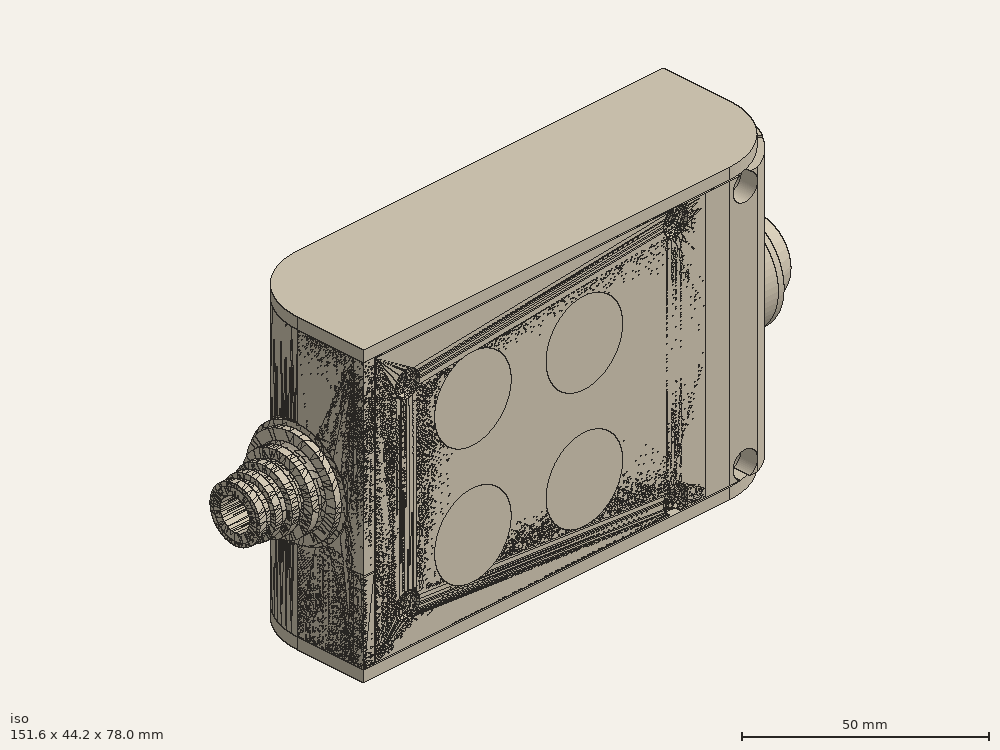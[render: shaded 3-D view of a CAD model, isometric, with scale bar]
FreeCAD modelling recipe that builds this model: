
FCSTD DOCUMENT  (FreeCAD 0.19R0.19.2)
Label: enclosure_160
License: All rights reserved
LicenseURL: http://en.wikipedia.org/wiki/All_rights_reserved
objects: Part::Feature×140, Part::Revolution×140, Part::MultiFuse×120, Sketcher::SketchObject×67, Part::Extrusion×52, Part::Fillet×51, Part::Cut×51, Part::Cylinder×50, Part::Box×33, App::MeasureDistance×4
note: 704 computed .brp shape members not serialized (recipe doc carries the construction recipe); baked Part::Feature solids carry a one-line shape summary decoded from their .brp

FEATURE [Sketcher::SketchObject] Sketch  label="topSketch"
  FullyConstrained = true
  sketch-geometry (20):
    g0: LineSegment StartX=5.21097e-06 StartY=3 StartZ=0 EndX=5.21097e-06 EndY=19 EndZ=0
    g1: ArcOfCircle CenterX=19 CenterY=19 CenterZ=0 NormalX=0 NormalY=0 NormalZ=1 AngleXU=0 Radius=19 StartAngle=1.5708 EndAngle=3.14159
    g2: ArcOfCircle CenterX=19 CenterY=19 CenterZ=0 NormalX=0 NormalY=0 NormalZ=1 AngleXU=0 Radius=16 StartAngle=1.5708 EndAngle=3.14159
    g3: LineSegment StartX=114 StartY=35 StartZ=0 EndX=19 EndY=35 EndZ=0
    g4: LineSegment StartX=5.21097e-06 StartY=3 StartZ=0 EndX=5.21097e-06 EndY=0 EndZ=0
    g5: LineSegment StartX=3 StartY=0 StartZ=0 EndX=5.21097e-06 EndY=0 EndZ=0
    g6: LineSegment StartX=3 StartY=19 StartZ=0 EndX=3 EndY=0 EndZ=0
    g7: LineSegment StartX=19 StartY=38 StartZ=0 EndX=124 EndY=38 EndZ=0
    g8: Circle CenterX=119 CenterY=35 CenterZ=0 NormalX=0 NormalY=0 NormalZ=1 AngleXU=0 Radius=1
    g9: Circle CenterX=121 CenterY=35 CenterZ=0 NormalX=0 NormalY=0 NormalZ=1 AngleXU=0 Radius=1
    g10: Circle CenterX=121 CenterY=33 CenterZ=0 NormalX=0 NormalY=0 NormalZ=1 AngleXU=0 Radius=1
    g11: BSplineCurve PolesCount=3 KnotsCount=2 Degree=2 IsPeriodic=0
    g12: GeomPoint X=119 Y=35 Z=0
    g13: GeomPoint X=121 Y=33 Z=0
    g14: LineSegment StartX=119 StartY=35 StartZ=0 EndX=114 EndY=35 EndZ=0
    g15: ArcOfCircle CenterX=105 CenterY=19 CenterZ=0 NormalX=0 NormalY=0 NormalZ=1 AngleXU=0 Radius=19 StartAngle=5.7297 EndAngle=6.28319
    g16: ArcOfCircle CenterX=105 CenterY=19 CenterZ=0 NormalX=0 NormalY=0 NormalZ=1 AngleXU=0 Radius=16 StartAngle=5.60905 EndAngle=6.28319
    g17: LineSegment StartX=121 StartY=33 StartZ=0 EndX=121 EndY=19 EndZ=0
    g18: LineSegment StartX=124 StartY=38 StartZ=0 EndX=124 EndY=19 EndZ=0
    g19: LineSegment StartX=117.5 StartY=9.01251 StartZ=0 EndX=121.163 EndY=9.0125 EndZ=0
  constraints (46):
    c: Vertical(g0)
    c: Block(g0)
    c: Coincident(g1,g0)
    c: Block(g1)
    c: Coincident(g2,g1)
    c: Block(g2)
    c: Coincident(g3,g2)
    c: Horizontal(g3)
    c: Tangent(g3,g2)
    c: Coincident(g4,g0)
    c: Distance(g4) = 3
    c: Vertical(g4)
    c: Coincident(g5,g4)
    c: Horizontal(g5)
    c: Coincident(g6,g2)
    c: Coincident(g6,g5)
    c: Vertical(g6)
    c: Horizontal(g7)
    c: Distance(g7) = 105
    c: Coincident(g7,g1)
    c: Block(g3)
    c: Weight(g8) = 1
    c: Equal(g8,g9)
    c: Equal(g8,g10)
    c: InternalAlignment(g8,g11)
    c: InternalAlignment(g9,g11)
    c: InternalAlignment(g10,g11)
    c: InternalAlignment(g12,g11)
    c: InternalAlignment(g13,g11)
    c: Block(g11)
    c: Coincident(g14,g11)
    c: Coincident(g14,g3)
    c: Horizontal(g14)
    c: Block(g15)
    c: Coincident(g16,g15)
    c: Block(g16)
    c: Coincident(g17,g11)
    c: Coincident(g17,g16)
    c: Vertical(g17)
    c: Distance(g17) = 14
    c: Coincident(g18,g7)
    c: Coincident(g18,g15)
    c: Vertical(g18)
    c: Distance(g18) = 19
    c: Coincident(g19,g16)
    c: Coincident(g19,g15)
FEATURE [Sketcher::SketchObject] Sketch001  label="bottomSketch"
  FullyConstrained = true
  sketch-geometry (32):
    g0: LineSegment StartX=3.3 StartY=-6.03275e-07 StartZ=0 EndX=98 EndY=-6.03275e-07 EndZ=0
    g1: ArcOfCircle CenterX=98 CenterY=19 CenterZ=0 NormalX=0 NormalY=0 NormalZ=1 AngleXU=0 Radius=19 StartAngle=4.71239 EndAngle=5.71103
    g2: LineSegment StartX=6.3 StartY=8 StartZ=0 EndX=3.3 EndY=8 EndZ=0
    g3: LineSegment StartX=3.3 StartY=8 StartZ=0 EndX=3.3 EndY=-6.03275e-07 EndZ=0
    g4: ArcOfCircle CenterX=8.3 CenterY=5 CenterZ=0 NormalX=0 NormalY=0 NormalZ=1 AngleXU=0 Radius=2 StartAngle=3.14159 EndAngle=4.71239
    g5: LineSegment StartX=6.3 StartY=8 StartZ=0 EndX=6.3 EndY=5 EndZ=0
    g6: ArcOfCircle CenterX=98 CenterY=19 CenterZ=0 NormalX=0 NormalY=0 NormalZ=1 AngleXU=0 Radius=12.7 StartAngle=4.71239 EndAngle=6.28319
    g7: LineSegment StartX=94.7 StartY=3 StartZ=0 EndX=8.3 EndY=3 EndZ=0
    g8-g12: Circle x5 (B-spline internal-alignment scaffolding for g13; pole/knot coordinates omitted)
    g13: BSplineCurve PolesCount=5 KnotsCount=3 Degree=3 IsPeriodic=0
    g14: GeomPoint X=98 Y=6.3 Z=0
    g15: GeomPoint X=96.3938 Y=4.71946 Z=0
    g16: GeomPoint X=94.7 Y=3 Z=0
    g17-g23: Circle x7 (B-spline internal-alignment scaffolding for g24; pole/knot coordinates omitted)
    g24: BSplineCurve PolesCount=7 KnotsCount=5 Degree=3 IsPeriodic=0
    g25-g29: GeomPoint x5 (B-spline internal-alignment scaffolding for g24; pole/knot coordinates omitted)
    g30: ArcOfCircle CenterX=98 CenterY=19 CenterZ=0 NormalX=0 NormalY=0 NormalZ=1 AngleXU=0 Radius=15.7 StartAngle=5.81226 EndAngle=6.28319
    g31: LineSegment StartX=110.7 StartY=19 StartZ=0 EndX=113.7 EndY=19 EndZ=0
  constraints (41):
    c: Horizontal(g0)
    c: Coincident(g1,g0)
    c: Block(g1)
    c: Horizontal(g2)
    c: Distance(g2) = 3
    c: Coincident(g3,g2)
    c: Vertical(g3)
    c: Coincident(g3,g0)
    c: Block(g4)
    c: Block(g2)
    c: Coincident(g5,g2)
    c: Coincident(g5,g4)
    c: Vertical(g5)
    c: Coincident(g6,g1)
    c: Block(g6)
    c: Coincident(g7,g4)
    c: Horizontal(g7)
    c: Block(g0)
    c: Block(g7)
    c: Block(g3)
    c: Coincident(g13,g6)
    c: Weight(g8) = 1
    c: Equal(g8, g9-g12) x4
    c: Coincident(g13,g7)
    c: InternalAlignment(g8-g12 -> g13) x5
    c: InternalAlignment(g14,g13)
    c: InternalAlignment(g15,g13)
    c: InternalAlignment(g16,g13)
    c: Block(g13)
    c: Weight(g17) = 1
    c: Equal(g17, g18-g23) x6
    c: Coincident(g24,g1)
    c: InternalAlignment(g17-g23 -> g24) x7
    c: InternalAlignment(g25-g29 -> g24) x5
    c: Block(g24)
    c: Coincident(g30,g24)
    c: Coincident(g31,g6)
    c: Coincident(g31,g30)
    c: Horizontal(g31)
    c: Block(g31)
    c: Block(g30)
FEATURE [Part::Extrusion] Extrude  label="top"
  Base = -> Sketch
  Dir = (0,0,1)
  DirMode = 2
  FaceMakerClass = Part::FaceMakerBullseye
  LengthFwd = 72
  LengthRev = 0
  Solid = true
  Symmetric = false
FEATURE [Part::Extrusion] Extrude001  label="bottom"
  Base = -> Sketch001
  Dir = (0,0,1)
  DirMode = 2
  FaceMakerClass = Part::FaceMakerBullseye
  LengthFwd = 71.4
  LengthRev = 0
  Placement = pos=(0,0,0.3) rot=(0,0,1;0rad)
  Solid = true
  Symmetric = false
FEATURE [Sketcher::SketchObject] Sketch002  label="topSketch001"
  FullyConstrained = true
  sketch-geometry (6):
    g0: ArcOfCircle CenterX=19 CenterY=19 CenterZ=0 NormalX=0 NormalY=0 NormalZ=1 AngleXU=0 Radius=19 StartAngle=1.5708 EndAngle=3.14159
    g1: LineSegment StartX=5.22862e-06 StartY=19 StartZ=0 EndX=5.22862e-06 EndY=1.19904e-11 EndZ=0
    g2: LineSegment StartX=19 StartY=38 StartZ=0 EndX=124 EndY=38 EndZ=0
    g3: LineSegment StartX=5.22862e-06 StartY=1.19904e-11 StartZ=0 EndX=105 EndY=1.19904e-11 EndZ=0
    g4: ArcOfCircle CenterX=105 CenterY=19 CenterZ=0 NormalX=0 NormalY=0 NormalZ=1 AngleXU=0 Radius=19 StartAngle=4.71239 EndAngle=6.28319
    g5: LineSegment StartX=124 StartY=38 StartZ=0 EndX=124 EndY=19 EndZ=0
  constraints (16):
    c: Block(g0)
    c: Coincident(g1,g0)
    c: Vertical(g1)
    c: Horizontal(g2)
    c: Distance(g2) = 105
    c: Coincident(g2,g0)
    c: Distance(g1) = 19
    c: Coincident(g3,g1)
    c: Horizontal(g3)
    c: Distance(g3) = 105
    c: Block(g4)
    c: Coincident(g4,g3)
    c: Coincident(g5,g2)
    c: Coincident(g5,g4)
    c: Vertical(g5)
    c: Distance(g5) = 19
FEATURE [Part::Extrusion] Extrude002  label="sideA"
  Base = -> Sketch002
  Dir = (0,0,1)
  DirMode = 2
  FaceMakerClass = Part::FaceMakerBullseye
  LengthFwd = 3
  LengthRev = 0
  Placement = pos=(0,0,-3) rot=(0,0,1;0rad)
  Solid = true
  Symmetric = false
FEATURE [Sketcher::SketchObject] Sketch003  label="topSketch002"
  FullyConstrained = true
  sketch-geometry (6):
    g0: LineSegment StartX=19 StartY=38 StartZ=0 EndX=117 EndY=38 EndZ=0
    g1: ArcOfCircle CenterX=19 CenterY=19 CenterZ=0 NormalX=0 NormalY=0 NormalZ=1 AngleXU=0 Radius=19 StartAngle=1.5708 EndAngle=3.14159
    g2: LineSegment StartX=117 StartY=38 StartZ=0 EndX=117 EndY=19 EndZ=0
    g3: LineSegment StartX=98 StartY=1.0161e-12 StartZ=0 EndX=5.22862e-06 EndY=1.0161e-12 EndZ=0
    g4: LineSegment StartX=5.22862e-06 StartY=19 StartZ=0 EndX=5.22862e-06 EndY=1.0161e-12 EndZ=0
    g5: ArcOfCircle CenterX=98 CenterY=19 CenterZ=0 NormalX=0 NormalY=0 NormalZ=1 AngleXU=0 Radius=19 StartAngle=4.71239 EndAngle=6.28319
  constraints (16):
    c: Horizontal(g0)
    c: Distance(g0) = 98
    c: Coincident(g1,g0)
    c: Block(g1)
    c: Coincident(g2,g0)
    c: Vertical(g2)
    c: Distance(g2) = 19
    c: Horizontal(g3)
    c: Coincident(g4,g1)
    c: Vertical(g4)
    c: Coincident(g3,g4)
    c: Block(g3)
    c: Coincident(g5,g2)
    c: Coincident(g5,g3)
    c: Block(g0)
    c: Block(g5)
FEATURE [Sketcher::SketchObject] Sketch004
  FullyConstrained = true
  MapMode = 3
  Placement = pos=(0,0,0) rot=(1,0,0;1.5708rad)
  Support = -> [Extrude]
  sketch-geometry (8):
    g0: Circle CenterX=80.351 CenterY=-67.6202 CenterZ=0 NormalX=0 NormalY=0 NormalZ=1 AngleXU=0 Radius=2
    g1: Circle CenterX=80.351 CenterY=-67.6202 CenterZ=0 NormalX=0 NormalY=0 NormalZ=1 AngleXU=0 Radius=3
    g2: Circle CenterX=80.351 CenterY=-4.92017 CenterZ=0 NormalX=0 NormalY=0 NormalZ=1 AngleXU=0 Radius=2
    g3: Circle CenterX=80.351 CenterY=-4.92017 CenterZ=0 NormalX=0 NormalY=0 NormalZ=1 AngleXU=0 Radius=3
    g4: Circle CenterX=23.851 CenterY=-4.92017 CenterZ=0 NormalX=0 NormalY=0 NormalZ=1 AngleXU=0 Radius=2
    g5: Circle CenterX=23.851 CenterY=-4.92017 CenterZ=0 NormalX=0 NormalY=0 NormalZ=1 AngleXU=0 Radius=3
    g6: Circle CenterX=23.851 CenterY=-67.6202 CenterZ=0 NormalX=0 NormalY=0 NormalZ=1 AngleXU=0 Radius=2
    g7: Circle CenterX=23.851 CenterY=-67.6202 CenterZ=0 NormalX=0 NormalY=0 NormalZ=1 AngleXU=0 Radius=3
  constraints (8):
    c: Block(g3)
    c: Block(g2)
    c: Block(g1)
    c: Block(g0)
    c: Block(g6)
    c: Block(g7)
    c: Block(g4)
    c: Block(g5)
FEATURE [Part::Extrusion] Extrude004
  Base = -> Sketch004
  Dir = (0,-1,2e-16)
  DirMode = 2
  FaceMakerClass = Part::FaceMakerBullseye
  LengthFwd = 6
  LengthRev = 0
  Placement = pos=(0,9,0) rot=(0,0,1;0rad)
  Solid = true
  Symmetric = false
FEATURE [Sketcher::SketchObject] Sketch005
  FullyConstrained = true
  MapMode = 3
  Placement = pos=(0,0,0) rot=(1,0,0;1.5708rad)
  Support = -> [Extrude]
  sketch-geometry (8):
    g0: Circle CenterX=80.351 CenterY=-67.6202 CenterZ=0 NormalX=0 NormalY=0 NormalZ=1 AngleXU=0 Radius=3
    g1: Circle CenterX=80.351 CenterY=-4.92017 CenterZ=0 NormalX=0 NormalY=0 NormalZ=1 AngleXU=0 Radius=3
    g2: Circle CenterX=23.851 CenterY=-4.92017 CenterZ=0 NormalX=0 NormalY=0 NormalZ=1 AngleXU=0 Radius=3
    g3: Circle CenterX=23.851 CenterY=-67.6202 CenterZ=0 NormalX=0 NormalY=0 NormalZ=1 AngleXU=0 Radius=3
    g4: Circle CenterX=23.851 CenterY=-67.6202 CenterZ=0 NormalX=0 NormalY=0 NormalZ=1 AngleXU=0 Radius=5
    g5: Circle CenterX=80.351 CenterY=-67.6202 CenterZ=0 NormalX=0 NormalY=0 NormalZ=1 AngleXU=0 Radius=5
    g6: Circle CenterX=23.851 CenterY=-4.92017 CenterZ=0 NormalX=0 NormalY=0 NormalZ=1 AngleXU=0 Radius=5
    g7: Circle CenterX=80.351 CenterY=-4.92017 CenterZ=0 NormalX=0 NormalY=0 NormalZ=1 AngleXU=0 Radius=5
  constraints (8):
    c: Block(g1)
    c: Block(g0)
    c: Block(g3)
    c: Block(g2)
    c: Block(g5)
    c: Block(g4)
    c: Block(g6)
    c: Block(g7)
FEATURE [Part::Extrusion] Extrude005
  Base = -> Sketch005
  Dir = (0,-1,2e-16)
  DirMode = 2
  FaceMakerClass = Part::FaceMakerBullseye
  LengthFwd = 2
  LengthRev = 0
  Solid = true
  Symmetric = false
FEATURE [Sketcher::SketchObject] Sketch006
  FullyConstrained = true
  MapMode = 3
  Placement = pos=(0,0,0) rot=(1,0,0;1.5708rad)
  sketch-geometry (8):
    g0: Circle CenterX=80.351 CenterY=-67.6202 CenterZ=0 NormalX=0 NormalY=0 NormalZ=1 AngleXU=0 Radius=3
    g1: Circle CenterX=80.351 CenterY=-4.92017 CenterZ=0 NormalX=0 NormalY=0 NormalZ=1 AngleXU=0 Radius=3
    g2: Circle CenterX=23.851 CenterY=-4.92017 CenterZ=0 NormalX=0 NormalY=0 NormalZ=1 AngleXU=0 Radius=3
    g3: Circle CenterX=23.851 CenterY=-67.6202 CenterZ=0 NormalX=0 NormalY=0 NormalZ=1 AngleXU=0 Radius=3
    g4: Circle CenterX=23.851 CenterY=-67.6202 CenterZ=0 NormalX=0 NormalY=0 NormalZ=1 AngleXU=0 Radius=5
    g5: Circle CenterX=80.351 CenterY=-67.6202 CenterZ=0 NormalX=0 NormalY=0 NormalZ=1 AngleXU=0 Radius=5
    g6: Circle CenterX=23.851 CenterY=-4.92017 CenterZ=0 NormalX=0 NormalY=0 NormalZ=1 AngleXU=0 Radius=5
    g7: Circle CenterX=80.351 CenterY=-4.92017 CenterZ=0 NormalX=0 NormalY=0 NormalZ=1 AngleXU=0 Radius=5
  constraints (8):
    c: Block(g1)
    c: Block(g0)
    c: Block(g3)
    c: Block(g2)
    c: Block(g5)
    c: Block(g4)
    c: Block(g6)
    c: Block(g7)
FEATURE [Part::Extrusion] Extrude007
  Base = -> Sketch006
  Dir = (0,-1,2e-16)
  DirMode = 2
  FaceMakerClass = Part::FaceMakerBullseye
  LengthFwd = 2
  LengthRev = 0
  Solid = true
  Symmetric = false
FEATURE [Part::Fillet] Fillet
  Base = -> Extrude007
  Edges = 4 edges r=1.99: [Edge6,Edge12,Edge18,Edge24]
FEATURE [Part::Cut] Cut
  Base = -> Extrude005
  Placement = pos=(0,5,0) rot=(0,0,1;0rad)
  Tool = -> Fillet
FEATURE [Part::MultiFuse] Fusion  label="pCBScrews"
  Placement = pos=(-2.5,0,72.3) rot=(0,0,1;0rad)
  Shapes = -> [Extrude004,Cut]
FEATURE [App::MeasureDistance] Distance  label="Distance: 0.69 mm"
  Distance = 0.685967
  P1 = (24.0138,2.9647,0.3)
  P2 = (23.8901,3,-0.373787)
FEATURE [App::MeasureDistance] Distance001  label="Distance: 0.53 mm"
  Distance = 0.533607
  P1 = (80.2939,3,72.2334)
  P2 = (80.281,2.99661,71.7)
FEATURE [Part::Fillet] Fillet001
  Base = -> Extrude001
  Edges = 1 edges r=2.4: [Edge17]
FEATURE [Part::Fillet] Fillet002  label="bottom001"
  Base = -> Fillet001
  Edges = 1 edges r=2.4: [Edge36]
FEATURE [Part::Fillet] Fillet003  label="top001"
  Base = -> Extrude
  Edges = 1 edges r=2: [Edge1]
FEATURE [Sketcher::SketchObject] Sketch007
  FullyConstrained = true
  sketch-geometry (16):
    g0: LineSegment StartX=4 StartY=0 StartZ=0 EndX=4 EndY=2.4 EndZ=0
    g1: LineSegment StartX=4 StartY=2.4 StartZ=0 EndX=7 EndY=2.4 EndZ=0
    g2: LineSegment StartX=4 StartY=0 StartZ=0 EndX=5.7 EndY=0 EndZ=0
    g3: LineSegment StartX=5.7 StartY=0 StartZ=0 EndX=5.7 EndY=-5.6 EndZ=0
    g4-g8: Circle x5 (B-spline internal-alignment scaffolding for g9; pole/knot coordinates omitted)
    g9: BSplineCurve PolesCount=5 KnotsCount=3 Degree=3 IsPeriodic=0
    g10: GeomPoint X=7 Y=2.4 Z=0
    g11: GeomPoint X=10.4582 Y=-1.55472 Z=0
    g12: GeomPoint X=14 Y=-5.6 Z=0
    g13: LineSegment StartX=14 StartY=-5.6 StartZ=0 EndX=14 EndY=-14.1 EndZ=0
    g14: LineSegment StartX=14 StartY=-14.1 StartZ=0 EndX=6.5 EndY=-14.1 EndZ=0
    g15: LineSegment StartX=5.7 StartY=-5.6 StartZ=0 EndX=6.5 EndY=-14.1 EndZ=0
  constraints (28):
    c: Distance(g0) = 2.4
    c: Vertical(g0)
    c: Block(g0)
    c: Coincident(g1,g0)
    c: Horizontal(g1)
    c: Distance(g1) = 3
    c: Coincident(g2,g0)
    c: Horizontal(g2)
    c: Distance(g2) = 1.7
    c: Coincident(g3,g2)
    c: Vertical(g3)
    c: Distance(g3) = 5.6
    c: Coincident(g9,g1)
    c: Weight(g4) = 1
    c: Equal(g4, g5-g8) x4
    c: InternalAlignment(g4-g8 -> g9) x5
    c: InternalAlignment(g10,g9)
    c: InternalAlignment(g11,g9)
    c: InternalAlignment(g12,g9)
    c: Block(g9)
    c: Coincident(g13,g9)
    c: Vertical(g13)
    c: Distance(g13) = 8.5
    c: Coincident(g14,g13)
    c: Horizontal(g14)
    c: Distance(g14) = 7.5
    c: Coincident(g15,g3)
    c: Coincident(g15,g14)
FEATURE [Part::Feature] Face
  shape: bbox 10 x 16.5 x 2e-07 mm, 1 faces, 0 solids (baked)
FEATURE [Part::Revolution] Revolve  label="plugHousing"
  Angle = 360
  Axis = (0,1,0)
  Base = (0,0,0)
  FaceMakerClass = Part::FaceMakerBullseye
  Placement = pos=(0,0,36.15) rot=(0,0,1;0rad)
  Solid = false
  Source = -> Face
  Symmetric = false
FEATURE [Part::Feature] Face001
  shape: bbox 10 x 16.5 x 2e-07 mm, 1 faces, 0 solids (baked)
FEATURE [Part::Revolution] Revolve001  label="plugHousing001"
  Angle = 360
  Axis = (0,1,0)
  Base = (0,0,0)
  FaceMakerClass = Part::FaceMakerBullseye
  Placement = pos=(0,0,36.15) rot=(0,0,1;0rad)
  Solid = false
  Source = -> Face001
  Symmetric = false
FEATURE [Part::MultiFuse] Fusion001  label="plugHousing002"
  Placement = pos=(0,0,0) rot=(0,0,1;1.5708rad)
  Shapes = -> [Revolve001,Revolve]
FEATURE [Part::Feature] Face002
  shape: bbox 10 x 16.5 x 2e-07 mm, 1 faces, 0 solids (baked)
FEATURE [Part::Revolution] Revolve003  label="plugHousing005"
  Angle = 360
  Axis = (0,1,0)
  Base = (0,0,0)
  FaceMakerClass = Part::FaceMakerBullseye
  Placement = pos=(0,0,36.15) rot=(0,0,1;0rad)
  Solid = false
  Source = -> Face002
  Symmetric = false
FEATURE [Part::Feature] Face003
  shape: bbox 10 x 16.5 x 2e-07 mm, 1 faces, 0 solids (baked)
FEATURE [Part::Revolution] Revolve002  label="plugHousing003"
  Angle = 360
  Axis = (0,1,0)
  Base = (0,0,0)
  FaceMakerClass = Part::FaceMakerBullseye
  Placement = pos=(0,0,36.15) rot=(0,0,1;0rad)
  Solid = false
  Source = -> Face003
  Symmetric = false
FEATURE [Part::MultiFuse] Fusion002  label="plugHousing004"
  Placement = pos=(0,0,0) rot=(0,0,1;1.5708rad)
  Shapes = -> [Revolve002,Revolve003]
FEATURE [Part::MultiFuse] Fusion003  label="plugHousing006"
  Placement = pos=(0,19,0) rot=(0,0,1;3.14159rad)
  Shapes = -> [Fusion002,Fusion001]
FEATURE [Part::Feature] Face004
  shape: bbox 10 x 16.5 x 2e-07 mm, 1 faces, 0 solids (baked)
FEATURE [Part::Revolution] Revolve006  label="plugHousing010"
  Angle = 360
  Axis = (0,1,0)
  Base = (0,0,0)
  FaceMakerClass = Part::FaceMakerBullseye
  Placement = pos=(0,0,36.15) rot=(0,0,1;0rad)
  Solid = false
  Source = -> Face004
  Symmetric = false
FEATURE [Part::Feature] Face005
  shape: bbox 10 x 16.5 x 2e-07 mm, 1 faces, 0 solids (baked)
FEATURE [Part::Revolution] Revolve007  label="plugHousing011"
  Angle = 360
  Axis = (0,1,0)
  Base = (0,0,0)
  FaceMakerClass = Part::FaceMakerBullseye
  Placement = pos=(0,0,36.15) rot=(0,0,1;0rad)
  Solid = false
  Source = -> Face005
  Symmetric = false
FEATURE [Part::Feature] Face006
  shape: bbox 10 x 16.5 x 2e-07 mm, 1 faces, 0 solids (baked)
FEATURE [Part::Revolution] Revolve004  label="plugHousing007"
  Angle = 360
  Axis = (0,1,0)
  Base = (0,0,0)
  FaceMakerClass = Part::FaceMakerBullseye
  Placement = pos=(0,0,36.15) rot=(0,0,1;0rad)
  Solid = false
  Source = -> Face006
  Symmetric = false
FEATURE [Part::MultiFuse] Fusion004  label="plugHousing009"
  Placement = pos=(0,0,0) rot=(0,0,1;1.5708rad)
  Shapes = -> [Revolve004,Revolve007]
FEATURE [Part::Feature] Face007
  shape: bbox 10 x 16.5 x 2e-07 mm, 1 faces, 0 solids (baked)
FEATURE [Part::Revolution] Revolve005  label="plugHousing008"
  Angle = 360
  Axis = (0,1,0)
  Base = (0,0,0)
  FaceMakerClass = Part::FaceMakerBullseye
  Placement = pos=(0,0,36.15) rot=(0,0,1;0rad)
  Solid = false
  Source = -> Face007
  Symmetric = false
FEATURE [Part::MultiFuse] Fusion005  label="plugHousing012"
  Placement = pos=(0,0,0) rot=(0,0,1;1.5708rad)
  Shapes = -> [Revolve006,Revolve005]
FEATURE [Part::MultiFuse] Fusion006  label="plugHousing013"
  Placement = pos=(0,19,0) rot=(0,0,1;3.14159rad)
  Shapes = -> [Fusion005,Fusion004]
FEATURE [Part::MultiFuse] Fusion007  label="plugHousing014"
  Placement = pos=(122.621,0,-0.15) rot=(0,0,1;0rad)
  Shapes = -> [Fusion003,Fusion006]
FEATURE [Part::Cylinder] Cylinder002
  Angle = 360
  AttacherType = Attacher::AttachEngine3D
  Height = 20
  Placement = pos=(0,0,36.15) rot=(0,0,1;0rad)
  Radius = 4
FEATURE [Part::Cylinder] Cylinder003
  Angle = 360
  AttacherType = Attacher::AttachEngine3D
  Height = 10
  Placement = pos=(0,0,36.15) rot=(0,0,1;0rad)
  Radius = 4
FEATURE [Part::MultiFuse] Fusion009  label="removeToCreateHoleForPlugHousing"
  Placement = pos=(70,19,36.15) rot=(0,1,0;1.5708rad)
  Shapes = -> [Cylinder002,Cylinder003]
FEATURE [Part::Cylinder] Cylinder004
  Angle = 360
  AttacherType = Attacher::AttachEngine3D
  Height = 20
  Placement = pos=(0,0,36.15) rot=(0,0,1;0rad)
  Radius = 4
FEATURE [Part::Cylinder] Cylinder005
  Angle = 360
  AttacherType = Attacher::AttachEngine3D
  Height = 10
  Placement = pos=(0,0,36.15) rot=(0,0,1;0rad)
  Radius = 4
FEATURE [Part::MultiFuse] Fusion010  label="removeToCreateHoleForPlugHousing001"
  Placement = pos=(70,19,36.15) rot=(0,1,0;1.5708rad)
  Shapes = -> [Cylinder004,Cylinder005]
FEATURE [Part::Cut] Cut001
  Base = -> Fillet003
  Tool = -> Fusion010
FEATURE [Part::Cut] Cut002  label="Bottom"
  Base = -> Fillet002
  Tool = -> Fusion009
FEATURE [Part::Feature] Face008
  shape: bbox 10 x 16.5 x 2e-07 mm, 1 faces, 0 solids (baked)
FEATURE [Part::Revolution] Revolve011  label="plugHousing021"
  Angle = 360
  Axis = (0,1,0)
  Base = (0,0,0)
  FaceMakerClass = Part::FaceMakerBullseye
  Placement = pos=(0,0,36.15) rot=(0,0,1;0rad)
  Solid = false
  Source = -> Face008
  Symmetric = false
FEATURE [Part::Feature] Face009
  shape: bbox 10 x 16.5 x 2e-07 mm, 1 faces, 0 solids (baked)
FEATURE [Part::Revolution] Revolve012  label="plugHousing022"
  Angle = 360
  Axis = (0,1,0)
  Base = (0,0,0)
  FaceMakerClass = Part::FaceMakerBullseye
  Placement = pos=(0,0,36.15) rot=(0,0,1;0rad)
  Solid = false
  Source = -> Face009
  Symmetric = false
FEATURE [Part::Feature] Face010 .. Face013  x4 (patterned run collapsed; names and placements below)
  shape: bbox 10 x 16.5 x 2e-07 mm, 1 faces, 0 solids (baked)
FEATURE [Part::Revolution] Revolve015  label="plugHousing027"
  Angle = 360
  Axis = (0,1,0)
  Base = (0,0,0)
  FaceMakerClass = Part::FaceMakerBullseye
  Placement = pos=(0,0,36.15) rot=(0,0,1;0rad)
  Solid = false
  Source = -> Face013
  Symmetric = false
FEATURE [Part::Feature] Face014
  shape: bbox 10 x 16.5 x 2e-07 mm, 1 faces, 0 solids (baked)
FEATURE [Part::Feature] Face015
  shape: bbox 10 x 16.5 x 2e-07 mm, 1 faces, 0 solids (baked)
FEATURE [Part::Feature] Face016
  shape: bbox 10 x 16.5 x 2e-07 mm, 1 faces, 0 solids (baked)
FEATURE [Part::Revolution] Revolve019  label="plugHousing033"
  Angle = 360
  Axis = (0,1,0)
  Base = (0,0,0)
  FaceMakerClass = Part::FaceMakerBullseye
  Placement = pos=(0,0,36.15) rot=(0,0,1;0rad)
  Solid = false
  Source = -> Face016
  Symmetric = false
FEATURE [Part::Feature] Face017
  shape: bbox 10 x 16.5 x 2e-07 mm, 1 faces, 0 solids (baked)
FEATURE [Part::Revolution] Revolve020  label="plugHousing034"
  Angle = 360
  Axis = (0,1,0)
  Base = (0,0,0)
  FaceMakerClass = Part::FaceMakerBullseye
  Placement = pos=(0,0,36.15) rot=(0,0,1;0rad)
  Solid = false
  Source = -> Face017
  Symmetric = false
FEATURE [Part::Feature] Face018
  shape: bbox 10 x 16.5 x 2e-07 mm, 1 faces, 0 solids (baked)
FEATURE [Part::Revolution] Revolve016  label="plugHousing030"
  Angle = 360
  Axis = (0,1,0)
  Base = (0,0,0)
  FaceMakerClass = Part::FaceMakerBullseye
  Placement = pos=(0,0,36.15) rot=(0,0,1;0rad)
  Solid = false
  Source = -> Face018
  Symmetric = false
FEATURE [Part::MultiFuse] Fusion020  label="plugHousing038"
  Placement = pos=(0,0,0) rot=(0,0,1;1.5708rad)
  Shapes = -> [Revolve016,Revolve020]
FEATURE [Part::Feature] Face019
  shape: bbox 10 x 16.5 x 2e-07 mm, 1 faces, 0 solids (baked)
FEATURE [Part::Feature] Face020
  shape: bbox 10 x 16.5 x 2e-07 mm, 1 faces, 0 solids (baked)
FEATURE [Part::Revolution] Revolve017  label="plugHousing031"
  Angle = 360
  Axis = (0,1,0)
  Base = (0,0,0)
  FaceMakerClass = Part::FaceMakerBullseye
  Placement = pos=(0,0,36.15) rot=(0,0,1;0rad)
  Solid = false
  Source = -> Face020
  Symmetric = false
FEATURE [Part::MultiFuse] Fusion021  label="plugHousing039"
  Placement = pos=(0,0,0) rot=(0,0,1;1.5708rad)
  Shapes = -> [Revolve019,Revolve017]
FEATURE [Part::MultiFuse] Fusion023  label="plugHousing041"
  Placement = pos=(0,19,0) rot=(0,0,1;3.14159rad)
  Shapes = -> [Fusion021,Fusion020]
FEATURE [Part::Revolution] Revolve022  label="plugHousing043"
  Angle = 360
  Axis = (0,1,0)
  Base = (0,0,0)
  FaceMakerClass = Part::FaceMakerBullseye
  Placement = pos=(0,0,36.15) rot=(0,0,1;0rad)
  Solid = false
  Source = -> Face019
  Symmetric = false
FEATURE [Part::Feature] Face021
  shape: bbox 10 x 16.5 x 2e-07 mm, 1 faces, 0 solids (baked)
FEATURE [Part::Revolution] Revolve023  label="plugHousing044"
  Angle = 360
  Axis = (0,1,0)
  Base = (0,0,0)
  FaceMakerClass = Part::FaceMakerBullseye
  Placement = pos=(0,0,36.15) rot=(0,0,1;0rad)
  Solid = false
  Source = -> Face021
  Symmetric = false
FEATURE [Part::Feature] Face022
  shape: bbox 10 x 16.5 x 2e-07 mm, 1 faces, 0 solids (baked)
FEATURE [Part::Revolution] Revolve018  label="plugHousing032"
  Angle = 360
  Axis = (0,1,0)
  Base = (0,0,0)
  FaceMakerClass = Part::FaceMakerBullseye
  Placement = pos=(0,0,36.15) rot=(0,0,1;0rad)
  Solid = false
  Source = -> Face022
  Symmetric = false
FEATURE [Part::MultiFuse] Fusion022  label="plugHousing040"
  Placement = pos=(0,0,0) rot=(0,0,1;1.5708rad)
  Shapes = -> [Revolve018,Revolve023]
FEATURE [Part::Feature] Face023
  shape: bbox 10 x 16.5 x 2e-07 mm, 1 faces, 0 solids (baked)
FEATURE [Part::Revolution] Revolve021  label="plugHousing035"
  Angle = 360
  Axis = (0,1,0)
  Base = (0,0,0)
  FaceMakerClass = Part::FaceMakerBullseye
  Placement = pos=(0,0,36.15) rot=(0,0,1;0rad)
  Solid = false
  Source = -> Face023
  Symmetric = false
FEATURE [Part::MultiFuse] Fusion018  label="plugHousing036"
  Placement = pos=(0,0,0) rot=(0,0,1;1.5708rad)
  Shapes = -> [Revolve022,Revolve021]
FEATURE [Part::MultiFuse] Fusion019  label="plugHousing037"
  Placement = pos=(0,19,0) rot=(0,0,1;3.14159rad)
  Shapes = -> [Fusion018,Fusion022]
FEATURE [Part::MultiFuse] Fusion024  label="plugHousing042"
  Placement = pos=(122.621,0,-0.15) rot=(0,0,1;0rad)
  Shapes = -> [Fusion023,Fusion019]
FEATURE [Part::Cylinder] Cylinder006
  Angle = 360
  AttacherType = Attacher::AttachEngine3D
  Height = 20
  Placement = pos=(0,0,36.15) rot=(0,0,1;0rad)
  Radius = 14.3
FEATURE [Part::Cylinder] Cylinder007
  Angle = 360
  AttacherType = Attacher::AttachEngine3D
  Height = 10
  Placement = pos=(0,0,36.15) rot=(0,0,1;0rad)
  Radius = 4
FEATURE [Part::MultiFuse] Fusion026  label="removeToCreteHoleForPlugHousing"
  Placement = pos=(70,19,36) rot=(0,1,0;1.5708rad)
  Shapes = -> [Cylinder006,Cylinder007]
FEATURE [Part::Box] Box001  label="Cube001"
  AttacherType = Attacher::AttachEngine3D
  Height = 28
  Length = 3
  Placement = pos=(110.7,19,22) rot=(0,0,1;0rad)
  Width = 15.7
FEATURE [Part::Cut] Cut003  label="top002"
  Base = -> Cut001
  Tool = -> Fusion007
FEATURE [Part::Revolution] Revolve008  label="plugHousing015"
  Angle = 360
  Axis = (0,1,0)
  Base = (0,0,0)
  FaceMakerClass = Part::FaceMakerBullseye
  Placement = pos=(0,0,36.15) rot=(0,0,1;0rad)
  Solid = false
  Source = -> Face010
  Symmetric = false
FEATURE [Part::MultiFuse] Fusion013  label="plugHousing020"
  Placement = pos=(0,0,0) rot=(0,0,1;1.5708rad)
  Shapes = -> [Revolve008,Revolve012]
FEATURE [Part::Cut] Cut004  label="top003"
  Base = -> Cut003
  Placement = pos=(1,0,0) rot=(0,0,1;0rad)
  Tool = -> Fusion026
FEATURE [Part::Cylinder] Cylinder008
  Angle = 360
  AttacherType = Attacher::AttachEngine3D
  Height = 20
  Placement = pos=(0,0,36.15) rot=(0,0,1;0rad)
  Radius = 10.3
FEATURE [Part::Cylinder] Cylinder009
  Angle = 360
  AttacherType = Attacher::AttachEngine3D
  Height = 10
  Placement = pos=(0,0,36.15) rot=(0,0,1;0rad)
  Radius = 4
FEATURE [Part::MultiFuse] Fusion027  label="removeToCreteHoleForPlugHousing001"
  Placement = pos=(70,19,36) rot=(0,1,0;1.5708rad)
  Shapes = -> [Cylinder008,Cylinder009]
FEATURE [Part::Cut] Cut005  label="plugHousingTab"
  Base = -> Box001
  Tool = -> Fusion027
FEATURE [Part::MultiFuse] Fusion028  label="plugHousing045"
  Shapes = -> [Fusion024,Cut005]
FEATURE [Part::Box] Box002  label="Cube002"
  AttacherType = Attacher::AttachEngine3D
  Height = 28.8
  Length = 3
  Placement = pos=(107.3,28,21.6) rot=(0,0,1;0rad)
  Width = 7
FEATURE [Part::Box] Box003  label="Cube003"
  AttacherType = Attacher::AttachEngine3D
  Height = 3
  Length = 6.4
  Placement = pos=(107.3,28,18.6) rot=(0,0,1;0rad)
  Width = 7
FEATURE [Part::Box] Box004  label="Cube004"
  AttacherType = Attacher::AttachEngine3D
  Height = 3
  Length = 6.4
  Placement = pos=(107.3,28,50.4) rot=(0,0,1;0rad)
  Width = 7
FEATURE [Part::MultiFuse] Fusion029  label="plugHousingBracketHolder"
  Shapes = -> [Box004,Box002,Box003]
FEATURE [Part::Cylinder] Cylinder010
  Angle = 360
  AttacherType = Attacher::AttachEngine3D
  Height = 20
  Placement = pos=(0,0,36.15) rot=(0,0,1;0rad)
  Radius = 14.3
FEATURE [Part::Cylinder] Cylinder011
  Angle = 360
  AttacherType = Attacher::AttachEngine3D
  Height = 10
  Placement = pos=(0,0,36.15) rot=(0,0,1;0rad)
  Radius = 4
FEATURE [Part::MultiFuse] Fusion030  label="removeToCreteHoleForPlugHousing002"
  Placement = pos=(70,19,36) rot=(0,1,0;1.5708rad)
  Shapes = -> [Cylinder010,Cylinder011]
FEATURE [Part::Cut] Cut006  label="plugHousingBracketHolder001"
  Base = -> Fusion029
  Tool = -> Fusion030
FEATURE [Part::Cylinder] Cylinder012
  Angle = 360
  AttacherType = Attacher::AttachEngine3D
  Height = 20
  Placement = pos=(0,0,36.15) rot=(0,0,1;0rad)
  Radius = 7
FEATURE [Part::Cylinder] Cylinder013
  Angle = 360
  AttacherType = Attacher::AttachEngine3D
  Height = 10
  Placement = pos=(0,0,36.15) rot=(0,0,1;0rad)
  Radius = 4
FEATURE [Part::MultiFuse] Fusion032  label="removeToCreteHoleForPlugHousing003"
  Placement = pos=(70,19,36) rot=(0,1,0;1.5708rad)
  Shapes = -> [Cylinder012,Cylinder013]
FEATURE [Part::Cut] Cut007  label="bottom002"
  Base = -> Cut002
  Tool = -> Fusion032
FEATURE [Sketcher::SketchObject] Sketch008
  FullyConstrained = true
  sketch-geometry (54):
    g0: LineSegment StartX=-4.2 StartY=0 StartZ=0 EndX=-6.2 EndY=0 EndZ=0
    g1: LineSegment StartX=-14 StartY=-18 StartZ=0 EndX=-14 EndY=-26.5 EndZ=0
    g2: LineSegment StartX=-4.2 StartY=0 StartZ=0 EndX=-4.2 EndY=-13.4877 EndZ=0
    g3: Circle CenterX=-4.2 CenterY=-13.4877 CenterZ=0 NormalX=0 NormalY=0 NormalZ=1 AngleXU=0 Radius=1
    g4: Circle CenterX=-4.2 CenterY=-26.5 CenterZ=0 NormalX=0 NormalY=0 NormalZ=1 AngleXU=0 Radius=1
    g5: Circle CenterX=-8.2 CenterY=-26.5 CenterZ=0 NormalX=0 NormalY=0 NormalZ=1 AngleXU=0 Radius=1
    g6: BSplineCurve PolesCount=3 KnotsCount=2 Degree=2 IsPeriodic=0
    g7: GeomPoint X=-4.2 Y=-13.4877 Z=0
    g8: GeomPoint X=-8.2 Y=-26.5 Z=0
    g9: LineSegment StartX=-14 StartY=-26.5 StartZ=0 EndX=-8.2 EndY=-26.5 EndZ=0
    g10: LineSegment StartX=-10.15 StartY=-12 StartZ=0 EndX=-10.15 EndY=-14 EndZ=0
    g11: LineSegment StartX=-12.8401 StartY=-16 StartZ=0 EndX=-10.1571 EndY=-16 EndZ=0
    g12: LineSegment StartX=-10.15 StartY=-14 StartZ=0 EndX=-8.70761 EndY=-14 EndZ=0
    g13: LineSegment StartX=-12.8401 StartY=-16 StartZ=0 EndX=-12.8401 EndY=-17.6958 EndZ=0
    g14: LineSegment StartX=-10.15 StartY=-12 StartZ=0 EndX=-7.79258 EndY=-12 EndZ=0
    g15: Circle CenterX=-6.2215 CenterY=-2 CenterZ=0 NormalX=0 NormalY=0 NormalZ=1 AngleXU=0 Radius=1
    g16: Circle CenterX=-6.22762 CenterY=-2.58724 CenterZ=0 NormalX=0 NormalY=0 NormalZ=1 AngleXU=0 Radius=1
    g17: Circle CenterX=-6.32538 CenterY=-4 CenterZ=0 NormalX=0 NormalY=0 NormalZ=1 AngleXU=0 Radius=1
    g18: BSplineCurve PolesCount=3 KnotsCount=2 Degree=2 IsPeriodic=0
    g19: GeomPoint X=-6.2215 Y=-2 Z=0
    g20: GeomPoint X=-6.32538 Y=-4 Z=0
    g21: Circle CenterX=-6.48644 CenterY=-5.99526 CenterZ=0 NormalX=0 NormalY=0 NormalZ=1 AngleXU=0 Radius=1
    g22: Circle CenterX=-6.58486 CenterY=-6.99526 CenterZ=0 NormalX=0 NormalY=0 NormalZ=1 AngleXU=0 Radius=1
    g23: Circle CenterX=-6.77343 CenterY=-8 CenterZ=0 NormalX=0 NormalY=0 NormalZ=1 AngleXU=0 Radius=1
    g24: BSplineCurve PolesCount=3 KnotsCount=2 Degree=2 IsPeriodic=0
    g25: GeomPoint X=-6.48644 Y=-5.99526 Z=0
    g26: GeomPoint X=-6.77343 Y=-8 Z=0
    g27: Circle CenterX=-7.19003 CenterY=-10 CenterZ=0 NormalX=0 NormalY=0 NormalZ=1 AngleXU=0 Radius=1
    g28: Circle CenterX=-7.44407 CenterY=-11.0915 CenterZ=0 NormalX=0 NormalY=0 NormalZ=1 AngleXU=0 Radius=1
    g29: Circle CenterX=-7.79258 CenterY=-12 CenterZ=0 NormalX=0 NormalY=0 NormalZ=1 AngleXU=0 Radius=1
    g30: BSplineCurve PolesCount=3 KnotsCount=2 Degree=2 IsPeriodic=0
    g31: GeomPoint X=-7.19003 Y=-10 Z=0
    g32: GeomPoint X=-7.79258 Y=-12 Z=0
    g33: Circle CenterX=-8.70761 CenterY=-14 CenterZ=0 NormalX=0 NormalY=0 NormalZ=1 AngleXU=0 Radius=1
    g34: Circle CenterX=-9.33087 CenterY=-15.1837 CenterZ=0 NormalX=0 NormalY=0 NormalZ=1 AngleXU=0 Radius=1
    g35: Circle CenterX=-10.1571 CenterY=-16 CenterZ=0 NormalX=0 NormalY=0 NormalZ=1 AngleXU=0 Radius=1
    g36: BSplineCurve PolesCount=3 KnotsCount=2 Degree=2 IsPeriodic=0
    g37: GeomPoint X=-8.70761 Y=-14 Z=0
    g38: GeomPoint X=-10.1571 Y=-16 Z=0
    g39: Circle CenterX=-12.8401 CenterY=-17.6958 CenterZ=0 NormalX=0 NormalY=0 NormalZ=1 AngleXU=0 Radius=1
    g40: Circle CenterX=-13.3521 CenterY=-17.9027 CenterZ=0 NormalX=0 NormalY=0 NormalZ=1 AngleXU=0 Radius=1
    g41: Circle CenterX=-14 CenterY=-18 CenterZ=0 NormalX=0 NormalY=0 NormalZ=1 AngleXU=0 Radius=1
    g42: BSplineCurve PolesCount=3 KnotsCount=2 Degree=2 IsPeriodic=0
    g43: GeomPoint X=-12.8401 Y=-17.6958 Z=0
    g44: GeomPoint X=-14 Y=-18 Z=0
    g45: LineSegment StartX=-6.2 StartY=0 StartZ=0 EndX=-7.2 EndY=0 EndZ=0
    g46: LineSegment StartX=-7.2 StartY=0 StartZ=0 EndX=-7.2 EndY=-2 EndZ=0
    g47: LineSegment StartX=-7.2 StartY=-2 StartZ=0 EndX=-6.2215 EndY=-2 EndZ=0
    g48: LineSegment StartX=-6.32538 StartY=-4 StartZ=0 EndX=-7.65538 EndY=-4 EndZ=0
    g49: LineSegment StartX=-7.65538 StartY=-4 StartZ=0 EndX=-7.65538 EndY=-5.99526 EndZ=0
    g50: LineSegment StartX=-7.65538 StartY=-5.99526 StartZ=0 EndX=-6.48644 EndY=-5.99526 EndZ=0
    g51: LineSegment StartX=-6.77343 StartY=-8 StartZ=0 EndX=-8.43343 EndY=-8 EndZ=0
    g52: LineSegment StartX=-8.43343 StartY=-8 StartZ=0 EndX=-8.43343 EndY=-10 EndZ=0
    g53: LineSegment StartX=-8.43343 StartY=-10 StartZ=0 EndX=-7.19003 EndY=-10 EndZ=0
  constraints (112):
    c: Horizontal(g0)
    c: Distance(g0) = 2
    c: Block(g0)
    c: Vertical(g1)
    c: Coincident(g2,g0)
    c: Vertical(g2)
    c: Block(g2)
    c: Coincident(g6,g2)
    c: Weight(g3) = 1
    c: Equal(g3,g4)
    c: Equal(g3,g5)
    c: InternalAlignment(g3,g6)
    c: InternalAlignment(g4,g6)
    c: InternalAlignment(g5,g6)
    c: InternalAlignment(g7,g6)
    c: InternalAlignment(g8,g6)
    c: Block(g6)
    c: Coincident(g9,g1)
    c: Coincident(g9,g6)
    c: Horizontal(g9)
    c: Vertical(g10)
    c: Block(g10)
    c: Horizontal(g11)
    c: Block(g11)
    c: Coincident(g12,g10)
    c: Horizontal(g12)
    c: Block(g12)
    c: Coincident(g13,g11)
    c: Vertical(g13)
    c: Block(g13)
    c: Coincident(g14,g10)
    c: Horizontal(g14)
    c: Block(g14)
    c: Block(g9)
    c: Block(g1)
    c: Weight(g15) = 1
    c: Equal(g15,g16)
    c: Equal(g15,g17)
    c: InternalAlignment(g15,g18)
    c: InternalAlignment(g16,g18)
    c: InternalAlignment(g17,g18)
    c: InternalAlignment(g19,g18)
    c: InternalAlignment(g20,g18)
    c: Weight(g21) = 1
    c: Equal(g21,g22)
    c: Equal(g21,g23)
    c: InternalAlignment(g21,g24)
    c: InternalAlignment(g22,g24)
    c: InternalAlignment(g23,g24)
    c: InternalAlignment(g25,g24)
    c: InternalAlignment(g26,g24)
    c: Weight(g27) = 1
    c: Equal(g27,g28)
    c: Equal(g27,g29)
    c: Coincident(g30,g14)
    c: InternalAlignment(g27,g30)
    c: InternalAlignment(g28,g30)
    c: InternalAlignment(g29,g30)
    c: InternalAlignment(g31,g30)
    c: InternalAlignment(g32,g30)
    c: Coincident(g36,g12)
    c: Weight(g33) = 1
    c: Equal(g33,g34)
    c: Equal(g33,g35)
    c: Coincident(g36,g11)
    c: InternalAlignment(g33,g36)
    c: InternalAlignment(g34,g36)
    c: InternalAlignment(g35,g36)
    c: InternalAlignment(g37,g36)
    c: InternalAlignment(g38,g36)
    c: Coincident(g42,g13)
    c: Weight(g39) = 1
    c: Equal(g39,g40)
    c: Equal(g39,g41)
    c: Coincident(g42,g1)
    c: InternalAlignment(g39,g42)
    c: InternalAlignment(g40,g42)
    c: InternalAlignment(g41,g42)
    c: InternalAlignment(g43,g42)
    c: InternalAlignment(g44,g42)
    c: Block(g18)
    c: Block(g24)
    c: Block(g30)
    c: Block(g36)
    c: Block(g42)
    c: Horizontal(g45)
    c: Coincident(g45,g0)
    c: Vertical(g46)
    c: Coincident(g46,g45)
    c: Coincident(g47,g46)
    c: Coincident(g47,g18)
    c: Horizontal(g47)
    c: Block(g46)
    c: Coincident(g48,g18)
    c: Horizontal(g48)
    c: Distance(g48) = 1.33
    c: Vertical(g49)
    c: Coincident(g49,g48)
    c: Coincident(g50,g49)
    c: Coincident(g50,g24)
    c: Horizontal(g50)
    c: Tangent(g50,g22)
    c: Horizontal(g51)
    c: Coincident(g51,g24)
    c: Block(g51)
    c: Vertical(g52)
    c: Block(g52)
    c: Coincident(g52,g51)
    c: Coincident(g53,g52)
    c: Coincident(g53,g30)
    c: Horizontal(g53)
    c: Distance(g1) = 8.5
FEATURE [Part::Feature] Face024
  shape: bbox 9.8 x 26.5 x 2e-07 mm, 1 faces, 0 solids (baked)
FEATURE [Part::Revolution] Revolve024
  Angle = 360
  Axis = (0,1,0)
  Base = (0,0,0)
  FaceMakerClass = Part::FaceMakerBullseye
  Placement = pos=(0,0,0) rot=(0,0,1;1.5708rad)
  Solid = false
  Source = -> Face024
  Symmetric = false
FEATURE [Part::Feature] Face025
  shape: bbox 9.8 x 26.5 x 2e-07 mm, 1 faces, 0 solids (baked)
FEATURE [Part::Revolution] Revolve025
  Angle = 360
  Axis = (0,1,0)
  Base = (0,0,0)
  FaceMakerClass = Part::FaceMakerBullseye
  Placement = pos=(0,0,0) rot=(0,0,1;1.5708rad)
  Solid = false
  Source = -> Face025
  Symmetric = false
FEATURE [Part::MultiFuse] Fusion033
  Placement = pos=(-18,19,36) rot=(0,0,1;0rad)
  Shapes = -> [Revolve025,Revolve024]
FEATURE [Part::Cylinder] Cylinder014
  Angle = 360
  AttacherType = Attacher::AttachEngine3D
  Height = 20
  Placement = pos=(0,0,36.15) rot=(0,0,1;0rad)
  Radius = 14.3
FEATURE [Part::Cylinder] Cylinder015
  Angle = 360
  AttacherType = Attacher::AttachEngine3D
  Height = 10
  Placement = pos=(0,0,36.15) rot=(0,0,1;0rad)
  Radius = 4
FEATURE [Part::MultiFuse] Fusion034  label="removeToCreteHoleForPlugHousing004"
  Placement = pos=(-42,19,36) rot=(0,1,0;1.5708rad)
  Shapes = -> [Cylinder014,Cylinder015]
FEATURE [Part::Cut] Cut008  label="top004"
  Base = -> Cut004
  Placement = pos=(-1,0,0) rot=(0,0,1;0rad)
  Tool = -> Fusion034
FEATURE [Part::Box] Box005  label="Cube005"
  AttacherType = Attacher::AttachEngine3D
  Height = 28
  Length = 3
  Placement = pos=(110.7,19,22) rot=(0,0,1;0rad)
  Width = 15.7
FEATURE [Part::Cylinder] Cylinder016
  Angle = 360
  AttacherType = Attacher::AttachEngine3D
  Height = 10
  Placement = pos=(0,0,36.15) rot=(0,0,1;0rad)
  Radius = 4
FEATURE [Part::Cylinder] Cylinder017
  Angle = 360
  AttacherType = Attacher::AttachEngine3D
  Height = 20
  Placement = pos=(0,0,36.15) rot=(0,0,1;0rad)
  Radius = 10.3
FEATURE [Part::MultiFuse] Fusion035  label="removeToCreteHoleForPlugHousing005"
  Placement = pos=(70,19,36) rot=(0,1,0;1.5708rad)
  Shapes = -> [Cylinder017,Cylinder016]
FEATURE [Part::Cut] Cut009  label="plugHousingTab001"
  Base = -> Box005
  Placement = pos=(-107.4,-14,0) rot=(0,0,1;0rad)
  Tool = -> Fusion035
FEATURE [Part::Box] Box006  label="Cube006"
  AttacherType = Attacher::AttachEngine3D
  Height = 28
  Length = 3
  Placement = pos=(110.7,19,22) rot=(0,0,1;0rad)
  Width = 15.7
FEATURE [Part::Cylinder] Cylinder018
  Angle = 360
  AttacherType = Attacher::AttachEngine3D
  Height = 10
  Placement = pos=(0,0,36.15) rot=(0,0,1;0rad)
  Radius = 4
FEATURE [Part::Cylinder] Cylinder019
  Angle = 360
  AttacherType = Attacher::AttachEngine3D
  Height = 20
  Placement = pos=(0,0,36.15) rot=(0,0,1;0rad)
  Radius = 10.3
FEATURE [Part::MultiFuse] Fusion036  label="removeToCreteHoleForPlugHousing006"
  Placement = pos=(70,19,36) rot=(0,1,0;1.5708rad)
  Shapes = -> [Cylinder019,Cylinder018]
FEATURE [Part::Cut] Cut010  label="plugHousingTab002"
  Base = -> Box006
  Placement = pos=(-107.4,-14,0) rot=(0,0,1;0rad)
  Tool = -> Fusion036
FEATURE [Part::MultiFuse] Fusion037
  Placement = pos=(9.6,23,0) rot=(0,0,1;3.14159rad)
  Shapes = -> [Cut009,Cut010]
FEATURE [Part::Box] Box  label="Cube"
  AttacherType = Attacher::AttachEngine3D
  Height = 10
  Length = 3
  Placement = pos=(3.3,4,12) rot=(0,0,1;0rad)
  Width = 10
FEATURE [Part::Fillet] Fillet004
  Base = -> Fusion028
  Edges = 1 edges r=2: [Edge25]
FEATURE [Part::Fillet] Fillet005  label="plugHousing046"
  Base = -> Fillet004
  Edges = 1 edges r=2: [Edge8]
FEATURE [Part::Fillet] Fillet006
  Base = -> Box
  Edges = 1 edges r=2: [Edge11]
FEATURE [Part::Box] Box007  label="Cube007"
  AttacherType = Attacher::AttachEngine3D
  Height = 10
  Length = 3
  Placement = pos=(3.3,4,50) rot=(0,0,1;0rad)
  Width = 10
FEATURE [Part::Fillet] Fillet007
  Base = -> Box007
  Edges = 1 edges r=2: [Edge12]
FEATURE [Part::Box] Box008  label="Cube008"
  AttacherType = Attacher::AttachEngine3D
  Height = 28
  Length = 4
  Placement = pos=(5,0,22) rot=(0,0,1;0rad)
  Width = 10
FEATURE [Part::Fillet] Fillet008
  Base = -> Box008
  Edges = 1 edges r=1: [Edge7]
FEATURE [Part::Fillet] Fillet009
  Base = -> Fillet008
  Edges = 1 edges r=2: [Edge5]
FEATURE [Part::Fillet] Fillet010
  Base = -> Fillet009
  Edges = 1 edges r=2: [Edge2]
FEATURE [Sketcher::SketchObject] Sketch009  label="topSketch003"
  FullyConstrained = true
  sketch-geometry (4):
    g0: LineSegment StartX=16.8446 StartY=31.512 StartZ=0 EndX=16.3251 EndY=34.4666 EndZ=0
    g1: ArcOfCircle CenterX=19 CenterY=19.2524 CenterZ=0 NormalX=0 NormalY=0 NormalZ=1 AngleXU=0 Radius=15.4476 StartAngle=1.74483 EndAngle=2.72717
    g2: ArcOfCircle CenterX=19 CenterY=19.2524 CenterZ=0 NormalX=0 NormalY=0 NormalZ=1 AngleXU=0 Radius=12.4476 StartAngle=1.74483 EndAngle=2.73189
    g3: LineSegment StartX=4.86004 StartY=25.4725 StartZ=0 EndX=7.58253 EndY=24.2107 EndZ=0
  constraints (7):
    c: Block(g0)
    c: Coincident(g1,g0)
    c: Coincident(g2,g0)
    c: Coincident(g3,g1)
    c: Coincident(g3,g2)
    c: Block(g1)
    c: Block(g2)
FEATURE [Part::Extrusion] Extrude008
  Base = -> Sketch009
  Dir = (0,0,1)
  DirMode = 2
  FaceMakerClass = Part::FaceMakerBullseye
  LengthFwd = 10
  LengthRev = 0
  Placement = pos=(0,0,31) rot=(0,0,1;0rad)
  Solid = true
  Symmetric = false
FEATURE [Part::Cylinder] Cylinder020
  Angle = 360
  AttacherType = Attacher::AttachEngine3D
  Height = 20
  Placement = pos=(0,0,36.15) rot=(0,0,1;0rad)
  Radius = 8.2
FEATURE [Part::Cylinder] Cylinder021
  Angle = 360
  AttacherType = Attacher::AttachEngine3D
  Height = 10
  Placement = pos=(0,0,36.15) rot=(0,0,1;0rad)
  Radius = 4
FEATURE [Part::MultiFuse] Fusion038  label="removeToCreteHoleForPlugHousing007"
  Placement = pos=(-42,19,36) rot=(0,1,0;1.5708rad)
  Shapes = -> [Cylinder020,Cylinder021]
FEATURE [Part::Cut] Cut011
  Base = -> Extrude008
  Tool = -> Fusion038
FEATURE [Part::Fillet] Fillet011
  Base = -> Cut011
  Edges = 1 edges r=2: [Edge1]
FEATURE [Part::Fillet] Fillet012
  Base = -> Fillet011
  Edges = 1 edges r=2.5: [Edge1]
FEATURE [Part::Fillet] Fillet013
  Base = -> Fillet012
  Edges = 1 edges r=2.5: [Edge2]
FEATURE [Part::Box] Box010  label="Cube010"
  AttacherType = Attacher::AttachEngine3D
  Height = 16
  Length = 8
  Placement = pos=(12.7,31.52,28) rot=(0,0,1;0rad)
  Width = 4
FEATURE [Sketcher::SketchObject] Sketch010  label="topSketch004"
  FullyConstrained = true
  sketch-geometry (4):
    g0: LineSegment StartX=16.8446 StartY=31.512 StartZ=0 EndX=16.3251 EndY=34.4666 EndZ=0
    g1: ArcOfCircle CenterX=19 CenterY=19.2524 CenterZ=0 NormalX=0 NormalY=0 NormalZ=1 AngleXU=0 Radius=15.4476 StartAngle=1.74483 EndAngle=2.72717
    g2: ArcOfCircle CenterX=19 CenterY=19.2524 CenterZ=0 NormalX=0 NormalY=0 NormalZ=1 AngleXU=0 Radius=12.4476 StartAngle=1.74483 EndAngle=2.73189
    g3: LineSegment StartX=4.86004 StartY=25.4725 StartZ=0 EndX=7.58253 EndY=24.2107 EndZ=0
  constraints (7):
    c: Block(g0)
    c: Coincident(g1,g0)
    c: Coincident(g2,g0)
    c: Coincident(g3,g1)
    c: Coincident(g3,g2)
    c: Block(g1)
    c: Block(g2)
FEATURE [Part::Cylinder] Cylinder022
  Angle = 360
  AttacherType = Attacher::AttachEngine3D
  Height = 10
  Placement = pos=(0,0,36.15) rot=(0,0,1;0rad)
  Radius = 4
FEATURE [Sketcher::SketchObject] Sketch011  label="topSketch005"
  FullyConstrained = true
  sketch-geometry (4):
    g0: LineSegment StartX=16.8446 StartY=31.512 StartZ=0 EndX=16.3251 EndY=34.4666 EndZ=0
    g1: ArcOfCircle CenterX=19 CenterY=19.2524 CenterZ=0 NormalX=0 NormalY=0 NormalZ=1 AngleXU=0 Radius=15.4476 StartAngle=1.74483 EndAngle=2.72717
    g2: ArcOfCircle CenterX=19 CenterY=19.2524 CenterZ=0 NormalX=0 NormalY=0 NormalZ=1 AngleXU=0 Radius=12.4476 StartAngle=1.74483 EndAngle=2.73189
    g3: LineSegment StartX=4.86004 StartY=25.4725 StartZ=0 EndX=7.58253 EndY=24.2107 EndZ=0
  constraints (7):
    c: Block(g0)
    c: Coincident(g1,g0)
    c: Coincident(g2,g0)
    c: Coincident(g3,g1)
    c: Coincident(g3,g2)
    c: Block(g1)
    c: Block(g2)
FEATURE [Part::Extrusion] Extrude010
  Base = -> Sketch011
  Dir = (0,0,1)
  DirMode = 2
  FaceMakerClass = Part::FaceMakerBullseye
  LengthFwd = 10.6
  LengthRev = 0
  Placement = pos=(0,0,31) rot=(0,0,1;0rad)
  Solid = true
  Symmetric = false
FEATURE [Part::Cylinder] Cylinder023
  Angle = 360
  AttacherType = Attacher::AttachEngine3D
  Height = 20
  Placement = pos=(0,0,36.15) rot=(0,0,1;0rad)
  Radius = 8.2
FEATURE [Part::MultiFuse] Fusion039  label="removeToCreteHoleForPlugHousing008"
  Placement = pos=(-42,19,36) rot=(0,1,0;1.5708rad)
  Shapes = -> [Cylinder023,Cylinder022]
FEATURE [Part::Cut] Cut012
  Base = -> Extrude010
  Placement = pos=(0,0,-0.3) rot=(0,0,1;0rad)
  Tool = -> Fusion039
FEATURE [Part::Cut] Cut013
  Base = -> Box010
  Tool = -> Cut012
FEATURE [Part::Fillet] Fillet014
  Base = -> Cut013
  Edges = 1 edges r=0.7: [Edge13]
FEATURE [Part::Fillet] Fillet015
  Base = -> Fillet014
  Edges = 1 edges r=0.7: [Edge13]
FEATURE [Part::Fillet] Fillet016
  Base = -> Fillet015
  Edges = 1 edges r=0.7: [Edge16]
FEATURE [Part::Fillet] Fillet017
  Base = -> Fillet016
  Edges = 1 edges r=0.7: [Edge11]
FEATURE [Part::Fillet] Fillet018
  Base = -> Fillet017
  Edges = 1 edges r=0.7: [Edge10]
FEATURE [Part::Fillet] Fillet019
  Base = -> Fillet018
  Edges = 1 edges r=1.2: [Edge5]
FEATURE [Part::Fillet] Fillet020
  Base = -> Fillet019
  Edges = 1 edges r=1.2: [Edge12]
FEATURE [Part::Fillet] Fillet021
  Base = -> Fillet020
  Edges = 1 edges r=2: [Edge1]
  Placement = pos=(0.3,0,0) rot=(0,0,1;0rad)
FEATURE [Part::MultiFuse] Fusion040  label="top005"
  Shapes = -> [Cut008,Fillet021]
FEATURE [Part::MultiFuse] Fusion041  label="wireHolder"
  Shapes = -> [Fusion033,Fillet013]
FEATURE [Part::MultiFuse] Fusion042
  Shapes = -> [Fillet007,Fusion041]
FEATURE [Part::MultiFuse] Fusion043  label="wireHolder001"
  Shapes = -> [Fusion042,Fillet010]
FEATURE [Part::MultiFuse] Fusion044  label="wireHolder002"
  Shapes = -> [Fillet006,Fusion037,Fusion043]
FEATURE [Part::Feature] Face026
  shape: bbox 11 x 6 x 2e-07 mm, 1 faces, 0 solids (baked)
FEATURE [Part::Revolution] Revolve026
  Angle = 360
  Axis = (0,1,0)
  Base = (0,0,0)
  FaceMakerClass = Part::FaceMakerBullseye
  Placement = pos=(30.3,-1,19.7) rot=(0,0,1;0rad)
  Solid = false
  Source = -> Face026
  Symmetric = false
FEATURE [Sketcher::SketchObject] Sketch013  label="topSketch006"
  FullyConstrained = true
  sketch-geometry (13):
    g0: LineSegment StartX=117 StartY=19 StartZ=0 EndX=117 EndY=38 EndZ=0
    g1: ArcOfCircle CenterX=98 CenterY=19 CenterZ=0 NormalX=0 NormalY=0 NormalZ=1 AngleXU=0 Radius=19 StartAngle=5.7297 EndAngle=6.28319
    g2: LineSegment StartX=0 StartY=3 StartZ=0 EndX=0 EndY=19 EndZ=0
    g3: LineSegment StartX=19 StartY=38 StartZ=0 EndX=117 EndY=38 EndZ=0
    g4: ArcOfCircle CenterX=19 CenterY=19 CenterZ=0 NormalX=0 NormalY=0 NormalZ=1 AngleXU=0 Radius=19 StartAngle=1.5708 EndAngle=3.14159
    g5: ArcOfCircle CenterX=19 CenterY=19 CenterZ=0 NormalX=0 NormalY=0 NormalZ=1 AngleXU=0 Radius=16 StartAngle=1.5708 EndAngle=3.14159
    g6: ArcOfCircle CenterX=98 CenterY=19 CenterZ=0 NormalX=0 NormalY=0 NormalZ=1 AngleXU=0 Radius=16 StartAngle=5.60905 EndAngle=6.28319
    g7: LineSegment StartX=114 StartY=19 StartZ=0 EndX=114 EndY=35 EndZ=0
    g8: LineSegment StartX=110.5 StartY=9.01251 StartZ=0 EndX=114.163 EndY=9.01251 EndZ=0
    g9: LineSegment StartX=114 StartY=35 StartZ=0 EndX=19 EndY=35 EndZ=0
    g10: LineSegment StartX=0 StartY=3 StartZ=0 EndX=0 EndY=0 EndZ=0
    g11: LineSegment StartX=3 StartY=0 StartZ=0 EndX=0 EndY=0 EndZ=0
    g12: LineSegment StartX=3 StartY=19 StartZ=0 EndX=3 EndY=0 EndZ=0
  constraints (33):
    c: Vertical(g0)
    c: Distance(g0) = 19
    c: Block(g0)
    c: Coincident(g1,g0)
    c: Block(g1)
    c: Vertical(g2)
    c: Block(g2)
    c: Coincident(g3,g0)
    c: Horizontal(g3)
    c: Distance(g3) = 98
    c: Coincident(g4,g3)
    c: Coincident(g4,g2)
    c: Block(g4)
    c: Coincident(g5,g4)
    c: Coincident(g6,g1)
    c: Block(g6)
    c: Block(g5)
    c: Coincident(g7,g6)
    c: Vertical(g7)
    c: Coincident(g8,g6)
    c: Coincident(g8,g1)
    c: Coincident(g9,g7)
    c: Coincident(g9,g5)
    c: Horizontal(g9)
    c: Tangent(g9,g5)
    c: Coincident(g10,g2)
    c: Distance(g10) = 3
    c: Vertical(g10)
    c: Coincident(g11,g10)
    c: Horizontal(g11)
    c: Coincident(g12,g5)
    c: Coincident(g12,g11)
    c: Vertical(g12)
FEATURE [Part::Extrusion] Extrude011  label="top006"
  Base = -> Sketch013
  Dir = (0,0,1)
  DirMode = 2
  FaceMakerClass = Part::FaceMakerBullseye
  LengthFwd = 72
  LengthRev = 0
  Solid = true
  Symmetric = false
FEATURE [Sketcher::SketchObject] Sketch014
  FullyConstrained = true
  MapMode = 3
  Placement = pos=(0,0,0) rot=(1,0,0;1.5708rad)
  Support = -> [Extrude011]
  sketch-geometry (8):
    g0: Circle CenterX=80.351 CenterY=-67.6202 CenterZ=0 NormalX=0 NormalY=0 NormalZ=1 AngleXU=0 Radius=2
    g1: Circle CenterX=80.351 CenterY=-67.6202 CenterZ=0 NormalX=0 NormalY=0 NormalZ=1 AngleXU=0 Radius=3
    g2: Circle CenterX=80.351 CenterY=-4.92017 CenterZ=0 NormalX=0 NormalY=0 NormalZ=1 AngleXU=0 Radius=2
    g3: Circle CenterX=80.351 CenterY=-4.92017 CenterZ=0 NormalX=0 NormalY=0 NormalZ=1 AngleXU=0 Radius=3
    g4: Circle CenterX=23.851 CenterY=-4.92017 CenterZ=0 NormalX=0 NormalY=0 NormalZ=1 AngleXU=0 Radius=2
    g5: Circle CenterX=23.851 CenterY=-4.92017 CenterZ=0 NormalX=0 NormalY=0 NormalZ=1 AngleXU=0 Radius=3
    g6: Circle CenterX=23.851 CenterY=-67.6202 CenterZ=0 NormalX=0 NormalY=0 NormalZ=1 AngleXU=0 Radius=2
    g7: Circle CenterX=23.851 CenterY=-67.6202 CenterZ=0 NormalX=0 NormalY=0 NormalZ=1 AngleXU=0 Radius=3
  constraints (8):
    c: Block(g3)
    c: Block(g2)
    c: Block(g1)
    c: Block(g0)
    c: Block(g6)
    c: Block(g7)
    c: Block(g4)
    c: Block(g5)
FEATURE [Part::Feature] Face027
  shape: bbox 11 x 6 x 2e-07 mm, 1 faces, 0 solids (baked)
FEATURE [Part::Revolution] Revolve027
  Angle = 360
  Axis = (0,1,0)
  Base = (0,0,0)
  FaceMakerClass = Part::FaceMakerBullseye
  Placement = pos=(30.3,-1,51.7) rot=(0,0,1;0rad)
  Solid = false
  Source = -> Face027
  Symmetric = false
FEATURE [Part::Feature] Face028
  shape: bbox 11 x 6 x 2e-07 mm, 1 faces, 0 solids (baked)
FEATURE [Part::Revolution] Revolve028
  Angle = 360
  Axis = (0,1,0)
  Base = (0,0,0)
  FaceMakerClass = Part::FaceMakerBullseye
  Placement = pos=(62.3,-1,19.7) rot=(0,0,1;0rad)
  Solid = false
  Source = -> Face028
  Symmetric = false
FEATURE [Part::Feature] Face029
  shape: bbox 11 x 6 x 2e-07 mm, 1 faces, 0 solids (baked)
FEATURE [Part::Revolution] Revolve029
  Angle = 360
  Axis = (0,1,0)
  Base = (0,0,0)
  FaceMakerClass = Part::FaceMakerBullseye
  Placement = pos=(62.3,-1,51.7) rot=(0,0,1;0rad)
  Solid = false
  Source = -> Face029
  Symmetric = false
FEATURE [Part::Feature] Wire
  shape: bbox 11 x 5.2 x 2e-07 mm, 0 faces, 0 solids (baked)
FEATURE [Part::Revolution] Revolve030
  Angle = 360
  Axis = (0,1,0)
  Base = (0,0,0)
  FaceMakerClass = Part::FaceMakerBullseye
  Placement = pos=(30.3,38,19.7) rot=(0,0,1;0rad)
  Solid = true
  Source = -> Wire
  Symmetric = false
FEATURE [Part::Feature] Wire001
  shape: bbox 11 x 5.2 x 2e-07 mm, 0 faces, 0 solids (baked)
FEATURE [Part::Revolution] Revolve031
  Angle = 360
  Axis = (0,1,0)
  Base = (0,0,0)
  FaceMakerClass = Part::FaceMakerBullseye
  Placement = pos=(30.3,38,51.7) rot=(0,0,1;0rad)
  Solid = true
  Source = -> Wire001
  Symmetric = false
FEATURE [Part::Feature] Wire002
  shape: bbox 11 x 5.2 x 2e-07 mm, 0 faces, 0 solids (baked)
FEATURE [Part::Revolution] Revolve032
  Angle = 360
  Axis = (0,1,0)
  Base = (0,0,0)
  FaceMakerClass = Part::FaceMakerBullseye
  Placement = pos=(62.3,38,51.7) rot=(0,0,1;0rad)
  Solid = true
  Source = -> Wire002
  Symmetric = false
FEATURE [Part::Feature] Wire003
  shape: bbox 11 x 5.2 x 2e-07 mm, 0 faces, 0 solids (baked)
FEATURE [Part::Revolution] Revolve033
  Angle = 360
  Axis = (0,1,0)
  Base = (0,0,0)
  FaceMakerClass = Part::FaceMakerBullseye
  Placement = pos=(62.3,38,19.7) rot=(0,0,1;0rad)
  Solid = true
  Source = -> Wire003
  Symmetric = false
FEATURE [Part::MultiFuse] Fusion045  label="altRandScrewHousing"
  Shapes = -> [Revolve029,Revolve027,Revolve028,Revolve026]
FEATURE [Part::MultiFuse] Fusion046  label="fanScrewHousing"
  Shapes = -> [Revolve033,Revolve032,Revolve031,Revolve030]
FEATURE [Sketcher::SketchObject] Sketch015
  FullyConstrained = true
  sketch-geometry (17):
    g0: Circle CenterX=-3.5 CenterY=23.5 CenterZ=0 NormalX=0 NormalY=0 NormalZ=1 AngleXU=0 Radius=1
    g1: Circle CenterX=-1 CenterY=15.25 CenterZ=0 NormalX=0 NormalY=0 NormalZ=1 AngleXU=0 Radius=1
    g2: Circle CenterX=-3.5 CenterY=7 CenterZ=0 NormalX=0 NormalY=0 NormalZ=1 AngleXU=0 Radius=1
    g3: BSplineCurve PolesCount=3 KnotsCount=2 Degree=2 IsPeriodic=0
    g4: GeomPoint X=-3.5 Y=23.5 Z=0
    g5: GeomPoint X=-3.5 Y=7 Z=0
    g6: Circle CenterX=-4.8 CenterY=30.5 CenterZ=0 NormalX=0 NormalY=0 NormalZ=1 AngleXU=0 Radius=1
    g7: Circle CenterX=-3.5 CenterY=30.5 CenterZ=0 NormalX=0 NormalY=0 NormalZ=1 AngleXU=0 Radius=1
    g8: Circle CenterX=-3.5 CenterY=29.2 CenterZ=0 NormalX=0 NormalY=0 NormalZ=1 AngleXU=0 Radius=1
    g9: BSplineCurve PolesCount=3 KnotsCount=2 Degree=2 IsPeriodic=0
    g10: GeomPoint X=-4.8 Y=30.5 Z=0
    g11: GeomPoint X=-3.5 Y=29.2 Z=0
    g12: LineSegment StartX=-3.5 StartY=29.2 StartZ=0 EndX=-3.5 EndY=23.5 EndZ=0
    g13: LineSegment StartX=-4.8 StartY=30.5 StartZ=0 EndX=0 EndY=30.5 EndZ=0
    g14: LineSegment StartX=-3.5 StartY=0.3 StartZ=0 EndX=0 EndY=0.3 EndZ=0
    g15: LineSegment StartX=-3.5 StartY=0.3 StartZ=0 EndX=-3.5 EndY=7 EndZ=0
    g16: LineSegment StartX=0 StartY=0.3 StartZ=0 EndX=0 EndY=30.5 EndZ=0
  constraints (33):
    c: Weight(g0) = 1
    c: Equal(g0,g1)
    c: Equal(g0,g2)
    c: InternalAlignment(g0,g3)
    c: InternalAlignment(g1,g3)
    c: InternalAlignment(g2,g3)
    c: InternalAlignment(g4,g3)
    c: InternalAlignment(g5,g3)
    c: Block(g3)
    c: Weight(g6) = 1
    c: Equal(g6,g7)
    c: Equal(g6,g8)
    c: InternalAlignment(g6,g9)
    c: InternalAlignment(g7,g9)
    c: InternalAlignment(g8,g9)
    c: InternalAlignment(g10,g9)
    c: InternalAlignment(g11,g9)
    c: Block(g9)
    c: Coincident(g12,g9)
    c: Coincident(g12,g3)
    c: Vertical(g12)
    c: Coincident(g13,g9)
    c: Horizontal(g13)
    c: Distance(g13) = 4.8
    c: Horizontal(g14)
    c: Block(g14)
    c: Coincident(g15,g14)
    c: Coincident(g15,g3)
    c: Vertical(g15)
    c: Coincident(g16,g14)
    c: Coincident(g16,g13)
    c: Vertical(g16)
    c: Tangent(g16,g1)
FEATURE [Sketcher::SketchObject] Sketch016
  FullyConstrained = true
  sketch-geometry (16):
    g0: Circle CenterX=-3.5 CenterY=23.5 CenterZ=0 NormalX=0 NormalY=0 NormalZ=1 AngleXU=0 Radius=1
    g1: Circle CenterX=-1 CenterY=15.25 CenterZ=0 NormalX=0 NormalY=0 NormalZ=1 AngleXU=0 Radius=1
    g2: Circle CenterX=-3.5 CenterY=7 CenterZ=0 NormalX=0 NormalY=0 NormalZ=1 AngleXU=0 Radius=1
    g3: BSplineCurve PolesCount=3 KnotsCount=2 Degree=2 IsPeriodic=0
    g4: GeomPoint X=-3.5 Y=23.5 Z=0
    g5: GeomPoint X=-3.5 Y=7 Z=0
    g6: LineSegment StartX=-3.5 StartY=28.2 StartZ=0 EndX=-3.5 EndY=23.5 EndZ=0
    g7: LineSegment StartX=0 StartY=29.5 StartZ=0 EndX=0 EndY=30 EndZ=0
    g8: LineSegment StartX=-3.5 StartY=28.2 StartZ=0 EndX=-3.5 EndY=30 EndZ=0
    g9: LineSegment StartX=0 StartY=30 StartZ=0 EndX=0 EndY=30.5 EndZ=0
    g10: LineSegment StartX=0 StartY=30.5 StartZ=0 EndX=-3.5 EndY=30.5 EndZ=0
    g11: LineSegment StartX=-3.5 StartY=30.5 StartZ=0 EndX=-3.5 EndY=30 EndZ=0
    g12: LineSegment StartX=0 StartY=29.5 StartZ=0 EndX=0 EndY=5 EndZ=0
    g13: LineSegment StartX=-3.5 StartY=0.3 StartZ=0 EndX=-3.5 EndY=7 EndZ=0
    g14: LineSegment StartX=-3.5 StartY=0.3 StartZ=0 EndX=0 EndY=0.3 EndZ=0
    g15: LineSegment StartX=0 StartY=5 StartZ=0 EndX=0 EndY=0.3 EndZ=0
  constraints (39):
    c: Weight(g0) = 1
    c: Equal(g0,g1)
    c: Equal(g0,g2)
    c: InternalAlignment(g0,g3)
    c: InternalAlignment(g1,g3)
    c: InternalAlignment(g2,g3)
    c: InternalAlignment(g4,g3)
    c: InternalAlignment(g5,g3)
    c: Block(g3)
    c: Coincident(g6,g3)
    c: Vertical(g6)
    c: Vertical(g7)
    c: Distance(g7) = 0.5
    c: Coincident(g8,g6)
    c: Vertical(g8)
    c: Block(g6)
    c: Block(g7)
    c: Vertical(g9)
    c: Equal(g7,g9) = 0.5
    c: Block(g9)
    c: Coincident(g9,g7)
    c: Horizontal(g10)
    c: Coincident(g10,g9)
    c: Coincident(g11,g10)
    c: Coincident(g11,g8)
    c: Vertical(g11)
    c: Block(g11)
    c: Coincident(g12,g7)
    c: Vertical(g12)
    c: Coincident(g13,g3)
    c: Vertical(g13)
    c: Distance(g13) = 6.7
    c: Coincident(g14,g13)
    c: Horizontal(g14)
    c: Block(g14)
    c: Coincident(g15,g12)
    c: Coincident(g15,g14)
    c: Vertical(g15)
    c: Block(g15)
FEATURE [Sketcher::SketchObject] Sketch017
  FullyConstrained = true
  sketch-geometry (11):
    g0: LineSegment StartX=-3.5 StartY=1e-16 StartZ=0 EndX=-1.6 EndY=1e-16 EndZ=0
    g1: LineSegment StartX=-1.6 StartY=1e-16 StartZ=0 EndX=-1.6 EndY=1.5 EndZ=0
    g2: LineSegment StartX=-3.5 StartY=1.5 StartZ=0 EndX=-1.6 EndY=1.5 EndZ=0
    g3: LineSegment StartX=-3.5 StartY=1e-16 StartZ=0 EndX=-4.8 EndY=1e-16 EndZ=0
    g4: Circle CenterX=-3.5 CenterY=1.3 CenterZ=0 NormalX=0 NormalY=0 NormalZ=1 AngleXU=0 Radius=1
    g5: Circle CenterX=-3.5 CenterY=1e-16 CenterZ=0 NormalX=0 NormalY=0 NormalZ=1 AngleXU=0 Radius=1
    g6: Circle CenterX=-4.8 CenterY=1e-16 CenterZ=0 NormalX=0 NormalY=0 NormalZ=1 AngleXU=0 Radius=1
    g7: BSplineCurve PolesCount=3 KnotsCount=2 Degree=2 IsPeriodic=0
    g8: GeomPoint X=-3.5 Y=1.3 Z=0
    g9: GeomPoint X=-4.8 Y=1e-16 Z=0
    g10: LineSegment StartX=-3.5 StartY=1.3 StartZ=0 EndX=-3.5 EndY=1.5 EndZ=0
  constraints (24):
    c: Horizontal(g0)
    c: Distance(g0) = 1.9
    c: Block(g0)
    c: Coincident(g1,g0)
    c: Vertical(g1)
    c: Coincident(g2,g1)
    c: Horizontal(g2)
    c: Coincident(g3,g0)
    c: Horizontal(g3)
    c: Distance(g3) = 1.3
    c: Weight(g4) = 1
    c: Equal(g4,g5)
    c: Coincident(g5,g0)
    c: Equal(g4,g6)
    c: Coincident(g7,g3)
    c: InternalAlignment(g4,g7)
    c: InternalAlignment(g5,g7)
    c: InternalAlignment(g6,g7)
    c: InternalAlignment(g8,g7)
    c: InternalAlignment(g9,g7)
    c: Coincident(g10,g7)
    c: Coincident(g10,g2)
    c: Vertical(g10)
    c: Block(g10)
FEATURE [Part::Feature] Face035
  shape: bbox 3.2 x 1.5 x 2e-07 mm, 1 faces, 0 solids (baked)
FEATURE [Part::Revolution] Revolve039  label="backCaseScrewRetainer"
  Angle = 360
  Axis = (0,1,0)
  Base = (0,0,0)
  FaceMakerClass = Part::FaceMakerBullseye
  Placement = pos=(12.5,3,62) rot=(0,0,1;0rad)
  Solid = false
  Source = -> Face035
  Symmetric = false
FEATURE [Part::Feature] Face036
  shape: bbox 3.2 x 1.5 x 2e-07 mm, 1 faces, 0 solids (baked)
FEATURE [Part::Feature] Face039
  shape: bbox 4.8 x 30.2 x 2e-07 mm, 1 faces, 0 solids (baked)
FEATURE [Part::Revolution] Revolve043  label="frontCaseScrewPost002"
  Angle = 360
  Axis = (0,1,0)
  Base = (0,0,0)
  FaceMakerClass = Part::FaceMakerBullseye
  Placement = pos=(89.5,4.5,3.5) rot=(0,0,1;0rad)
  Solid = false
  Source = -> Face039
  Symmetric = false
FEATURE [Part::Feature] Face042
  shape: bbox 4.8 x 30.2 x 2e-07 mm, 1 faces, 0 solids (baked)
FEATURE [Part::Revolution] Revolve046  label="frontCaseScrewPost003"
  Angle = 360
  Axis = (0,1,0)
  Base = (0,0,0)
  FaceMakerClass = Part::FaceMakerBullseye
  Placement = pos=(89.5,4.5,68.5) rot=(0,0,1;0rad)
  Solid = false
  Source = -> Face042
  Symmetric = false
FEATURE [Part::Feature] Face043
  shape: bbox 3.2 x 1.5 x 2e-07 mm, 1 faces, 0 solids (baked)
FEATURE [Part::Revolution] Revolve047  label="frontCaseScrewRetainer002"
  Angle = 360
  Axis = (0,1,0)
  Base = (0,0,0)
  FaceMakerClass = Part::FaceMakerBullseye
  Placement = pos=(89.5,3,68.5) rot=(0,0,1;0rad)
  Solid = false
  Source = -> Face043
  Symmetric = false
FEATURE [Part::Feature] Face044
  shape: bbox 3.2 x 1.5 x 2e-07 mm, 1 faces, 0 solids (baked)
FEATURE [Part::Revolution] Revolve048  label="frontCaseScrewRetainer003"
  Angle = 360
  Axis = (0,1,0)
  Base = (0,0,0)
  FaceMakerClass = Part::FaceMakerBullseye
  Placement = pos=(89.5,3,3.5) rot=(0,0,1;0rad)
  Solid = false
  Source = -> Face044
  Symmetric = false
FEATURE [App::MeasureDistance] Distance002  label="Distance: 1.67 mm"
  Distance = 1.66921
  P1 = (99.2361,4.7524,71.7)
  P2 = (99.2347,6.42161,71.7)
FEATURE [Sketcher::SketchObject] Sketch018
  FullyConstrained = true
  sketch-geometry (7):
    g0: LineSegment StartX=0 StartY=0 StartZ=0 EndX=0 EndY=6 EndZ=0
    g1: Circle CenterX=0 CenterY=0 CenterZ=0 NormalX=0 NormalY=0 NormalZ=1 AngleXU=0 Radius=1
    g2: Circle CenterX=8 CenterY=6 CenterZ=0 NormalX=0 NormalY=0 NormalZ=1 AngleXU=0 Radius=1
    g3: BSplineCurve PolesCount=3 KnotsCount=2 Degree=2 IsPeriodic=0
    g4: GeomPoint X=0 Y=0 Z=0
    g5: GeomPoint X=8 Y=6 Z=0
    g6: LineSegment StartX=0 StartY=6 StartZ=0 EndX=8 EndY=6 EndZ=0
  constraints (14):
    c: Coincident(g0,g-1)
    c: Distance(g0) = 6
    c: Vertical(g0)
    c: Coincident(g3,g0)
    c: Weight(g1) = 1
    c: Equal(g1,g2)
    c: InternalAlignment(g1,g3)
    c: InternalAlignment(g2,g3)
    c: InternalAlignment(g4,g3)
    c: InternalAlignment(g5,g3)
    c: Block(g3)
    c: Coincident(g6,g0)
    c: Coincident(g6,g3)
    c: Horizontal(g6)
FEATURE [Part::Extrusion] Extrude012  label="caseScrewPillarBracket"
  Base = -> Sketch018
  Dir = (0,0,1)
  DirMode = 2
  FaceMakerClass = Part::FaceMakerBullseye
  LengthFwd = 2.4
  LengthRev = 0
  Placement = pos=(15.76,29,8.8) rot=(0,1,0;0rad)
  Solid = true
  Symmetric = false
FEATURE [Sketcher::SketchObject] Sketch019
  FullyConstrained = true
  sketch-geometry (7):
    g0: LineSegment StartX=0 StartY=0 StartZ=0 EndX=0 EndY=6 EndZ=0
    g1: Circle CenterX=0 CenterY=0 CenterZ=0 NormalX=0 NormalY=0 NormalZ=1 AngleXU=0 Radius=1
    g2: Circle CenterX=8 CenterY=6 CenterZ=0 NormalX=0 NormalY=0 NormalZ=1 AngleXU=0 Radius=1
    g3: BSplineCurve PolesCount=3 KnotsCount=2 Degree=2 IsPeriodic=0
    g4: GeomPoint X=0 Y=0 Z=0
    g5: GeomPoint X=8 Y=6 Z=0
    g6: LineSegment StartX=0 StartY=6 StartZ=0 EndX=8 EndY=6 EndZ=0
  constraints (14):
    c: Coincident(g0,g-1)
    c: Distance(g0) = 6
    c: Vertical(g0)
    c: Coincident(g3,g0)
    c: Weight(g1) = 1
    c: Equal(g1,g2)
    c: InternalAlignment(g1,g3)
    c: InternalAlignment(g2,g3)
    c: InternalAlignment(g4,g3)
    c: InternalAlignment(g5,g3)
    c: Block(g3)
    c: Coincident(g6,g0)
    c: Coincident(g6,g3)
    c: Horizontal(g6)
FEATURE [Part::Extrusion] Extrude013  label="caseScrewPillarBracket001"
  Base = -> Sketch019
  Dir = (0,0,1)
  DirMode = 2
  FaceMakerClass = Part::FaceMakerBullseye
  LengthFwd = 2.4
  LengthRev = 0
  Placement = pos=(15.76,29,60.8) rot=(0,0,1;0rad)
  Solid = true
  Symmetric = false
FEATURE [Sketcher::SketchObject] Sketch020
  FullyConstrained = true
  sketch-geometry (7):
    g0: LineSegment StartX=0 StartY=0 StartZ=0 EndX=0 EndY=6 EndZ=0
    g1: Circle CenterX=0 CenterY=0 CenterZ=0 NormalX=0 NormalY=0 NormalZ=1 AngleXU=0 Radius=1
    g2: Circle CenterX=8 CenterY=6 CenterZ=0 NormalX=0 NormalY=0 NormalZ=1 AngleXU=0 Radius=1
    g3: BSplineCurve PolesCount=3 KnotsCount=2 Degree=2 IsPeriodic=0
    g4: GeomPoint X=0 Y=0 Z=0
    g5: GeomPoint X=8 Y=6 Z=0
    g6: LineSegment StartX=0 StartY=6 StartZ=0 EndX=8 EndY=6 EndZ=0
  constraints (14):
    c: Coincident(g0,g-1)
    c: Distance(g0) = 6
    c: Vertical(g0)
    c: Coincident(g3,g0)
    c: Weight(g1) = 1
    c: Equal(g1,g2)
    c: InternalAlignment(g1,g3)
    c: InternalAlignment(g2,g3)
    c: InternalAlignment(g4,g3)
    c: InternalAlignment(g5,g3)
    c: Block(g3)
    c: Coincident(g6,g0)
    c: Coincident(g6,g3)
    c: Horizontal(g6)
FEATURE [Part::Extrusion] Extrude014  label="caseScrewPillarBracket002"
  Base = -> Sketch020
  Dir = (0,0,1)
  DirMode = 2
  FaceMakerClass = Part::FaceMakerBullseye
  LengthFwd = 2.4
  LengthRev = 0
  Placement = pos=(13.7,29,13.26) rot=(0,-1,0;1.5708rad)
  Solid = true
  Symmetric = false
FEATURE [Sketcher::SketchObject] Sketch021
  FullyConstrained = true
  sketch-geometry (7):
    g0: LineSegment StartX=0 StartY=0 StartZ=0 EndX=0 EndY=6 EndZ=0
    g1: Circle CenterX=0 CenterY=0 CenterZ=0 NormalX=0 NormalY=0 NormalZ=1 AngleXU=0 Radius=1
    g2: Circle CenterX=8 CenterY=6 CenterZ=0 NormalX=0 NormalY=0 NormalZ=1 AngleXU=0 Radius=1
    g3: BSplineCurve PolesCount=3 KnotsCount=2 Degree=2 IsPeriodic=0
    g4: GeomPoint X=0 Y=0 Z=0
    g5: GeomPoint X=8 Y=6 Z=0
    g6: LineSegment StartX=0 StartY=6 StartZ=0 EndX=8 EndY=6 EndZ=0
  constraints (14):
    c: Coincident(g0,g-1)
    c: Distance(g0) = 6
    c: Vertical(g0)
    c: Coincident(g3,g0)
    c: Weight(g1) = 1
    c: Equal(g1,g2)
    c: InternalAlignment(g1,g3)
    c: InternalAlignment(g2,g3)
    c: InternalAlignment(g4,g3)
    c: InternalAlignment(g5,g3)
    c: Block(g3)
    c: Coincident(g6,g0)
    c: Coincident(g6,g3)
    c: Horizontal(g6)
FEATURE [Part::Extrusion] Extrude015  label="caseScrewPillarBracket003"
  Base = -> Sketch021
  Dir = (0,0,1)
  DirMode = 2
  FaceMakerClass = Part::FaceMakerBullseye
  LengthFwd = 2.4
  LengthRev = 0
  Placement = pos=(11.3,29,58.74) rot=(0,1,0;1.5708rad)
  Solid = true
  Symmetric = false
FEATURE [Sketcher::SketchObject] Sketch022
  FullyConstrained = true
  sketch-geometry (7):
    g0: LineSegment StartX=0 StartY=0 StartZ=0 EndX=0 EndY=6 EndZ=0
    g1: Circle CenterX=0 CenterY=0 CenterZ=0 NormalX=0 NormalY=0 NormalZ=1 AngleXU=0 Radius=1
    g2: Circle CenterX=8 CenterY=6 CenterZ=0 NormalX=0 NormalY=0 NormalZ=1 AngleXU=0 Radius=1
    g3: BSplineCurve PolesCount=3 KnotsCount=2 Degree=2 IsPeriodic=0
    g4: GeomPoint X=0 Y=0 Z=0
    g5: GeomPoint X=8 Y=6 Z=0
    g6: LineSegment StartX=0 StartY=6 StartZ=0 EndX=8 EndY=6 EndZ=0
  constraints (14):
    c: Coincident(g0,g-1)
    c: Distance(g0) = 6
    c: Vertical(g0)
    c: Coincident(g3,g0)
    c: Weight(g1) = 1
    c: Equal(g1,g2)
    c: InternalAlignment(g1,g3)
    c: InternalAlignment(g2,g3)
    c: InternalAlignment(g4,g3)
    c: InternalAlignment(g5,g3)
    c: Block(g3)
    c: Coincident(g6,g0)
    c: Coincident(g6,g3)
    c: Horizontal(g6)
FEATURE [Part::Extrusion] Extrude016  label="caseScrewPillarBracket004"
  Base = -> Sketch022
  Dir = (0,0,1)
  DirMode = 2
  FaceMakerClass = Part::FaceMakerBullseye
  LengthFwd = 2.4
  LengthRev = 0
  Placement = pos=(88.3,29,65.23) rot=(0,1,0;1.5708rad)
  Solid = true
  Symmetric = false
FEATURE [Sketcher::SketchObject] Sketch023
  FullyConstrained = true
  sketch-geometry (7):
    g0: LineSegment StartX=0 StartY=0 StartZ=0 EndX=0 EndY=6 EndZ=0
    g1: Circle CenterX=0 CenterY=0 CenterZ=0 NormalX=0 NormalY=0 NormalZ=1 AngleXU=0 Radius=1
    g2: Circle CenterX=8 CenterY=6 CenterZ=0 NormalX=0 NormalY=0 NormalZ=1 AngleXU=0 Radius=1
    g3: BSplineCurve PolesCount=3 KnotsCount=2 Degree=2 IsPeriodic=0
    g4: GeomPoint X=0 Y=0 Z=0
    g5: GeomPoint X=8 Y=6 Z=0
    g6: LineSegment StartX=0 StartY=6 StartZ=0 EndX=8 EndY=6 EndZ=0
  constraints (14):
    c: Coincident(g0,g-1)
    c: Distance(g0) = 6
    c: Vertical(g0)
    c: Coincident(g3,g0)
    c: Weight(g1) = 1
    c: Equal(g1,g2)
    c: InternalAlignment(g1,g3)
    c: InternalAlignment(g2,g3)
    c: InternalAlignment(g4,g3)
    c: InternalAlignment(g5,g3)
    c: Block(g3)
    c: Coincident(g6,g0)
    c: Coincident(g6,g3)
    c: Horizontal(g6)
FEATURE [Part::Extrusion] Extrude017  label="caseScrewPillarBracket005"
  Base = -> Sketch023
  Dir = (0,0,1)
  DirMode = 2
  FaceMakerClass = Part::FaceMakerBullseye
  LengthFwd = 2.4
  LengthRev = 0
  Placement = pos=(90.7,29,6.77) rot=(0,-1,0;1.5708rad)
  Solid = true
  Symmetric = false
FEATURE [Sketcher::SketchObject] Sketch024
  FullyConstrained = true
  sketch-geometry (7):
    g0: LineSegment StartX=0 StartY=0 StartZ=0 EndX=0 EndY=6 EndZ=0
    g1: Circle CenterX=0 CenterY=0 CenterZ=0 NormalX=0 NormalY=0 NormalZ=1 AngleXU=0 Radius=1
    g2: Circle CenterX=8 CenterY=6 CenterZ=0 NormalX=0 NormalY=0 NormalZ=1 AngleXU=0 Radius=1
    g3: BSplineCurve PolesCount=3 KnotsCount=2 Degree=2 IsPeriodic=0
    g4: GeomPoint X=0 Y=0 Z=0
    g5: GeomPoint X=8 Y=6 Z=0
    g6: LineSegment StartX=0 StartY=6 StartZ=0 EndX=8 EndY=6 EndZ=0
  constraints (14):
    c: Coincident(g0,g-1)
    c: Distance(g0) = 6
    c: Vertical(g0)
    c: Coincident(g3,g0)
    c: Weight(g1) = 1
    c: Equal(g1,g2)
    c: InternalAlignment(g1,g3)
    c: InternalAlignment(g2,g3)
    c: InternalAlignment(g4,g3)
    c: InternalAlignment(g5,g3)
    c: Block(g3)
    c: Coincident(g6,g0)
    c: Coincident(g6,g3)
    c: Horizontal(g6)
FEATURE [Part::Extrusion] Extrude018  label="caseScrewPillarBracket006"
  Base = -> Sketch024
  Dir = (0,0,1)
  DirMode = 2
  FaceMakerClass = Part::FaceMakerBullseye
  LengthFwd = 2.4
  LengthRev = 0
  Placement = pos=(103.7,29,6.77) rot=(0,-1,0;1.5708rad)
  Solid = true
  Symmetric = false
FEATURE [Sketcher::SketchObject] Sketch025
  FullyConstrained = true
  sketch-geometry (7):
    g0: LineSegment StartX=0 StartY=0 StartZ=0 EndX=0 EndY=6 EndZ=0
    g1: Circle CenterX=0 CenterY=0 CenterZ=0 NormalX=0 NormalY=0 NormalZ=1 AngleXU=0 Radius=1
    g2: Circle CenterX=8 CenterY=6 CenterZ=0 NormalX=0 NormalY=0 NormalZ=1 AngleXU=0 Radius=1
    g3: BSplineCurve PolesCount=3 KnotsCount=2 Degree=2 IsPeriodic=0
    g4: GeomPoint X=0 Y=0 Z=0
    g5: GeomPoint X=8 Y=6 Z=0
    g6: LineSegment StartX=0 StartY=6 StartZ=0 EndX=8 EndY=6 EndZ=0
  constraints (14):
    c: Coincident(g0,g-1)
    c: Distance(g0) = 6
    c: Vertical(g0)
    c: Coincident(g3,g0)
    c: Weight(g1) = 1
    c: Equal(g1,g2)
    c: InternalAlignment(g1,g3)
    c: InternalAlignment(g2,g3)
    c: InternalAlignment(g4,g3)
    c: InternalAlignment(g5,g3)
    c: Block(g3)
    c: Coincident(g6,g0)
    c: Coincident(g6,g3)
    c: Horizontal(g6)
FEATURE [Part::Extrusion] Extrude019  label="caseScrewPillarBracket007"
  Base = -> Sketch025
  Dir = (0,0,1)
  DirMode = 2
  FaceMakerClass = Part::FaceMakerBullseye
  LengthFwd = 2.4
  LengthRev = 0
  Placement = pos=(101.3,29,65.23) rot=(0,1,0;1.5708rad)
  Solid = true
  Symmetric = false
FEATURE [Part::Box] Box011  label="frontCaseScrewPillarBracket"
  AttacherType = Attacher::AttachEngine3D
  Height = 2.4
  Length = 16
  Placement = pos=(87,28,2.3) rot=(0,0,1;0rad)
  Width = 7
FEATURE [Part::Box] Box012  label="frontCaseScrewPillarBracket001"
  AttacherType = Attacher::AttachEngine3D
  Height = 2.4
  Length = 16
  Placement = pos=(87,28,67.3) rot=(0,0,1;0rad)
  Width = 7
FEATURE [Sketcher::SketchObject] Sketch026
  FullyConstrained = true
  sketch-geometry (17):
    g0: Circle CenterX=-3.5 CenterY=23.5 CenterZ=0 NormalX=0 NormalY=0 NormalZ=1 AngleXU=0 Radius=1
    g1: Circle CenterX=-1 CenterY=15.25 CenterZ=0 NormalX=0 NormalY=0 NormalZ=1 AngleXU=0 Radius=1
    g2: Circle CenterX=-3.5 CenterY=7 CenterZ=0 NormalX=0 NormalY=0 NormalZ=1 AngleXU=0 Radius=1
    g3: BSplineCurve PolesCount=3 KnotsCount=2 Degree=2 IsPeriodic=0
    g4: GeomPoint X=-3.5 Y=23.5 Z=0
    g5: GeomPoint X=-3.5 Y=7 Z=0
    g6: Circle CenterX=-4.8 CenterY=30.5 CenterZ=0 NormalX=0 NormalY=0 NormalZ=1 AngleXU=0 Radius=1
    g7: Circle CenterX=-3.5 CenterY=30.5 CenterZ=0 NormalX=0 NormalY=0 NormalZ=1 AngleXU=0 Radius=1
    g8: Circle CenterX=-3.5 CenterY=29.2 CenterZ=0 NormalX=0 NormalY=0 NormalZ=1 AngleXU=0 Radius=1
    g9: BSplineCurve PolesCount=3 KnotsCount=2 Degree=2 IsPeriodic=0
    g10: GeomPoint X=-4.8 Y=30.5 Z=0
    g11: GeomPoint X=-3.5 Y=29.2 Z=0
    g12: LineSegment StartX=-3.5 StartY=29.2 StartZ=0 EndX=-3.5 EndY=23.5 EndZ=0
    g13: LineSegment StartX=-4.8 StartY=30.5 StartZ=0 EndX=0 EndY=30.5 EndZ=0
    g14: LineSegment StartX=-3.5 StartY=5 StartZ=0 EndX=-3.5 EndY=7 EndZ=0
    g15: LineSegment StartX=0 StartY=5 StartZ=0 EndX=0 EndY=30.5 EndZ=0
    g16: LineSegment StartX=-3.5 StartY=5 StartZ=0 EndX=0 EndY=5 EndZ=0
  constraints (33):
    c: Weight(g0) = 1
    c: Equal(g0,g1)
    c: Equal(g0,g2)
    c: InternalAlignment(g0,g3)
    c: InternalAlignment(g1,g3)
    c: InternalAlignment(g2,g3)
    c: InternalAlignment(g4,g3)
    c: InternalAlignment(g5,g3)
    c: Block(g3)
    c: Weight(g6) = 1
    c: Equal(g6,g7)
    c: Equal(g6,g8)
    c: InternalAlignment(g6,g9)
    c: InternalAlignment(g7,g9)
    c: InternalAlignment(g8,g9)
    c: InternalAlignment(g10,g9)
    c: InternalAlignment(g11,g9)
    c: Block(g9)
    c: Coincident(g12,g9)
    c: Coincident(g12,g3)
    c: Vertical(g12)
    c: Coincident(g13,g9)
    c: Horizontal(g13)
    c: Distance(g13) = 4.8
    c: Coincident(g14,g3)
    c: Vertical(g14)
    c: Coincident(g15,g13)
    c: Vertical(g15)
    c: Tangent(g15,g1)
    c: Distance(g14) = 2
    c: Coincident(g16,g14)
    c: Horizontal(g16)
    c: Coincident(g15,g16)
FEATURE [Part::Feature] Face050
  shape: bbox 4.8 x 25.5 x 2e-07 mm, 1 faces, 0 solids (baked)
FEATURE [Part::Revolution] Revolve054  label="moreFrontCaseScrewPost001"
  Angle = 360
  Axis = (0,1,0)
  Base = (0,0,0)
  FaceMakerClass = Part::FaceMakerBullseye
  Placement = pos=(102.5,4.5,3.5) rot=(0,0,1;0rad)
  Solid = false
  Source = -> Face050
  Symmetric = false
FEATURE [Part::Feature] Face051
  shape: bbox 4.8 x 25.5 x 2e-07 mm, 1 faces, 0 solids (baked)
FEATURE [Part::Revolution] Revolve055  label="moreFrontCaseScrewPost002"
  Angle = 360
  Axis = (0,1,0)
  Base = (0,0,0)
  FaceMakerClass = Part::FaceMakerBullseye
  Placement = pos=(102.5,4.5,68.5) rot=(0,0,1;0rad)
  Solid = false
  Source = -> Face051
  Symmetric = false
FEATURE [Sketcher::SketchObject] Sketch027
  FullyConstrained = true
  sketch-geometry (10):
    g0: LineSegment StartX=-1.6 StartY=4.7 StartZ=0 EndX=-1.6 EndY=1.7 EndZ=0
    g1: LineSegment StartX=-3.5 StartY=4.7 StartZ=0 EndX=-1.6 EndY=4.7 EndZ=0
    g2: LineSegment StartX=-1.6 StartY=1.7 StartZ=0 EndX=-1.6 EndY=1.5 EndZ=0
    g3: LineSegment StartX=-1.6 StartY=1.5 StartZ=0 EndX=-5.2 EndY=1.5 EndZ=0
    g4: Circle CenterX=-3.5 CenterY=4.7 CenterZ=0 NormalX=0 NormalY=0 NormalZ=1 AngleXU=0 Radius=1
    g5: Circle CenterX=-3.59627 CenterY=2.99743 CenterZ=0 NormalX=0 NormalY=0 NormalZ=1 AngleXU=0 Radius=1
    g6: Circle CenterX=-5.2 CenterY=1.5 CenterZ=0 NormalX=0 NormalY=0 NormalZ=1 AngleXU=0 Radius=1
    g7: BSplineCurve PolesCount=3 KnotsCount=2 Degree=2 IsPeriodic=0
    g8: GeomPoint X=-3.5 Y=4.7 Z=0
    g9: GeomPoint X=-5.2 Y=1.5 Z=0
  constraints (23):
    c: Vertical(g0)
    c: Distance(g0) = 3
    c: Coincident(g1,g0)
    c: Horizontal(g1)
    c: Block(g0)
    c: Block(g1)
    c: Coincident(g2,g0)
    c: Vertical(g2)
    c: Distance(g2) = 0.2
    c: Coincident(g3,g2)
    c: Horizontal(g3)
    c: Block(g3)
    c: Coincident(g7,g1)
    c: Weight(g4) = 1
    c: Equal(g4,g5)
    c: Equal(g4,g6)
    c: Coincident(g7,g3)
    c: InternalAlignment(g4,g7)
    c: InternalAlignment(g5,g7)
    c: InternalAlignment(g6,g7)
    c: InternalAlignment(g8,g7)
    c: InternalAlignment(g9,g7)
    c: Block(g7)
FEATURE [Sketcher::SketchObject] Sketch028
  FullyConstrained = true
  sketch-geometry (18):
    g0: LineSegment StartX=0 StartY=3e-16 StartZ=0 EndX=0 EndY=1.7 EndZ=0
    g1: LineSegment StartX=-3.5 StartY=0 StartZ=0 EndX=-3.5 EndY=0.9 EndZ=0
    g2: Circle CenterX=-2.7 CenterY=1.7 CenterZ=0 NormalX=0 NormalY=0 NormalZ=1 AngleXU=0 Radius=1
    g3: Circle CenterX=-3.5 CenterY=1.7 CenterZ=0 NormalX=0 NormalY=0 NormalZ=1 AngleXU=0 Radius=1
    g4: Circle CenterX=-3.5 CenterY=0.9 CenterZ=0 NormalX=0 NormalY=0 NormalZ=1 AngleXU=0 Radius=1
    g5: BSplineCurve PolesCount=3 KnotsCount=2 Degree=2 IsPeriodic=0
    g6: GeomPoint X=-2.7 Y=1.7 Z=0
    g7: GeomPoint X=-3.5 Y=0.9 Z=0
    g8: LineSegment StartX=-3.5 StartY=0 StartZ=0 EndX=-3.5 EndY=-7 EndZ=0
    g9: LineSegment StartX=0 StartY=3e-16 StartZ=0 EndX=0 EndY=-7 EndZ=0
    g10: LineSegment StartX=-3.5 StartY=-7 StartZ=0 EndX=0 EndY=-7 EndZ=0
    g11: LineSegment StartX=-2.7 StartY=1.7 StartZ=0 EndX=-1.6 EndY=1.7 EndZ=0
    g12: LineSegment StartX=0 StartY=1.7 StartZ=0 EndX=0 EndY=4.5 EndZ=0
    g13: LineSegment StartX=0 StartY=4.5 StartZ=0 EndX=0 EndY=10.8 EndZ=0
    g14: LineSegment StartX=0 StartY=10.8 StartZ=0 EndX=-2 EndY=10.8 EndZ=0
    g15: LineSegment StartX=-1.6 StartY=4.7 StartZ=0 EndX=-1.6 EndY=1.7 EndZ=0
    g16: LineSegment StartX=-1.6 StartY=4.7 StartZ=0 EndX=-2 EndY=4.7 EndZ=0
    g17: LineSegment StartX=-2 StartY=4.7 StartZ=0 EndX=-2 EndY=10.8 EndZ=0
  constraints (44):
    c: Vertical(g0)
    c: Vertical(g1)
    c: Distance(g1) = 0.9
    c: Block(g0)
    c: Distance(g0) = 1.7
    c: Weight(g2) = 1
    c: Equal(g2,g3)
    c: Equal(g2,g4)
    c: Coincident(g5,g1)
    c: InternalAlignment(g2,g5)
    c: InternalAlignment(g3,g5)
    c: InternalAlignment(g4,g5)
    c: InternalAlignment(g6,g5)
    c: InternalAlignment(g7,g5)
    c: Block(g5)
    c: Coincident(g8,g1)
    c: Vertical(g8)
    c: Distance(g8) = 7
    c: Vertical(g9)
    c: Equal(g8,g9) = 7
    c: Coincident(g9,g0)
    c: Coincident(g10,g8)
    c: Coincident(g10,g9)
    c: Horizontal(g10)
    c: Coincident(g11,g5)
    c: Horizontal(g11)
    c: Coincident(g12,g0)
    c: Vertical(g12)
    c: Distance(g12) = 2.8
    c: Coincident(g13,g12)
    c: Vertical(g13)
    c: Distance(g13) = 6.3
    c: Coincident(g14,g13)
    c: Horizontal(g14)
    c: Distance(g14) = 2
    c: Vertical(g15)
    c: Distance(g15) = 3
    c: Block(g11)
    c: Coincident(g15,g11)
    c: Coincident(g16,g15)
    c: Horizontal(g16)
    c: Coincident(g17,g16)
    c: Coincident(g17,g14)
    c: Vertical(g17)
FEATURE [Part::Revolution] Revolve040  label="backCaseScrewRetainer001"
  Angle = 360
  Axis = (0,1,0)
  Base = (0,0,0)
  FaceMakerClass = Part::FaceMakerBullseye
  Placement = pos=(12.5,3,10) rot=(0,0,1;0rad)
  Solid = false
  Source = -> Face036
  Symmetric = false
FEATURE [Part::Feature] Face055
  shape: bbox 3.5 x 30.2 x 2e-07 mm, 1 faces, 0 solids (baked)
FEATURE [Part::Revolution] Revolve059  label="backCaseScrewPost"
  Angle = 360
  Axis = (0,1,0)
  Base = (0,0,0)
  FaceMakerClass = Part::FaceMakerBullseye
  Placement = pos=(12.5,4.5,10) rot=(0,0,1;0rad)
  Solid = false
  Source = -> Face055
  Symmetric = false
FEATURE [Part::Feature] Face056
  shape: bbox 3.5 x 30.2 x 2e-07 mm, 1 faces, 0 solids (baked)
FEATURE [Part::Revolution] Revolve060  label="backCaseScrewPost001"
  Angle = 360
  Axis = (0,1,0)
  Base = (0,0,0)
  FaceMakerClass = Part::FaceMakerBullseye
  Placement = pos=(12.5,4.5,62) rot=(0,0,1;0rad)
  Solid = false
  Source = -> Face056
  Symmetric = false
FEATURE [Part::Feature] Face057
  shape: bbox 3.5 x 17.8 x 2e-07 mm, 1 faces, 0 solids (baked)
FEATURE [Part::Revolution] Revolve061  label="removeToCreateScrewAndThreadedInsertHole"
  Angle = 360
  Axis = (0,1,0)
  Base = (0,0,0)
  FaceMakerClass = Part::FaceMakerBullseye
  Placement = pos=(12.5,0,10) rot=(0,0,1;0rad)
  Solid = false
  Source = -> Face057
  Symmetric = false
FEATURE [Part::Feature] Face058
  shape: bbox 3.5 x 17.8 x 2e-07 mm, 1 faces, 0 solids (baked)
FEATURE [Part::Revolution] Revolve062  label="removeToCreateScrewAndThreadedInsertHole001"
  Angle = 360
  Axis = (0,1,0)
  Base = (0,0,0)
  FaceMakerClass = Part::FaceMakerBullseye
  Placement = pos=(12.5,0,62) rot=(0,0,1;0rad)
  Solid = false
  Source = -> Face058
  Symmetric = false
FEATURE [Part::Feature] Face059
  shape: bbox 3.5 x 17.8 x 2e-07 mm, 1 faces, 0 solids (baked)
FEATURE [Part::Revolution] Revolve063  label="removeToCreateScrewAndThreadedInsertHole002"
  Angle = 360
  Axis = (0,1,0)
  Base = (0,0,0)
  FaceMakerClass = Part::FaceMakerBullseye
  Placement = pos=(89.5,0,68.5) rot=(0,0,1;0rad)
  Solid = false
  Source = -> Face059
  Symmetric = false
FEATURE [Part::Feature] Face060
  shape: bbox 3.5 x 17.8 x 2e-07 mm, 1 faces, 0 solids (baked)
FEATURE [Part::Revolution] Revolve064  label="removeToCreateScrewAndThreadedInsertHole003"
  Angle = 360
  Axis = (0,1,0)
  Base = (0,0,0)
  FaceMakerClass = Part::FaceMakerBullseye
  Placement = pos=(89.5,0,3.5) rot=(0,0,1;0rad)
  Solid = false
  Source = -> Face060
  Symmetric = false
FEATURE [Part::Feature] Face061
  shape: bbox 3.5 x 17.8 x 2e-07 mm, 1 faces, 0 solids (baked)
FEATURE [Part::Revolution] Revolve065  label="removeToCreateScrewAndThreadedInsertHole004"
  Angle = 360
  Axis = (0,1,0)
  Base = (0,0,0)
  FaceMakerClass = Part::FaceMakerBullseye
  Placement = pos=(102.5,4.7,3.5) rot=(0,0,1;0rad)
  Solid = false
  Source = -> Face061
  Symmetric = false
FEATURE [Part::Feature] Face062
  shape: bbox 3.5 x 17.8 x 2e-07 mm, 1 faces, 0 solids (baked)
FEATURE [Part::Revolution] Revolve066  label="removeToCreateScrewAndThreadedInsertHole005"
  Angle = 360
  Axis = (0,1,0)
  Base = (0,0,0)
  FaceMakerClass = Part::FaceMakerBullseye
  Placement = pos=(102.5,4.7,68.5) rot=(0,0,1;0rad)
  Solid = false
  Source = -> Face062
  Symmetric = false
FEATURE [Part::MultiFuse] Fusion047  label="makeHoles"
  Shapes = -> [Revolve066,Revolve065,Revolve064,Revolve063,Revolve062,Revolve061]
FEATURE [Part::Feature] Face063
  shape: bbox 3.6 x 3.2 x 2e-07 mm, 1 faces, 0 solids (baked)
FEATURE [Part::Revolution] Revolve067  label="moreFrontCaseScrewRetainer002"
  Angle = 360
  Axis = (0,1,0)
  Base = (0,0,0)
  FaceMakerClass = Part::FaceMakerBullseye
  Placement = pos=(102.5,4.5,68.5) rot=(0,0,1;0rad)
  Solid = false
  Source = -> Face063
  Symmetric = false
FEATURE [Part::Feature] Face064
  shape: bbox 3.6 x 3.2 x 2e-07 mm, 1 faces, 0 solids (baked)
FEATURE [Part::Revolution] Revolve068  label="moreFrontCaseScrewRetainer003"
  Angle = 360
  Axis = (0,1,0)
  Base = (0,0,0)
  FaceMakerClass = Part::FaceMakerBullseye
  Placement = pos=(102.5,4.5,3.5) rot=(0,0,1;0rad)
  Solid = false
  Source = -> Face064
  Symmetric = false
FEATURE [Part::Feature] Face065
  shape: bbox 3.5 x 17.8 x 2e-07 mm, 1 faces, 0 solids (baked)
FEATURE [Part::Revolution] Revolve069  label="removeToCreateScrewAndThreadedInsertHole006"
  Angle = 360
  Axis = (0,1,0)
  Base = (0,0,0)
  FaceMakerClass = Part::FaceMakerBullseye
  Placement = pos=(12.5,0,10) rot=(0,0,1;0rad)
  Solid = false
  Source = -> Face065
  Symmetric = false
FEATURE [Part::Feature] Face066
  shape: bbox 3.5 x 17.8 x 2e-07 mm, 1 faces, 0 solids (baked)
FEATURE [Part::Revolution] Revolve070  label="removeToCreateScrewAndThreadedInsertHole007"
  Angle = 360
  Axis = (0,1,0)
  Base = (0,0,0)
  FaceMakerClass = Part::FaceMakerBullseye
  Placement = pos=(12.5,0,62) rot=(0,0,1;0rad)
  Solid = false
  Source = -> Face066
  Symmetric = false
FEATURE [Part::Feature] Face067
  shape: bbox 3.5 x 17.8 x 2e-07 mm, 1 faces, 0 solids (baked)
FEATURE [Part::Revolution] Revolve071  label="removeToCreateScrewAndThreadedInsertHole008"
  Angle = 360
  Axis = (0,1,0)
  Base = (0,0,0)
  FaceMakerClass = Part::FaceMakerBullseye
  Placement = pos=(89.5,0,68.5) rot=(0,0,1;0rad)
  Solid = false
  Source = -> Face067
  Symmetric = false
FEATURE [Part::Feature] Face068
  shape: bbox 3.5 x 17.8 x 2e-07 mm, 1 faces, 0 solids (baked)
FEATURE [Part::Revolution] Revolve072  label="removeToCreateScrewAndThreadedInsertHole009"
  Angle = 360
  Axis = (0,1,0)
  Base = (0,0,0)
  FaceMakerClass = Part::FaceMakerBullseye
  Placement = pos=(89.5,0,3.5) rot=(0,0,1;0rad)
  Solid = false
  Source = -> Face068
  Symmetric = false
FEATURE [Part::Feature] Face069
  shape: bbox 3.5 x 17.8 x 2e-07 mm, 1 faces, 0 solids (baked)
FEATURE [Part::Feature] Face070
  shape: bbox 3.5 x 17.8 x 2e-07 mm, 1 faces, 0 solids (baked)
FEATURE [Part::Revolution] Revolve073  label="removeToCreateScrewAndThreadedInsertHole010"
  Angle = 360
  Axis = (0,1,0)
  Base = (0,0,0)
  FaceMakerClass = Part::FaceMakerBullseye
  Placement = pos=(102.5,4.7,3.5) rot=(0,0,1;0rad)
  Solid = false
  Source = -> Face069
  Symmetric = false
FEATURE [Part::Revolution] Revolve074  label="removeToCreateScrewAndThreadedInsertHole011"
  Angle = 360
  Axis = (0,1,0)
  Base = (0,0,0)
  FaceMakerClass = Part::FaceMakerBullseye
  Placement = pos=(102.5,4.7,68.5) rot=(0,0,1;0rad)
  Solid = false
  Source = -> Face070
  Symmetric = false
FEATURE [Part::MultiFuse] Fusion048  label="makeHoles001"
  Shapes = -> [Revolve074,Revolve073,Revolve072,Revolve071,Revolve070,Revolve069]
FEATURE [Part::MultiFuse] Fusion049  label="caseScrewRetainers"
  Shapes = -> [Revolve067,Revolve068,Revolve048,Revolve047,Revolve039,Revolve040]
FEATURE [Part::Cut] Cut015  label="caseScrewRetainers001"
  Base = -> Fusion049
  Tool = -> Fusion048
FEATURE [Part::MultiFuse] Fusion050  label="casePillars"
  Shapes = -> [Revolve055,Revolve054,Revolve043,Revolve046,Revolve059,Revolve060]
FEATURE [Part::Feature] Face071 .. Face076  x6 (patterned run collapsed; names and placements below)
  shape: bbox 3.5 x 17.8 x 2e-07 mm, 1 faces, 0 solids (baked)
FEATURE [Part::Revolution] Revolve075  label="removeToCreateScrewAndThreadedInsertHole012"
  Angle = 360
  Axis = (0,1,0)
  Base = (0,0,0)
  FaceMakerClass = Part::FaceMakerBullseye
  Placement = pos=(12.5,0,10) rot=(0,0,1;0rad)
  Solid = false
  Source = -> Face071
  Symmetric = false
FEATURE [Part::Revolution] Revolve076  label="removeToCreateScrewAndThreadedInsertHole013"
  Angle = 360
  Axis = (0,1,0)
  Base = (0,0,0)
  FaceMakerClass = Part::FaceMakerBullseye
  Placement = pos=(12.5,0,62) rot=(0,0,1;0rad)
  Solid = false
  Source = -> Face072
  Symmetric = false
FEATURE [Part::Revolution] Revolve077  label="removeToCreateScrewAndThreadedInsertHole014"
  Angle = 360
  Axis = (0,1,0)
  Base = (0,0,0)
  FaceMakerClass = Part::FaceMakerBullseye
  Placement = pos=(89.5,0,68.5) rot=(0,0,1;0rad)
  Solid = false
  Source = -> Face073
  Symmetric = false
FEATURE [Part::Revolution] Revolve078  label="removeToCreateScrewAndThreadedInsertHole015"
  Angle = 360
  Axis = (0,1,0)
  Base = (0,0,0)
  FaceMakerClass = Part::FaceMakerBullseye
  Placement = pos=(89.5,0,3.5) rot=(0,0,1;0rad)
  Solid = false
  Source = -> Face074
  Symmetric = false
FEATURE [Part::Revolution] Revolve079  label="removeToCreateScrewAndThreadedInsertHole016"
  Angle = 360
  Axis = (0,1,0)
  Base = (0,0,0)
  FaceMakerClass = Part::FaceMakerBullseye
  Placement = pos=(102.5,4.7,3.5) rot=(0,0,1;0rad)
  Solid = false
  Source = -> Face075
  Symmetric = false
FEATURE [Part::Revolution] Revolve080  label="removeToCreateScrewAndThreadedInsertHole017"
  Angle = 360
  Axis = (0,1,0)
  Base = (0,0,0)
  FaceMakerClass = Part::FaceMakerBullseye
  Placement = pos=(102.5,4.7,68.5) rot=(0,0,1;0rad)
  Solid = false
  Source = -> Face076
  Symmetric = false
FEATURE [Part::MultiFuse] Fusion051  label="makeHoles002"
  Shapes = -> [Revolve080,Revolve079,Revolve078,Revolve077,Revolve076,Revolve075]
FEATURE [Part::Cut] Cut016  label="caesPillars"
  Base = -> Fusion050
  Tool = -> Fusion051
FEATURE [Part::Revolution] Revolve009  label="plugHousing016"
  Angle = 360
  Axis = (0,1,0)
  Base = (0,0,0)
  FaceMakerClass = Part::FaceMakerBullseye
  Placement = pos=(0,0,36.15) rot=(0,0,1;0rad)
  Solid = false
  Source = -> Face012
  Symmetric = false
FEATURE [Part::MultiFuse] Fusion014  label="plugHousing023"
  Placement = pos=(0,0,0) rot=(0,0,1;1.5708rad)
  Shapes = -> [Revolve011,Revolve009]
FEATURE [Part::Revolution] Revolve010  label="plugHousing017"
  Angle = 360
  Axis = (0,1,0)
  Base = (0,0,0)
  FaceMakerClass = Part::FaceMakerBullseye
  Placement = pos=(0,0,36.15) rot=(0,0,1;0rad)
  Solid = false
  Source = -> Face014
  Symmetric = false
FEATURE [Part::MultiFuse] Fusion015  label="plugHousing024"
  Placement = pos=(0,0,0) rot=(0,0,1;1.5708rad)
  Shapes = -> [Revolve010,Revolve015]
FEATURE [Part::Revolution] Revolve014  label="plugHousing026"
  Angle = 360
  Axis = (0,1,0)
  Base = (0,0,0)
  FaceMakerClass = Part::FaceMakerBullseye
  Placement = pos=(0,0,36.15) rot=(0,0,1;0rad)
  Solid = false
  Source = -> Face011
  Symmetric = false
FEATURE [Part::Revolution] Revolve013  label="plugHousing025"
  Angle = 360
  Axis = (0,1,0)
  Base = (0,0,0)
  FaceMakerClass = Part::FaceMakerBullseye
  Placement = pos=(0,0,36.15) rot=(0,0,1;0rad)
  Solid = false
  Source = -> Face015
  Symmetric = false
FEATURE [Part::MultiFuse] Fusion016  label="plugHousing028"
  Placement = pos=(0,19,0) rot=(0,0,1;3.14159rad)
  Shapes = -> [Fusion014,Fusion013]
FEATURE [Part::MultiFuse] Fusion011  label="plugHousing018"
  Placement = pos=(0,0,0) rot=(0,0,1;1.5708rad)
  Shapes = -> [Revolve014,Revolve013]
FEATURE [Part::MultiFuse] Fusion012  label="plugHousing019"
  Placement = pos=(0,19,0) rot=(0,0,1;3.14159rad)
  Shapes = -> [Fusion011,Fusion015]
FEATURE [Part::MultiFuse] Fusion017  label="plugHousing029"
  Placement = pos=(122.621,0,-0.15) rot=(0,0,1;0rad)
  Shapes = -> [Fusion016,Fusion012]
FEATURE [Part::MultiFuse] Fusion052  label="casePillarRetainers"
  Shapes = -> [Extrude012,Extrude013,Extrude014,Extrude015,Extrude016,Extrude017,Extrude018,Extrude019,Box011,Box012]
FEATURE [Part::Feature] Face077
  shape: bbox 3.5 x 17.8 x 2e-07 mm, 1 faces, 0 solids (baked)
FEATURE [Part::Revolution] Revolve081  label="removeToCreateScrewAndThreadedInsertHole018"
  Angle = 360
  Axis = (0,1,0)
  Base = (0,0,0)
  FaceMakerClass = Part::FaceMakerBullseye
  Placement = pos=(62.3,30.3,19.7) rot=(0,0,1;0rad)
  Solid = false
  Source = -> Face077
  Symmetric = false
FEATURE [Part::Feature] Face078
  shape: bbox 3.5 x 17.8 x 2e-07 mm, 1 faces, 0 solids (baked)
FEATURE [Part::Revolution] Revolve082  label="removeToCreateScrewAndThreadedInsertHole019"
  Angle = 360
  Axis = (0,1,0)
  Base = (0,0,0)
  FaceMakerClass = Part::FaceMakerBullseye
  Placement = pos=(62.3,30.3,51.7) rot=(0,0,1;0rad)
  Solid = false
  Source = -> Face078
  Symmetric = false
FEATURE [Part::Feature] Face079
  shape: bbox 3.5 x 17.8 x 2e-07 mm, 1 faces, 0 solids (baked)
FEATURE [Part::Revolution] Revolve083  label="removeToCreateScrewAndThreadedInsertHole020"
  Angle = 360
  Axis = (0,1,0)
  Base = (0,0,0)
  FaceMakerClass = Part::FaceMakerBullseye
  Placement = pos=(30.3,30.3,19.7) rot=(0,0,1;0rad)
  Solid = false
  Source = -> Face079
  Symmetric = false
FEATURE [Part::Feature] Face080
  shape: bbox 3.5 x 17.8 x 2e-07 mm, 1 faces, 0 solids (baked)
FEATURE [Part::Revolution] Revolve084  label="removeToCreateScrewAndThreadedInsertHole021"
  Angle = 360
  Axis = (0,1,0)
  Base = (0,0,0)
  FaceMakerClass = Part::FaceMakerBullseye
  Placement = pos=(30.3,30.3,51.7) rot=(0,0,1;0rad)
  Solid = false
  Source = -> Face080
  Symmetric = false
FEATURE [Part::MultiFuse] Fusion053  label="createThreadedInsertHolesForFan"
  Shapes = -> [Revolve081,Revolve082,Revolve083,Revolve084]
FEATURE [Part::Cut] Cut017  label="fanScrewHousing001"
  Base = -> Fusion046
  Tool = -> Fusion053
FEATURE [Part::Feature] Face081
  shape: bbox 3.5 x 17.8 x 2e-07 mm, 1 faces, 0 solids (baked)
FEATURE [Part::Revolution] Revolve085  label="removeToCreateScrewAndThreadedInsertHole022"
  Angle = 360
  Axis = (0,1,0)
  Base = (0,0,0)
  FaceMakerClass = Part::FaceMakerBullseye
  Placement = pos=(62.3,30.3,19.7) rot=(0,0,1;0rad)
  Solid = false
  Source = -> Face081
  Symmetric = false
FEATURE [Part::Feature] Face082
  shape: bbox 3.5 x 17.8 x 2e-07 mm, 1 faces, 0 solids (baked)
FEATURE [Part::Revolution] Revolve086  label="removeToCreateScrewAndThreadedInsertHole023"
  Angle = 360
  Axis = (0,1,0)
  Base = (0,0,0)
  FaceMakerClass = Part::FaceMakerBullseye
  Placement = pos=(62.3,30.3,51.7) rot=(0,0,1;0rad)
  Solid = false
  Source = -> Face082
  Symmetric = false
FEATURE [Part::Feature] Face083
  shape: bbox 3.5 x 17.8 x 2e-07 mm, 1 faces, 0 solids (baked)
FEATURE [Part::Revolution] Revolve087  label="removeToCreateScrewAndThreadedInsertHole024"
  Angle = 360
  Axis = (0,1,0)
  Base = (0,0,0)
  FaceMakerClass = Part::FaceMakerBullseye
  Placement = pos=(30.3,30.3,19.7) rot=(0,0,1;0rad)
  Solid = false
  Source = -> Face083
  Symmetric = false
FEATURE [Part::Feature] Face084
  shape: bbox 3.5 x 17.8 x 2e-07 mm, 1 faces, 0 solids (baked)
FEATURE [Part::Revolution] Revolve088  label="removeToCreateScrewAndThreadedInsertHole025"
  Angle = 360
  Axis = (0,1,0)
  Base = (0,0,0)
  FaceMakerClass = Part::FaceMakerBullseye
  Placement = pos=(30.3,30.3,51.7) rot=(0,0,1;0rad)
  Solid = false
  Source = -> Face084
  Symmetric = false
FEATURE [Part::MultiFuse] Fusion054  label="createThreadedInsertHolesForFan001"
  Shapes = -> [Revolve085,Revolve086,Revolve087,Revolve088]
FEATURE [Part::Cut] Cut018  label="top007"
  Base = -> Fusion040
  Tool = -> Fusion054
FEATURE [Sketcher::SketchObject] Sketch029
  FullyConstrained = false
  Placement = pos=(0,0,0) rot=(1,0,0;1.5708rad)
  sketch-geometry (24):
    g0: ArcOfCircle CenterX=-4 CenterY=-10.5 CenterZ=0 NormalX=0 NormalY=0 NormalZ=1 AngleXU=0 Radius=1.5 StartAngle=6e-16 EndAngle=3.14159
    g1: ArcOfCircle CenterX=-34.2 CenterY=-10.5 CenterZ=0 NormalX=0 NormalY=0 NormalZ=1 AngleXU=0 Radius=1.5 StartAngle=0 EndAngle=3.14159
    g2: ArcOfCircle CenterX=-34.2 CenterY=-27.7 CenterZ=0 NormalX=0 NormalY=0 NormalZ=1 AngleXU=0 Radius=1.5 StartAngle=3.14159 EndAngle=6.28319
    g3: ArcOfCircle CenterX=-4 CenterY=-27.7 CenterZ=0 NormalX=0 NormalY=0 NormalZ=1 AngleXU=0 Radius=1.5 StartAngle=3.1416 EndAngle=6.28319
    g4: ArcOfCircle CenterX=-10 CenterY=-4.3 CenterZ=0 NormalX=0 NormalY=0 NormalZ=1 AngleXU=0 Radius=1.5 StartAngle=2e-16 EndAngle=3.14159
    g5: ArcOfCircle CenterX=-16.1 CenterY=-1.8 CenterZ=0 NormalX=0 NormalY=0 NormalZ=1 AngleXU=0 Radius=1.5 StartAngle=5e-16 EndAngle=3.14159
    g6: ArcOfCircle CenterX=-22.1 CenterY=-1.8 CenterZ=0 NormalX=0 NormalY=0 NormalZ=1 AngleXU=0 Radius=1.5 StartAngle=5e-16 EndAngle=3.14159
    g7: ArcOfCircle CenterX=-28.2 CenterY=-4.3 CenterZ=0 NormalX=0 NormalY=0 NormalZ=1 AngleXU=0 Radius=1.5 StartAngle=2e-16 EndAngle=3.14159
    g8: ArcOfCircle CenterX=-10 CenterY=-33.9 CenterZ=0 NormalX=0 NormalY=0 NormalZ=1 AngleXU=0 Radius=1.5 StartAngle=3.14159 EndAngle=6.28319
    g9: ArcOfCircle CenterX=-16.1 CenterY=-36.4 CenterZ=0 NormalX=0 NormalY=0 NormalZ=1 AngleXU=0 Radius=1.5 StartAngle=3.14159 EndAngle=6.28319
    g10: ArcOfCircle CenterX=-22.1 CenterY=-36.4 CenterZ=0 NormalX=0 NormalY=0 NormalZ=1 AngleXU=0 Radius=1.5 StartAngle=3.14159 EndAngle=6.28319
    g11: ArcOfCircle CenterX=-28.2 CenterY=-33.9 CenterZ=0 NormalX=0 NormalY=0 NormalZ=1 AngleXU=0 Radius=1.5 StartAngle=3.14159 EndAngle=6.28319
    g12: LineSegment StartX=-35.7 StartY=-10.5 StartZ=0 EndX=-35.7 EndY=-27.7 EndZ=0
    g13: LineSegment StartX=-32.7 StartY=-10.5 StartZ=0 EndX=-32.7 EndY=-27.7 EndZ=0
    g14: LineSegment StartX=-29.7 StartY=-33.9 StartZ=0 EndX=-29.7 EndY=-4.3 EndZ=0
    g15: LineSegment StartX=-26.7 StartY=-33.9 StartZ=0 EndX=-26.7 EndY=-4.3 EndZ=0
    g16: LineSegment StartX=-2.5 StartY=-10.5 StartZ=0 EndX=-2.5 EndY=-27.7 EndZ=0
    g17: LineSegment StartX=-8.5 StartY=-4.3 StartZ=0 EndX=-8.5 EndY=-33.9 EndZ=0
    g18: LineSegment StartX=-5.5 StartY=-10.5 StartZ=0 EndX=-5.5 EndY=-27.7 EndZ=0
    g19: LineSegment StartX=-11.5 StartY=-4.3 StartZ=0 EndX=-11.5 EndY=-33.9 EndZ=0
    g20: LineSegment StartX=-14.6 StartY=-1.8 StartZ=0 EndX=-14.6 EndY=-36.4 EndZ=0
    g21: LineSegment StartX=-17.6 StartY=-1.8 StartZ=0 EndX=-17.6 EndY=-36.4 EndZ=0
    g22: LineSegment StartX=-20.6 StartY=-36.4 StartZ=0 EndX=-20.6 EndY=-1.8 EndZ=0
    g23: LineSegment StartX=-23.6 StartY=-1.8 StartZ=0 EndX=-23.6 EndY=-36.4 EndZ=0
  constraints (48):
    c: Block(g0)
    c: Block(g1)
    c: Block(g2)
    c: Block(g3)
    c: Block(g4)
    c: Block(g5)
    c: Block(g6)
    c: Block(g7)
    c: Block(g8)
    c: Block(g9)
    c: Block(g10)
    c: Block(g11)
    c: Coincident(g12,g1)
    c: Coincident(g12,g2)
    c: Vertical(g12)
    c: Coincident(g13,g1)
    c: Coincident(g13,g2)
    c: Vertical(g13)
    c: Coincident(g14,g11)
    c: Coincident(g14,g7)
    c: Vertical(g14)
    c: Coincident(g15,g11)
    c: Coincident(g15,g7)
    c: Vertical(g15)
    c: Coincident(g16,g0)
    c: Coincident(g16,g3)
    c: Vertical(g16)
    c: Coincident(g17,g4)
    c: Coincident(g17,g8)
    c: Vertical(g17)
    c: Coincident(g18,g0)
    c: Coincident(g18,g3)
    c: Vertical(g18)
    c: Coincident(g19,g4)
    c: Coincident(g19,g8)
    c: Vertical(g19)
    c: Coincident(g20,g5)
    c: Coincident(g20,g9)
    c: Vertical(g20)
    c: Coincident(g21,g5)
    c: Coincident(g21,g9)
    c: Vertical(g21)
    c: Coincident(g22,g10)
    c: Coincident(g22,g6)
    c: Vertical(g22)
    c: Coincident(g23,g6)
    c: Coincident(g23,g10)
    c: Vertical(g23)
FEATURE [Part::Extrusion] Extrude020  label="removeToCreateFanGrillHoles"
  Base = -> Sketch029
  Dir = (0,-1,6e-16)
  DirMode = 2
  FaceMakerClass = Part::FaceMakerBullseye
  LengthFwd = 10
  LengthRev = 0
  Placement = pos=(65.4,44,54.82) rot=(0,0,1;0rad)
  Solid = true
  Symmetric = false
FEATURE [Part::MultiFuse] Fusion055  label="top008"
  Shapes = -> [Cut017,Cut018]
FEATURE [Part::Cut] Cut019  label="top009"
  Base = -> Fusion055
  Tool = -> Extrude020
FEATURE [App::MeasureDistance] Distance003  label="Distance: 71.95 mm"
  Distance = 71.9513
  P1 = (117,38,72)
  P2 = (117,38,0.0487319)
FEATURE [Sketcher::SketchObject] Sketch030
  FullyConstrained = true
  Placement = pos=(117,19,0) rot=(0.57735,0.57735,0.57735;2.0944rad)
  sketch-geometry (48):
    g0: LineSegment StartX=-49.19 StartY=69.25 StartZ=0 EndX=-49.19 EndY=66.25 EndZ=0
    g1: LineSegment StartX=-49.19 StartY=63.5 StartZ=0 EndX=-49.19 EndY=60.5 EndZ=0
    g2: LineSegment StartX=-49.19 StartY=57.75 StartZ=0 EndX=-49.19 EndY=54.75 EndZ=0
    g3: LineSegment StartX=-49.19 StartY=52 StartZ=0 EndX=-49.19 EndY=49 EndZ=0
    g4: LineSegment StartX=-49.19 StartY=46.25 StartZ=0 EndX=-49.19 EndY=43.25 EndZ=0
    g5: LineSegment StartX=-49.19 StartY=40.5 StartZ=0 EndX=-49.19 EndY=37.5 EndZ=0
    g6: LineSegment StartX=-49.19 StartY=34.5 StartZ=0 EndX=-49.19 EndY=31.5 EndZ=0
    g7: LineSegment StartX=-49.19 StartY=28.75 StartZ=0 EndX=-49.19 EndY=25.75 EndZ=0
    g8: LineSegment StartX=-49.19 StartY=23 StartZ=0 EndX=-49.19 EndY=20 EndZ=0
    g9: LineSegment StartX=-49.19 StartY=17.25 StartZ=0 EndX=-49.19 EndY=14.25 EndZ=0
    g10: LineSegment StartX=-49.19 StartY=11.5 StartZ=0 EndX=-49.19 EndY=8.5 EndZ=0
    g11: LineSegment StartX=-49.19 StartY=5.75 StartZ=0 EndX=-49.19 EndY=2.75 EndZ=0
    g12: ArcOfCircle CenterX=-1.5 CenterY=67.75 CenterZ=0 NormalX=0 NormalY=0 NormalZ=1 AngleXU=0 Radius=1.5 StartAngle=4.71239 EndAngle=7.85398
    g13: ArcOfCircle CenterX=-1.5 CenterY=62 CenterZ=0 NormalX=0 NormalY=0 NormalZ=1 AngleXU=0 Radius=1.5 StartAngle=4.71239 EndAngle=7.85398
    g14: ArcOfCircle CenterX=-1.5 CenterY=56.25 CenterZ=0 NormalX=0 NormalY=0 NormalZ=1 AngleXU=0 Radius=1.5 StartAngle=4.71239 EndAngle=7.85398
    g15: ArcOfCircle CenterX=-11.49 CenterY=50.5 CenterZ=0 NormalX=0 NormalY=0 NormalZ=1 AngleXU=0 Radius=1.5 StartAngle=4.71239 EndAngle=7.85398
    g16: ArcOfCircle CenterX=-16.28 CenterY=44.75 CenterZ=0 NormalX=0 NormalY=0 NormalZ=1 AngleXU=0 Radius=1.5 StartAngle=4.71239 EndAngle=7.85398
    g17: ArcOfCircle CenterX=-18.2337 CenterY=39 CenterZ=0 NormalX=0 NormalY=0 NormalZ=1 AngleXU=0 Radius=1.5 StartAngle=4.71485 EndAngle=7.85398
    g18: ArcOfCircle CenterX=-16.2837 CenterY=27.25 CenterZ=0 NormalX=0 NormalY=0 NormalZ=1 AngleXU=0 Radius=1.5 StartAngle=4.71485 EndAngle=7.85398
    g19: ArcOfCircle CenterX=-18.2337 CenterY=33 CenterZ=0 NormalX=0 NormalY=0 NormalZ=1 AngleXU=0 Radius=1.5 StartAngle=4.71485 EndAngle=7.85398
    g20: ArcOfCircle CenterX=-11.49 CenterY=21.5 CenterZ=0 NormalX=0 NormalY=0 NormalZ=1 AngleXU=0 Radius=1.5 StartAngle=4.71239 EndAngle=7.85398
    g21: ArcOfCircle CenterX=-1.5 CenterY=4.25 CenterZ=0 NormalX=0 NormalY=0 NormalZ=1 AngleXU=0 Radius=1.5 StartAngle=4.71239 EndAngle=7.85398
    g22: ArcOfCircle CenterX=-1.5 CenterY=10 CenterZ=0 NormalX=0 NormalY=0 NormalZ=1 AngleXU=0 Radius=1.5 StartAngle=4.71239 EndAngle=7.85398
    g23: ArcOfCircle CenterX=-1.5 CenterY=15.75 CenterZ=0 NormalX=0 NormalY=0 NormalZ=1 AngleXU=0 Radius=1.5 StartAngle=4.71239 EndAngle=7.85398
    g24: LineSegment StartX=-49.19 StartY=69.25 StartZ=0 EndX=-1.5 EndY=69.25 EndZ=0
    g25: LineSegment StartX=-49.19 StartY=66.25 StartZ=0 EndX=-1.5 EndY=66.25 EndZ=0
    g26: LineSegment StartX=-49.19 StartY=63.5 StartZ=0 EndX=-1.5 EndY=63.5 EndZ=0
    g27: LineSegment StartX=-49.19 StartY=60.5 StartZ=0 EndX=-1.5 EndY=60.5 EndZ=0
    g28: LineSegment StartX=-49.19 StartY=57.75 StartZ=0 EndX=-1.5 EndY=57.75 EndZ=0
    g29: LineSegment StartX=-49.19 StartY=54.75 StartZ=0 EndX=-1.5 EndY=54.75 EndZ=0
    g30: LineSegment StartX=-49.19 StartY=52 StartZ=0 EndX=-11.49 EndY=52 EndZ=0
    g31: LineSegment StartX=-49.19 StartY=49 StartZ=0 EndX=-11.49 EndY=49 EndZ=0
    g32: LineSegment StartX=-49.19 StartY=46.25 StartZ=0 EndX=-16.28 EndY=46.25 EndZ=0
    g33: LineSegment StartX=-49.19 StartY=43.25 StartZ=0 EndX=-16.28 EndY=43.25 EndZ=0
    g34: LineSegment StartX=-49.19 StartY=40.5 StartZ=0 EndX=-18.2337 EndY=40.5 EndZ=0
    g35: LineSegment StartX=-49.19 StartY=37.5 StartZ=0 EndX=-18.23 EndY=37.5 EndZ=0
    g36: LineSegment StartX=-49.19 StartY=34.5 StartZ=0 EndX=-18.2337 EndY=34.5 EndZ=0
    g37: LineSegment StartX=-49.19 StartY=31.5 StartZ=0 EndX=-18.23 EndY=31.5 EndZ=0
    g38: LineSegment StartX=-49.19 StartY=28.75 StartZ=0 EndX=-16.2837 EndY=28.75 EndZ=0
    g39: LineSegment StartX=-49.19 StartY=25.75 StartZ=0 EndX=-16.28 EndY=25.75 EndZ=0
    g40: LineSegment StartX=-49.19 StartY=23 StartZ=0 EndX=-11.49 EndY=23 EndZ=0
    g41: LineSegment StartX=-49.19 StartY=20 StartZ=0 EndX=-11.49 EndY=20 EndZ=0
    g42: LineSegment StartX=-49.19 StartY=17.25 StartZ=0 EndX=-1.5 EndY=17.25 EndZ=0
    g43: LineSegment StartX=-49.19 StartY=14.25 StartZ=0 EndX=-1.5 EndY=14.25 EndZ=0
    g44: LineSegment StartX=-49.19 StartY=11.5 StartZ=0 EndX=-1.5 EndY=11.5 EndZ=0
    g45: LineSegment StartX=-49.19 StartY=8.5 StartZ=0 EndX=-1.5 EndY=8.5 EndZ=0
    g46: LineSegment StartX=-49.19 StartY=5.75 StartZ=0 EndX=-1.5 EndY=5.75 EndZ=0
    g47: LineSegment StartX=-49.19 StartY=2.75 StartZ=0 EndX=-1.5 EndY=2.75 EndZ=0
  constraints (120):
    c: Vertical(g0)
    c: Distance(g0) = 3
    c: Block(g0)
    c: Vertical(g1)
    c: Distance(g1) = 3
    c: Vertical(g2)
    c: Equal(g0,g2) = 3
    c: Block(g2)
    c: Vertical(g3)
    c: Equal(g1,g3) = 3
    c: Vertical(g4)
    c: Equal(g0,g4) = 3
    c: Block(g4)
    c: Vertical(g5)
    c: Equal(g1,g5) = 3
    c: Vertical(g6)
    c: Equal(g0,g6) = 3
    c: Block(g6)
    c: Vertical(g7)
    c: Equal(g1,g7) = 3
    c: Vertical(g8)
    c: Equal(g0,g8) = 3
    c: Block(g8)
    c: Vertical(g9)
    c: Equal(g1,g9) = 3
    c: Vertical(g10)
    c: Equal(g0,g10) = 3
    c: Block(g10)
    c: Vertical(g11)
    c: Equal(g1,g11) = 3
    c: Block(g12)
    c: Block(g13)
    c: Block(g14)
    c: Block(g15)
    c: Block(g16)
    c: Block(g17)
    c: Block(g18)
    c: Block(g19)
    c: Block(g20)
    c: Block(g21)
    c: Block(g22)
    c: Block(g23)
    c: Block(g11)
    c: Block(g9)
    c: Block(g7)
    c: Block(g5)
    c: Block(g3)
    c: Block(g1)
    c: Coincident(g24,g0)
    c: Coincident(g24,g12)
    c: Horizontal(g24)
    c: Coincident(g25,g0)
    c: Coincident(g25,g12)
    c: Horizontal(g25)
    c: Coincident(g26,g1)
    c: Coincident(g26,g13)
    c: Horizontal(g26)
    c: Coincident(g27,g1)
    c: Coincident(g27,g13)
    c: Horizontal(g27)
    c: Coincident(g28,g2)
    c: Coincident(g28,g14)
    c: Horizontal(g28)
    c: Coincident(g29,g2)
    c: Coincident(g29,g14)
    c: Horizontal(g29)
    c: Coincident(g30,g3)
    c: Coincident(g30,g15)
    c: Horizontal(g30)
    c: Coincident(g31,g3)
    c: Coincident(g31,g15)
    c: Horizontal(g31)
    c: Coincident(g32,g4)
    c: Coincident(g32,g16)
    c: Horizontal(g32)
    c: Coincident(g33,g4)
    c: Coincident(g33,g16)
    c: Horizontal(g33)
    c: Coincident(g34,g5)
    c: Coincident(g34,g17)
    c: Horizontal(g34)
    c: Coincident(g35,g5)
    c: Coincident(g35,g17)
    c: Horizontal(g35)
    c: Coincident(g36,g6)
    c: Coincident(g36,g19)
    c: Horizontal(g36)
    c: Coincident(g37,g6)
    c: Coincident(g37,g19)
    c: Horizontal(g37)
    c: Coincident(g38,g7)
    c: Coincident(g38,g18)
    c: Horizontal(g38)
    c: Coincident(g39,g7)
    c: Coincident(g39,g18)
    c: Horizontal(g39)
    c: Coincident(g40,g8)
    c: Coincident(g40,g20)
    c: Horizontal(g40)
    c: Coincident(g41,g8)
    c: Coincident(g41,g20)
    c: Horizontal(g41)
    c: Coincident(g42,g9)
    c: Coincident(g42,g23)
    c: Horizontal(g42)
    c: Coincident(g43,g9)
    c: Coincident(g43,g23)
    c: Horizontal(g43)
    c: Coincident(g44,g10)
    c: Coincident(g44,g22)
    c: Horizontal(g44)
    c: Coincident(g45,g10)
    c: Coincident(g45,g22)
    c: Horizontal(g45)
    c: Coincident(g46,g11)
    c: Coincident(g46,g21)
    c: Horizontal(g46)
    c: Coincident(g47,g11)
    c: Coincident(g47,g21)
    c: Horizontal(g47)
FEATURE [Sketcher::SketchObject] Sketch031
  FullyConstrained = true
  Placement = pos=(117,19,0) rot=(0.57735,0.57735,0.57735;2.0944rad)
  sketch-geometry (24):
    g0: ArcOfCircle CenterX=-49.19 CenterY=67.75 CenterZ=0 NormalX=0 NormalY=0 NormalZ=1 AngleXU=0 Radius=1.5 StartAngle=1.5708 EndAngle=4.71239
    g1: ArcOfCircle CenterX=-49.19 CenterY=62 CenterZ=0 NormalX=0 NormalY=0 NormalZ=1 AngleXU=0 Radius=1.5 StartAngle=1.5708 EndAngle=4.71239
    g2: ArcOfCircle CenterX=-49.19 CenterY=56.25 CenterZ=0 NormalX=0 NormalY=0 NormalZ=1 AngleXU=0 Radius=1.5 StartAngle=1.5708 EndAngle=4.71239
    g3: ArcOfCircle CenterX=-49.19 CenterY=50.5 CenterZ=0 NormalX=0 NormalY=0 NormalZ=1 AngleXU=0 Radius=1.5 StartAngle=1.5708 EndAngle=4.71239
    g4: ArcOfCircle CenterX=-49.19 CenterY=44.75 CenterZ=0 NormalX=0 NormalY=0 NormalZ=1 AngleXU=0 Radius=1.5 StartAngle=1.5708 EndAngle=4.71239
    g5: ArcOfCircle CenterX=-49.19 CenterY=39 CenterZ=0 NormalX=0 NormalY=0 NormalZ=1 AngleXU=0 Radius=1.5 StartAngle=1.5708 EndAngle=4.71239
    g6: ArcOfCircle CenterX=-49.19 CenterY=33 CenterZ=0 NormalX=0 NormalY=0 NormalZ=1 AngleXU=0 Radius=1.5 StartAngle=1.5708 EndAngle=4.71239
    g7: ArcOfCircle CenterX=-49.19 CenterY=27.25 CenterZ=0 NormalX=0 NormalY=0 NormalZ=1 AngleXU=0 Radius=1.5 StartAngle=1.5708 EndAngle=4.71239
    g8: ArcOfCircle CenterX=-49.19 CenterY=21.5 CenterZ=0 NormalX=0 NormalY=0 NormalZ=1 AngleXU=0 Radius=1.5 StartAngle=1.5708 EndAngle=4.71239
    g9: ArcOfCircle CenterX=-49.19 CenterY=15.75 CenterZ=0 NormalX=0 NormalY=0 NormalZ=1 AngleXU=0 Radius=1.5 StartAngle=1.5708 EndAngle=4.71239
    g10: ArcOfCircle CenterX=-49.19 CenterY=10 CenterZ=0 NormalX=0 NormalY=0 NormalZ=1 AngleXU=0 Radius=1.5 StartAngle=1.5708 EndAngle=4.71239
    g11: ArcOfCircle CenterX=-49.19 CenterY=4.25 CenterZ=0 NormalX=0 NormalY=0 NormalZ=1 AngleXU=0 Radius=1.5 StartAngle=1.5708 EndAngle=4.71239
    g12: LineSegment StartX=-49.19 StartY=69.25 StartZ=0 EndX=-49.19 EndY=66.25 EndZ=0
    g13: LineSegment StartX=-49.19 StartY=63.5 StartZ=0 EndX=-49.19 EndY=60.5 EndZ=0
    g14: LineSegment StartX=-49.19 StartY=57.75 StartZ=0 EndX=-49.19 EndY=54.75 EndZ=0
    g15: LineSegment StartX=-49.19 StartY=52 StartZ=0 EndX=-49.19 EndY=49 EndZ=0
    g16: LineSegment StartX=-49.19 StartY=46.25 StartZ=0 EndX=-49.19 EndY=43.25 EndZ=0
    g17: LineSegment StartX=-49.19 StartY=40.5 StartZ=0 EndX=-49.19 EndY=37.5 EndZ=0
    g18: LineSegment StartX=-49.19 StartY=34.5 StartZ=0 EndX=-49.19 EndY=31.5 EndZ=0
    g19: LineSegment StartX=-49.19 StartY=28.75 StartZ=0 EndX=-49.19 EndY=25.75 EndZ=0
    g20: LineSegment StartX=-49.19 StartY=23 StartZ=0 EndX=-49.19 EndY=20 EndZ=0
    g21: LineSegment StartX=-49.19 StartY=17.25 StartZ=0 EndX=-49.19 EndY=14.25 EndZ=0
    g22: LineSegment StartX=-49.19 StartY=11.5 StartZ=0 EndX=-49.19 EndY=8.5 EndZ=0
    g23: LineSegment StartX=-49.19 StartY=5.75 StartZ=0 EndX=-49.19 EndY=2.75 EndZ=0
  constraints (48):
    c: Block(g0)
    c: Block(g1)
    c: Block(g2)
    c: Block(g3)
    c: Block(g4)
    c: Block(g5)
    c: Block(g6)
    c: Block(g7)
    c: Block(g8)
    c: Block(g9)
    c: Block(g10)
    c: Block(g11)
    c: Coincident(g12,g0)
    c: Coincident(g12,g0)
    c: Vertical(g12)
    c: Vertical(g13)
    c: Coincident(g13,g1)
    c: Vertical(g14)
    c: Coincident(g14,g2)
    c: Vertical(g15)
    c: Coincident(g15,g3)
    c: Vertical(g16)
    c: Coincident(g16,g4)
    c: Vertical(g17)
    c: Coincident(g17,g5)
    c: Vertical(g18)
    c: Coincident(g18,g6)
    c: Vertical(g19)
    c: Coincident(g19,g7)
    c: Vertical(g20)
    c: Coincident(g20,g8)
    c: Vertical(g21)
    c: Coincident(g21,g9)
    c: Vertical(g22)
    c: Coincident(g22,g10)
    c: Vertical(g23)
    c: Coincident(g23,g11)
    c: Block(g23)
    c: Block(g22)
    c: Block(g21)
    c: Block(g20)
    c: Block(g13)
    c: Block(g14)
    c: Block(g15)
    c: Block(g16)
    c: Block(g17)
    c: Block(g18)
    c: Block(g19)
FEATURE [Part::Extrusion] Extrude022
  Base = -> Sketch030
  Dir = (1,-2e-16,2e-16)
  DirMode = 2
  FaceMakerClass = Part::FaceMakerBullseye
  LengthFwd = 19
  LengthRev = 0
  Placement = pos=(-19,0,0) rot=(0,0,1;0rad)
  Solid = true
  Symmetric = false
FEATURE [Part::Fillet] Fillet022
  Base = -> Extrude022
  Edges = 24 edges r=1.49: [Edge6,Edge11,Edge18,Edge23,Edge30,Edge35,Edge42,Edge47,Edge54,Edge59,Edge66,Edge71,Edge78,Edge83,Edge90,Edge95,Edge102,Edge107,Edge114,Edge119,Edge126,Edge131,Edge138,Edge143]
FEATURE [Part::Cut] Cut020  label="top010"
  Base = -> Cut019
  Tool = -> Fillet022
FEATURE [Sketcher::SketchObject] Sketch032
  FullyConstrained = true
  Placement = pos=(117,19,0) rot=(0.57735,0.57735,0.57735;2.0944rad)
  sketch-geometry (48):
    g0: LineSegment StartX=-49.19 StartY=69.25 StartZ=0 EndX=-49.19 EndY=66.25 EndZ=0
    g1: LineSegment StartX=-49.19 StartY=63.5 StartZ=0 EndX=-49.19 EndY=60.5 EndZ=0
    g2: LineSegment StartX=-49.19 StartY=57.75 StartZ=0 EndX=-49.19 EndY=54.75 EndZ=0
    g3: LineSegment StartX=-49.19 StartY=52 StartZ=0 EndX=-49.19 EndY=49 EndZ=0
    g4: LineSegment StartX=-49.19 StartY=46.25 StartZ=0 EndX=-49.19 EndY=43.25 EndZ=0
    g5: LineSegment StartX=-49.19 StartY=40.5 StartZ=0 EndX=-49.19 EndY=37.5 EndZ=0
    g6: LineSegment StartX=-49.19 StartY=34.5 StartZ=0 EndX=-49.19 EndY=31.5 EndZ=0
    g7: LineSegment StartX=-49.19 StartY=28.75 StartZ=0 EndX=-49.19 EndY=25.75 EndZ=0
    g8: LineSegment StartX=-49.19 StartY=23 StartZ=0 EndX=-49.19 EndY=20 EndZ=0
    g9: LineSegment StartX=-49.19 StartY=17.25 StartZ=0 EndX=-49.19 EndY=14.25 EndZ=0
    g10: LineSegment StartX=-49.19 StartY=11.5 StartZ=0 EndX=-49.19 EndY=8.5 EndZ=0
    g11: LineSegment StartX=-49.19 StartY=5.75 StartZ=0 EndX=-49.19 EndY=2.75 EndZ=0
    g12: ArcOfCircle CenterX=-1.5 CenterY=67.75 CenterZ=0 NormalX=0 NormalY=0 NormalZ=1 AngleXU=0 Radius=1.5 StartAngle=4.71239 EndAngle=7.85398
    g13: ArcOfCircle CenterX=-1.5 CenterY=62 CenterZ=0 NormalX=0 NormalY=0 NormalZ=1 AngleXU=0 Radius=1.5 StartAngle=4.71239 EndAngle=7.85398
    g14: ArcOfCircle CenterX=-1.5 CenterY=56.25 CenterZ=0 NormalX=0 NormalY=0 NormalZ=1 AngleXU=0 Radius=1.5 StartAngle=4.71239 EndAngle=7.85398
    g15: ArcOfCircle CenterX=-11.49 CenterY=50.5 CenterZ=0 NormalX=0 NormalY=0 NormalZ=1 AngleXU=0 Radius=1.5 StartAngle=4.71239 EndAngle=7.85398
    g16: ArcOfCircle CenterX=-16.28 CenterY=44.75 CenterZ=0 NormalX=0 NormalY=0 NormalZ=1 AngleXU=0 Radius=1.5 StartAngle=4.71239 EndAngle=7.85398
    g17: ArcOfCircle CenterX=-18.2337 CenterY=39 CenterZ=0 NormalX=0 NormalY=0 NormalZ=1 AngleXU=0 Radius=1.5 StartAngle=4.71485 EndAngle=7.85398
    g18: ArcOfCircle CenterX=-16.2837 CenterY=27.25 CenterZ=0 NormalX=0 NormalY=0 NormalZ=1 AngleXU=0 Radius=1.5 StartAngle=4.71485 EndAngle=7.85398
    g19: ArcOfCircle CenterX=-18.2337 CenterY=33 CenterZ=0 NormalX=0 NormalY=0 NormalZ=1 AngleXU=0 Radius=1.5 StartAngle=4.71485 EndAngle=7.85398
    g20: ArcOfCircle CenterX=-11.49 CenterY=21.5 CenterZ=0 NormalX=0 NormalY=0 NormalZ=1 AngleXU=0 Radius=1.5 StartAngle=4.71239 EndAngle=7.85398
    g21: ArcOfCircle CenterX=-1.5 CenterY=4.25 CenterZ=0 NormalX=0 NormalY=0 NormalZ=1 AngleXU=0 Radius=1.5 StartAngle=4.71239 EndAngle=7.85398
    g22: ArcOfCircle CenterX=-1.5 CenterY=10 CenterZ=0 NormalX=0 NormalY=0 NormalZ=1 AngleXU=0 Radius=1.5 StartAngle=4.71239 EndAngle=7.85398
    g23: ArcOfCircle CenterX=-1.5 CenterY=15.75 CenterZ=0 NormalX=0 NormalY=0 NormalZ=1 AngleXU=0 Radius=1.5 StartAngle=4.71239 EndAngle=7.85398
    g24: LineSegment StartX=-49.19 StartY=69.25 StartZ=0 EndX=-1.5 EndY=69.25 EndZ=0
    g25: LineSegment StartX=-49.19 StartY=66.25 StartZ=0 EndX=-1.5 EndY=66.25 EndZ=0
    g26: LineSegment StartX=-49.19 StartY=63.5 StartZ=0 EndX=-1.5 EndY=63.5 EndZ=0
    g27: LineSegment StartX=-49.19 StartY=60.5 StartZ=0 EndX=-1.5 EndY=60.5 EndZ=0
    g28: LineSegment StartX=-49.19 StartY=57.75 StartZ=0 EndX=-1.5 EndY=57.75 EndZ=0
    g29: LineSegment StartX=-49.19 StartY=54.75 StartZ=0 EndX=-1.5 EndY=54.75 EndZ=0
    g30: LineSegment StartX=-49.19 StartY=52 StartZ=0 EndX=-11.49 EndY=52 EndZ=0
    g31: LineSegment StartX=-49.19 StartY=49 StartZ=0 EndX=-11.49 EndY=49 EndZ=0
    g32: LineSegment StartX=-49.19 StartY=46.25 StartZ=0 EndX=-16.28 EndY=46.25 EndZ=0
    g33: LineSegment StartX=-49.19 StartY=43.25 StartZ=0 EndX=-16.28 EndY=43.25 EndZ=0
    g34: LineSegment StartX=-49.19 StartY=40.5 StartZ=0 EndX=-18.2337 EndY=40.5 EndZ=0
    g35: LineSegment StartX=-49.19 StartY=37.5 StartZ=0 EndX=-18.23 EndY=37.5 EndZ=0
    g36: LineSegment StartX=-49.19 StartY=34.5 StartZ=0 EndX=-18.2337 EndY=34.5 EndZ=0
    g37: LineSegment StartX=-49.19 StartY=31.5 StartZ=0 EndX=-18.23 EndY=31.5 EndZ=0
    g38: LineSegment StartX=-49.19 StartY=28.75 StartZ=0 EndX=-16.2837 EndY=28.75 EndZ=0
    g39: LineSegment StartX=-49.19 StartY=25.75 StartZ=0 EndX=-16.28 EndY=25.75 EndZ=0
    g40: LineSegment StartX=-49.19 StartY=23 StartZ=0 EndX=-11.49 EndY=23 EndZ=0
    g41: LineSegment StartX=-49.19 StartY=20 StartZ=0 EndX=-11.49 EndY=20 EndZ=0
    g42: LineSegment StartX=-49.19 StartY=17.25 StartZ=0 EndX=-1.5 EndY=17.25 EndZ=0
    g43: LineSegment StartX=-49.19 StartY=14.25 StartZ=0 EndX=-1.5 EndY=14.25 EndZ=0
    g44: LineSegment StartX=-49.19 StartY=11.5 StartZ=0 EndX=-1.5 EndY=11.5 EndZ=0
    g45: LineSegment StartX=-49.19 StartY=8.5 StartZ=0 EndX=-1.5 EndY=8.5 EndZ=0
    g46: LineSegment StartX=-49.19 StartY=5.75 StartZ=0 EndX=-1.5 EndY=5.75 EndZ=0
    g47: LineSegment StartX=-49.19 StartY=2.75 StartZ=0 EndX=-1.5 EndY=2.75 EndZ=0
  constraints (120):
    c: Vertical(g0)
    c: Distance(g0) = 3
    c: Block(g0)
    c: Vertical(g1)
    c: Distance(g1) = 3
    c: Vertical(g2)
    c: Equal(g0,g2) = 3
    c: Block(g2)
    c: Vertical(g3)
    c: Equal(g1,g3) = 3
    c: Vertical(g4)
    c: Equal(g0,g4) = 3
    c: Block(g4)
    c: Vertical(g5)
    c: Equal(g1,g5) = 3
    c: Vertical(g6)
    c: Equal(g0,g6) = 3
    c: Block(g6)
    c: Vertical(g7)
    c: Equal(g1,g7) = 3
    c: Vertical(g8)
    c: Equal(g0,g8) = 3
    c: Block(g8)
    c: Vertical(g9)
    c: Equal(g1,g9) = 3
    c: Vertical(g10)
    c: Equal(g0,g10) = 3
    c: Block(g10)
    c: Vertical(g11)
    c: Equal(g1,g11) = 3
    c: Block(g12)
    c: Block(g13)
    c: Block(g14)
    c: Block(g15)
    c: Block(g16)
    c: Block(g17)
    c: Block(g18)
    c: Block(g19)
    c: Block(g20)
    c: Block(g21)
    c: Block(g22)
    c: Block(g23)
    c: Block(g11)
    c: Block(g9)
    c: Block(g7)
    c: Block(g5)
    c: Block(g3)
    c: Block(g1)
    c: Coincident(g24,g0)
    c: Coincident(g24,g12)
    c: Horizontal(g24)
    c: Coincident(g25,g0)
    c: Coincident(g25,g12)
    c: Horizontal(g25)
    c: Coincident(g26,g1)
    c: Coincident(g26,g13)
    c: Horizontal(g26)
    c: Coincident(g27,g1)
    c: Coincident(g27,g13)
    c: Horizontal(g27)
    c: Coincident(g28,g2)
    c: Coincident(g28,g14)
    c: Horizontal(g28)
    c: Coincident(g29,g2)
    c: Coincident(g29,g14)
    c: Horizontal(g29)
    c: Coincident(g30,g3)
    c: Coincident(g30,g15)
    c: Horizontal(g30)
    c: Coincident(g31,g3)
    c: Coincident(g31,g15)
    c: Horizontal(g31)
    c: Coincident(g32,g4)
    c: Coincident(g32,g16)
    c: Horizontal(g32)
    c: Coincident(g33,g4)
    c: Coincident(g33,g16)
    c: Horizontal(g33)
    c: Coincident(g34,g5)
    c: Coincident(g34,g17)
    c: Horizontal(g34)
    c: Coincident(g35,g5)
    c: Coincident(g35,g17)
    c: Horizontal(g35)
    c: Coincident(g36,g6)
    c: Coincident(g36,g19)
    c: Horizontal(g36)
    c: Coincident(g37,g6)
    c: Coincident(g37,g19)
    c: Horizontal(g37)
    c: Coincident(g38,g7)
    c: Coincident(g38,g18)
    c: Horizontal(g38)
    c: Coincident(g39,g7)
    c: Coincident(g39,g18)
    c: Horizontal(g39)
    c: Coincident(g40,g8)
    c: Coincident(g40,g20)
    c: Horizontal(g40)
    c: Coincident(g41,g8)
    c: Coincident(g41,g20)
    c: Horizontal(g41)
    c: Coincident(g42,g9)
    c: Coincident(g42,g23)
    c: Horizontal(g42)
    c: Coincident(g43,g9)
    c: Coincident(g43,g23)
    c: Horizontal(g43)
    c: Coincident(g44,g10)
    c: Coincident(g44,g22)
    c: Horizontal(g44)
    c: Coincident(g45,g10)
    c: Coincident(g45,g22)
    c: Horizontal(g45)
    c: Coincident(g46,g11)
    c: Coincident(g46,g21)
    c: Horizontal(g46)
    c: Coincident(g47,g11)
    c: Coincident(g47,g21)
    c: Horizontal(g47)
FEATURE [Part::Extrusion] Extrude023
  Base = -> Sketch032
  Dir = (1,-2e-16,2e-16)
  DirMode = 2
  FaceMakerClass = Part::FaceMakerBullseye
  LengthFwd = 19
  LengthRev = 0
  Placement = pos=(-19,0,0) rot=(0,0,1;0rad)
  Solid = true
  Symmetric = false
FEATURE [Part::Fillet] Fillet023
  Base = -> Extrude023
  Edges = <same value as first occurrence — deduplicated (x4 in doc)>
  Placement = pos=(0,0.05,0) rot=(0,0,1;0rad)
FEATURE [Part::Cut] Cut014  label="bottom003"
  Base = -> Cut007
  Tool = -> Fusion047
FEATURE [Part::Cut] Cut021  label="bottom004"
  Base = -> Cut014
  Tool = -> Fillet023
FEATURE [Sketcher::SketchObject] Sketch033
  FullyConstrained = true
  Placement = pos=(117,19,0) rot=(0.57735,0.57735,0.57735;2.0944rad)
  sketch-geometry (8):
    g0: LineSegment StartX=-49.19 StartY=69.25 StartZ=0 EndX=-49.19 EndY=66.25 EndZ=0
    g1: LineSegment StartX=-49.19 StartY=5.75 StartZ=0 EndX=-49.19 EndY=2.75 EndZ=0
    g2: ArcOfCircle CenterX=-1.5 CenterY=67.75 CenterZ=0 NormalX=0 NormalY=0 NormalZ=1 AngleXU=0 Radius=1.5 StartAngle=4.71239 EndAngle=7.85398
    g3: ArcOfCircle CenterX=-1.5 CenterY=4.25 CenterZ=0 NormalX=0 NormalY=0 NormalZ=1 AngleXU=0 Radius=1.5 StartAngle=4.71239 EndAngle=7.85398
    g4: LineSegment StartX=-49.19 StartY=69.25 StartZ=0 EndX=-1.5 EndY=69.25 EndZ=0
    g5: LineSegment StartX=-49.19 StartY=66.25 StartZ=0 EndX=-1.5 EndY=66.25 EndZ=0
    g6: LineSegment StartX=-49.19 StartY=5.75 StartZ=0 EndX=-1.5 EndY=5.75 EndZ=0
    g7: LineSegment StartX=-49.19 StartY=2.75 StartZ=0 EndX=-1.5 EndY=2.75 EndZ=0
  constraints (19):
    c: Vertical(g0)
    c: Distance(g0) = 3
    c: Block(g0)
    c: Vertical(g1)
    c: Block(g2)
    c: Block(g3)
    c: Block(g1)
    c: Coincident(g4,g0)
    c: Coincident(g4,g2)
    c: Horizontal(g4)
    c: Coincident(g5,g0)
    c: Coincident(g5,g2)
    c: Horizontal(g5)
    c: Coincident(g6,g1)
    c: Coincident(g6,g3)
    c: Horizontal(g6)
    c: Coincident(g7,g1)
    c: Coincident(g7,g3)
    c: Horizontal(g7)
FEATURE [Sketcher::SketchObject] Sketch034
  FullyConstrained = true
  Placement = pos=(117,19,0) rot=(0.57735,0.57735,0.57735;2.0944rad)
  sketch-geometry (8):
    g0: LineSegment StartX=-49.19 StartY=63.5 StartZ=0 EndX=-49.19 EndY=60.5 EndZ=0
    g1: LineSegment StartX=-49.19 StartY=11.5 StartZ=0 EndX=-49.19 EndY=8.5 EndZ=0
    g2: ArcOfCircle CenterX=-1.5 CenterY=62 CenterZ=0 NormalX=0 NormalY=0 NormalZ=1 AngleXU=0 Radius=1.5 StartAngle=4.71239 EndAngle=7.85398
    g3: ArcOfCircle CenterX=-1.5 CenterY=10 CenterZ=0 NormalX=0 NormalY=0 NormalZ=1 AngleXU=0 Radius=1.5 StartAngle=4.71239 EndAngle=7.85398
    g4: LineSegment StartX=-49.19 StartY=63.5 StartZ=0 EndX=-1.5 EndY=63.5 EndZ=0
    g5: LineSegment StartX=-49.19 StartY=60.5 StartZ=0 EndX=-1.5 EndY=60.5 EndZ=0
    g6: LineSegment StartX=-49.19 StartY=11.5 StartZ=0 EndX=-1.5 EndY=11.5 EndZ=0
    g7: LineSegment StartX=-49.19 StartY=8.5 StartZ=0 EndX=-1.5 EndY=8.5 EndZ=0
  constraints (19):
    c: Vertical(g0)
    c: Distance(g0) = 3
    c: Vertical(g1)
    c: Block(g1)
    c: Block(g2)
    c: Block(g3)
    c: Block(g0)
    c: Coincident(g4,g0)
    c: Coincident(g4,g2)
    c: Horizontal(g4)
    c: Coincident(g5,g0)
    c: Coincident(g5,g2)
    c: Horizontal(g5)
    c: Coincident(g6,g1)
    c: Coincident(g6,g3)
    c: Horizontal(g6)
    c: Coincident(g7,g1)
    c: Coincident(g7,g3)
    c: Horizontal(g7)
FEATURE [Part::Extrusion] Extrude024
  Base = -> Sketch033
  Dir = (1,0,0)
  DirMode = 2
  FaceMakerClass = Part::FaceMakerBullseye
  LengthFwd = 10
  LengthRev = 0
  Solid = true
  Symmetric = false
FEATURE [Part::Extrusion] Extrude025
  Base = -> Sketch034
  Dir = (1,0,0)
  DirMode = 2
  FaceMakerClass = Part::FaceMakerBullseye
  LengthFwd = 10
  LengthRev = 0
  Solid = true
  Symmetric = false
FEATURE [Part::Fillet] Fillet024  label="removeFromtMoreFrontCaseScrewRetainers"
  Base = -> Extrude024
  Edges = 4 edges r=1.49: [Edge6,Edge11,Edge18,Edge23]
  Placement = pos=(-11,0,0) rot=(0,0,1;0rad)
FEATURE [Part::Fillet] Fillet025  label="removeFromtMoreFrontCaseScrewRetainers001"
  Base = -> Extrude025
  Edges = 4 edges r=1.49: [Edge6,Edge11,Edge18,Edge23]
  Placement = pos=(-19,0,0) rot=(0,0,1;0rad)
FEATURE [Part::Cut] Cut022
  Base = -> Cut015
  Tool = -> Fillet025
FEATURE [Part::Cut] Cut023  label="screwRetainers"
  Base = -> Cut022
  Tool = -> Fillet024
FEATURE [Part::MultiFuse] Fusion056  label="bottom005"
  Shapes = -> [Fusion044,Cut021]
FEATURE [Part::MultiFuse] Fusion057  label="casePillars001"
  Shapes = -> [Cut016,Fusion052]
FEATURE [Part::MultiFuse] Fusion058  label="bottom006"
  Shapes = -> [Fusion056,Cut023]
FEATURE [Part::MultiFuse] Fusion059  label="bottom007"
  Shapes = -> [Fusion058,Fillet005]
FEATURE [Part::MultiFuse] Fusion060  label="bottom008"
  Shapes = -> [Fusion059,Fusion]
FEATURE [Part::MultiFuse] Fusion061  label="top011"
  Shapes = -> [Cut006,Cut020]
FEATURE [Part::MultiFuse] Fusion062  label="top012"
  Shapes = -> [Fusion057,Fusion061]
FEATURE [Sketcher::SketchObject] Sketch035  label="topSketch007"
  FullyConstrained = true
  sketch-geometry (6):
    g0: LineSegment StartX=19 StartY=38 StartZ=0 EndX=117 EndY=38 EndZ=0
    g1: ArcOfCircle CenterX=19 CenterY=19 CenterZ=0 NormalX=0 NormalY=0 NormalZ=1 AngleXU=0 Radius=19 StartAngle=1.5708 EndAngle=3.14159
    g2: LineSegment StartX=117 StartY=38 StartZ=0 EndX=117 EndY=19 EndZ=0
    g3: LineSegment StartX=98 StartY=1.0161e-12 StartZ=0 EndX=5.22862e-06 EndY=1.0161e-12 EndZ=0
    g4: LineSegment StartX=5.22862e-06 StartY=19 StartZ=0 EndX=5.22862e-06 EndY=1.0161e-12 EndZ=0
    g5: ArcOfCircle CenterX=98 CenterY=19 CenterZ=0 NormalX=0 NormalY=0 NormalZ=1 AngleXU=0 Radius=19 StartAngle=4.71239 EndAngle=6.28319
  constraints (16):
    c: Horizontal(g0)
    c: Distance(g0) = 98
    c: Coincident(g1,g0)
    c: Block(g1)
    c: Coincident(g2,g0)
    c: Vertical(g2)
    c: Distance(g2) = 19
    c: Horizontal(g3)
    c: Coincident(g4,g1)
    c: Vertical(g4)
    c: Coincident(g3,g4)
    c: Block(g3)
    c: Coincident(g5,g2)
    c: Coincident(g5,g3)
    c: Block(g0)
    c: Block(g5)
FEATURE [Part::Extrusion] Extrude026  label="sideA001"
  Base = -> Sketch035
  Dir = (0,0,1)
  DirMode = 2
  FaceMakerClass = Part::FaceMakerBullseye
  LengthFwd = 3
  LengthRev = 0
  Placement = pos=(0,0,-2.7) rot=(0,0,1;0rad)
  Solid = true
  Symmetric = false
FEATURE [Sketcher::SketchObject] Sketch036  label="topSketch008"
  FullyConstrained = true
  sketch-geometry (6):
    g0: LineSegment StartX=19 StartY=38 StartZ=0 EndX=117 EndY=38 EndZ=0
    g1: ArcOfCircle CenterX=19 CenterY=19 CenterZ=0 NormalX=0 NormalY=0 NormalZ=1 AngleXU=0 Radius=19 StartAngle=1.5708 EndAngle=3.14159
    g2: LineSegment StartX=117 StartY=38 StartZ=0 EndX=117 EndY=19 EndZ=0
    g3: LineSegment StartX=98 StartY=1.0161e-12 StartZ=0 EndX=5.22862e-06 EndY=1.0161e-12 EndZ=0
    g4: LineSegment StartX=5.22862e-06 StartY=19 StartZ=0 EndX=5.22862e-06 EndY=1.0161e-12 EndZ=0
    g5: ArcOfCircle CenterX=98 CenterY=19 CenterZ=0 NormalX=0 NormalY=0 NormalZ=1 AngleXU=0 Radius=19 StartAngle=4.71239 EndAngle=6.28319
  constraints (16):
    c: Horizontal(g0)
    c: Distance(g0) = 98
    c: Coincident(g1,g0)
    c: Block(g1)
    c: Coincident(g2,g0)
    c: Vertical(g2)
    c: Distance(g2) = 19
    c: Horizontal(g3)
    c: Coincident(g4,g1)
    c: Vertical(g4)
    c: Coincident(g3,g4)
    c: Block(g3)
    c: Coincident(g5,g2)
    c: Coincident(g5,g3)
    c: Block(g0)
    c: Block(g5)
FEATURE [Part::Extrusion] Extrude027  label="sideB001"
  Base = -> Sketch036
  Dir = (0,0,1)
  DirMode = 2
  FaceMakerClass = Part::FaceMakerBullseye
  LengthFwd = 3
  LengthRev = 0
  Placement = pos=(0,0,71.7) rot=(0,0,1;0rad)
  Solid = true
  Symmetric = false
FEATURE [Part::MultiFuse] Fusion064  label="removeFromBottom"
  Shapes = -> [Extrude026,Extrude027]
FEATURE [Part::Cut] Cut024  label="bottom009"
  Base = -> Fusion060
  Tool = -> Fusion064
FEATURE [Sketcher::SketchObject] Sketch037  label="topSketch009"
  FullyConstrained = true
  sketch-geometry (6):
    g0: ArcOfCircle CenterX=19 CenterY=19 CenterZ=0 NormalX=0 NormalY=0 NormalZ=1 AngleXU=0 Radius=19 StartAngle=1.5708 EndAngle=3.14159
    g1: LineSegment StartX=5.22862e-06 StartY=19 StartZ=0 EndX=5.22862e-06 EndY=1.19904e-11 EndZ=0
    g2: LineSegment StartX=19 StartY=38 StartZ=0 EndX=124 EndY=38 EndZ=0
    g3: LineSegment StartX=5.22862e-06 StartY=1.19904e-11 StartZ=0 EndX=105 EndY=1.19904e-11 EndZ=0
    g4: ArcOfCircle CenterX=105 CenterY=19 CenterZ=0 NormalX=0 NormalY=0 NormalZ=1 AngleXU=0 Radius=19 StartAngle=4.71239 EndAngle=6.28319
    g5: LineSegment StartX=124 StartY=38 StartZ=0 EndX=124 EndY=19 EndZ=0
  constraints (16):
    c: Block(g0)
    c: Coincident(g1,g0)
    c: Vertical(g1)
    c: Horizontal(g2)
    c: Distance(g2) = 105
    c: Coincident(g2,g0)
    c: Distance(g1) = 19
    c: Coincident(g3,g1)
    c: Horizontal(g3)
    c: Distance(g3) = 105
    c: Block(g4)
    c: Coincident(g4,g3)
    c: Coincident(g5,g2)
    c: Coincident(g5,g4)
    c: Vertical(g5)
    c: Distance(g5) = 19
FEATURE [Part::Extrusion] Extrude028  label="sideB"
  Base = -> Sketch037
  Dir = (0,0,1)
  DirMode = 2
  FaceMakerClass = Part::FaceMakerBullseye
  LengthFwd = 3
  LengthRev = 0
  Placement = pos=(0,0,72) rot=(0,0,1;0rad)
  Solid = true
  Symmetric = false
FEATURE [Sketcher::SketchObject] Sketch038  label="topSketch010"
  FullyConstrained = true
  sketch-geometry (22):
    g0: LineSegment StartX=5.21097e-06 StartY=3 StartZ=0 EndX=5.21097e-06 EndY=19 EndZ=0
    g1: ArcOfCircle CenterX=19 CenterY=19 CenterZ=0 NormalX=0 NormalY=0 NormalZ=1 AngleXU=0 Radius=19 StartAngle=1.5708 EndAngle=3.14159
    g2: ArcOfCircle CenterX=19 CenterY=19 CenterZ=0 NormalX=0 NormalY=0 NormalZ=1 AngleXU=0 Radius=16 StartAngle=1.5708 EndAngle=3.14159
    g3: LineSegment StartX=114 StartY=35 StartZ=0 EndX=19 EndY=35 EndZ=0
    g4: LineSegment StartX=5.21097e-06 StartY=3 StartZ=0 EndX=5.21097e-06 EndY=0 EndZ=0
    g5: LineSegment StartX=3 StartY=0 StartZ=0 EndX=5.21097e-06 EndY=0 EndZ=0
    g6: LineSegment StartX=3 StartY=19 StartZ=0 EndX=3 EndY=0 EndZ=0
    g7: LineSegment StartX=19 StartY=38 StartZ=0 EndX=124 EndY=38 EndZ=0
    g8: Circle CenterX=119 CenterY=35 CenterZ=0 NormalX=0 NormalY=0 NormalZ=1 AngleXU=0 Radius=1
    g9: Circle CenterX=121 CenterY=35 CenterZ=0 NormalX=0 NormalY=0 NormalZ=1 AngleXU=0 Radius=1
    g10: Circle CenterX=121 CenterY=33 CenterZ=0 NormalX=0 NormalY=0 NormalZ=1 AngleXU=0 Radius=1
    g11: BSplineCurve PolesCount=3 KnotsCount=2 Degree=2 IsPeriodic=0
    g12: GeomPoint X=119 Y=35 Z=0
    g13: GeomPoint X=121 Y=33 Z=0
    g14: LineSegment StartX=119 StartY=35 StartZ=0 EndX=114 EndY=35 EndZ=0
    g15: ArcOfCircle CenterX=105 CenterY=19 CenterZ=0 NormalX=0 NormalY=0 NormalZ=1 AngleXU=0 Radius=16 StartAngle=5.60905 EndAngle=6.28319
    g16: LineSegment StartX=121 StartY=33 StartZ=0 EndX=121 EndY=19 EndZ=0
    g17: LineSegment StartX=117.5 StartY=9.01251 StartZ=0 EndX=121.163 EndY=9.0125 EndZ=0
    g18: ArcOfCircle CenterX=105 CenterY=19 CenterZ=0 NormalX=0 NormalY=0 NormalZ=1 AngleXU=0 Radius=20.6155 StartAngle=5.7297 EndAngle=6.28319
    g19: LineSegment StartX=121.163 StartY=9.0125 StartZ=0 EndX=122.538 EndY=8.16329 EndZ=0
    g20: LineSegment StartX=124 StartY=38 StartZ=0 EndX=125.616 EndY=38 EndZ=0
    g21: LineSegment StartX=125.616 StartY=19 StartZ=0 EndX=125.616 EndY=38 EndZ=0
  constraints (49):
    c: Vertical(g0)
    c: Block(g0)
    c: Coincident(g1,g0)
    c: Block(g1)
    c: Coincident(g2,g1)
    c: Block(g2)
    c: Coincident(g3,g2)
    c: Horizontal(g3)
    c: Tangent(g3,g2)
    c: Coincident(g4,g0)
    c: Distance(g4) = 3
    c: Vertical(g4)
    c: Coincident(g5,g4)
    c: Horizontal(g5)
    c: Coincident(g6,g2)
    c: Coincident(g6,g5)
    c: Vertical(g6)
    c: Horizontal(g7)
    c: Distance(g7) = 105
    c: Coincident(g7,g1)
    c: Block(g3)
    c: Weight(g8) = 1
    c: Equal(g8,g9)
    c: Equal(g8,g10)
    c: InternalAlignment(g8,g11)
    c: InternalAlignment(g9,g11)
    c: InternalAlignment(g10,g11)
    c: InternalAlignment(g12,g11)
    c: InternalAlignment(g13,g11)
    c: Block(g11)
    c: Coincident(g14,g11)
    c: Coincident(g14,g3)
    c: Horizontal(g14)
    c: Block(g15)
    c: Coincident(g16,g11)
    c: Coincident(g16,g15)
    c: Vertical(g16)
    c: Distance(g16) = 14
    c: Coincident(g17,g15)
    c: Block(g18)
    c: Coincident(g19,g18)
    c: Coincident(g20,g7)
    c: Horizontal(g20)
    c: Vertical(g21)
    c: Coincident(g20,g21)
    c: Block(g20)
    c: Block(g21)
    c: Block(g19)
    c: Block(g17)
FEATURE [Part::Extrusion] Extrude029
  Base = -> Sketch038
  Dir = (0,0,1)
  DirMode = 2
  FaceMakerClass = Part::FaceMakerBullseye
  LengthFwd = 72
  LengthRev = 0
  Solid = true
  Symmetric = false
FEATURE [Part::Feature] Face085
  shape: bbox 4.8 x 25.5 x 2e-07 mm, 1 faces, 0 solids (baked)
FEATURE [Part::Revolution] Revolve089  label="moreFrontCaseScrewPost003"
  Angle = 360
  Axis = (0,1,0)
  Base = (0,0,0)
  FaceMakerClass = Part::FaceMakerBullseye
  Placement = pos=(109.5,4.5,3.5) rot=(0,0,1;0rad)
  Solid = false
  Source = -> Face085
  Symmetric = false
FEATURE [Part::Feature] Face086
  shape: bbox 4.8 x 25.5 x 2e-07 mm, 1 faces, 0 solids (baked)
FEATURE [Part::Revolution] Revolve090  label="moreFrontCaseScrewPost004"
  Angle = 360
  Axis = (0,1,0)
  Base = (0,0,0)
  FaceMakerClass = Part::FaceMakerBullseye
  Placement = pos=(109.5,4.5,68.5) rot=(0,0,1;0rad)
  Solid = false
  Source = -> Face086
  Symmetric = false
FEATURE [Part::Fillet] Fillet026  label="top013"
  Base = -> Extrude029
  Edges = 1 edges r=2: [Edge35]
FEATURE [Sketcher::SketchObject] Sketch039
  FullyConstrained = true
  sketch-geometry (7):
    g0: LineSegment StartX=0 StartY=0 StartZ=0 EndX=0 EndY=6 EndZ=0
    g1: Circle CenterX=0 CenterY=0 CenterZ=0 NormalX=0 NormalY=0 NormalZ=1 AngleXU=0 Radius=1
    g2: Circle CenterX=8 CenterY=6 CenterZ=0 NormalX=0 NormalY=0 NormalZ=1 AngleXU=0 Radius=1
    g3: BSplineCurve PolesCount=3 KnotsCount=2 Degree=2 IsPeriodic=0
    g4: GeomPoint X=0 Y=0 Z=0
    g5: GeomPoint X=8 Y=6 Z=0
    g6: LineSegment StartX=0 StartY=6 StartZ=0 EndX=8 EndY=6 EndZ=0
  constraints (14):
    c: Coincident(g0,g-1)
    c: Distance(g0) = 6
    c: Vertical(g0)
    c: Coincident(g3,g0)
    c: Weight(g1) = 1
    c: Equal(g1,g2)
    c: InternalAlignment(g1,g3)
    c: InternalAlignment(g2,g3)
    c: InternalAlignment(g4,g3)
    c: InternalAlignment(g5,g3)
    c: Block(g3)
    c: Coincident(g6,g0)
    c: Coincident(g6,g3)
    c: Horizontal(g6)
FEATURE [Sketcher::SketchObject] Sketch040
  FullyConstrained = true
  sketch-geometry (7):
    g0: LineSegment StartX=0 StartY=0 StartZ=0 EndX=0 EndY=6 EndZ=0
    g1: Circle CenterX=0 CenterY=0 CenterZ=0 NormalX=0 NormalY=0 NormalZ=1 AngleXU=0 Radius=1
    g2: Circle CenterX=8 CenterY=6 CenterZ=0 NormalX=0 NormalY=0 NormalZ=1 AngleXU=0 Radius=1
    g3: BSplineCurve PolesCount=3 KnotsCount=2 Degree=2 IsPeriodic=0
    g4: GeomPoint X=0 Y=0 Z=0
    g5: GeomPoint X=8 Y=6 Z=0
    g6: LineSegment StartX=0 StartY=6 StartZ=0 EndX=8 EndY=6 EndZ=0
  constraints (14):
    c: Coincident(g0,g-1)
    c: Distance(g0) = 6
    c: Vertical(g0)
    c: Coincident(g3,g0)
    c: Weight(g1) = 1
    c: Equal(g1,g2)
    c: InternalAlignment(g1,g3)
    c: InternalAlignment(g2,g3)
    c: InternalAlignment(g4,g3)
    c: InternalAlignment(g5,g3)
    c: Block(g3)
    c: Coincident(g6,g0)
    c: Coincident(g6,g3)
    c: Horizontal(g6)
FEATURE [Sketcher::SketchObject] Sketch041
  FullyConstrained = true
  sketch-geometry (7):
    g0: LineSegment StartX=0 StartY=0 StartZ=0 EndX=0 EndY=6 EndZ=0
    g1: Circle CenterX=0 CenterY=0 CenterZ=0 NormalX=0 NormalY=0 NormalZ=1 AngleXU=0 Radius=1
    g2: Circle CenterX=8 CenterY=6 CenterZ=0 NormalX=0 NormalY=0 NormalZ=1 AngleXU=0 Radius=1
    g3: BSplineCurve PolesCount=3 KnotsCount=2 Degree=2 IsPeriodic=0
    g4: GeomPoint X=0 Y=0 Z=0
    g5: GeomPoint X=8 Y=6 Z=0
    g6: LineSegment StartX=0 StartY=6 StartZ=0 EndX=8 EndY=6 EndZ=0
  constraints (14):
    c: Coincident(g0,g-1)
    c: Distance(g0) = 6
    c: Vertical(g0)
    c: Coincident(g3,g0)
    c: Weight(g1) = 1
    c: Equal(g1,g2)
    c: InternalAlignment(g1,g3)
    c: InternalAlignment(g2,g3)
    c: InternalAlignment(g4,g3)
    c: InternalAlignment(g5,g3)
    c: Block(g3)
    c: Coincident(g6,g0)
    c: Coincident(g6,g3)
    c: Horizontal(g6)
FEATURE [Sketcher::SketchObject] Sketch042
  FullyConstrained = true
  sketch-geometry (7):
    g0: LineSegment StartX=0 StartY=0 StartZ=0 EndX=0 EndY=6 EndZ=0
    g1: Circle CenterX=0 CenterY=0 CenterZ=0 NormalX=0 NormalY=0 NormalZ=1 AngleXU=0 Radius=1
    g2: Circle CenterX=8 CenterY=6 CenterZ=0 NormalX=0 NormalY=0 NormalZ=1 AngleXU=0 Radius=1
    g3: BSplineCurve PolesCount=3 KnotsCount=2 Degree=2 IsPeriodic=0
    g4: GeomPoint X=0 Y=0 Z=0
    g5: GeomPoint X=8 Y=6 Z=0
    g6: LineSegment StartX=0 StartY=6 StartZ=0 EndX=8 EndY=6 EndZ=0
  constraints (14):
    c: Coincident(g0,g-1)
    c: Distance(g0) = 6
    c: Vertical(g0)
    c: Coincident(g3,g0)
    c: Weight(g1) = 1
    c: Equal(g1,g2)
    c: InternalAlignment(g1,g3)
    c: InternalAlignment(g2,g3)
    c: InternalAlignment(g4,g3)
    c: InternalAlignment(g5,g3)
    c: Block(g3)
    c: Coincident(g6,g0)
    c: Coincident(g6,g3)
    c: Horizontal(g6)
FEATURE [Part::Extrusion] Extrude030  label="caseScrewPillarBracket008"
  Base = -> Sketch039
  Dir = (0,0,1)
  DirMode = 2
  FaceMakerClass = Part::FaceMakerBullseye
  LengthFwd = 2.4
  LengthRev = 0
  Placement = pos=(15.76,29,8.8) rot=(0,1,0;0rad)
  Solid = true
  Symmetric = false
FEATURE [Part::Extrusion] Extrude031  label="caseScrewPillarBracket009"
  Base = -> Sketch040
  Dir = (0,0,1)
  DirMode = 2
  FaceMakerClass = Part::FaceMakerBullseye
  LengthFwd = 2.4
  LengthRev = 0
  Placement = pos=(15.76,29,60.8) rot=(0,0,1;0rad)
  Solid = true
  Symmetric = false
FEATURE [Part::Extrusion] Extrude032  label="caseScrewPillarBracket010"
  Base = -> Sketch041
  Dir = (0,0,1)
  DirMode = 2
  FaceMakerClass = Part::FaceMakerBullseye
  LengthFwd = 2.4
  LengthRev = 0
  Placement = pos=(13.7,29,13.26) rot=(0,-1,0;1.5708rad)
  Solid = true
  Symmetric = false
FEATURE [Part::Extrusion] Extrude033  label="caseScrewPillarBracket011"
  Base = -> Sketch042
  Dir = (0,0,1)
  DirMode = 2
  FaceMakerClass = Part::FaceMakerBullseye
  LengthFwd = 2.4
  LengthRev = 0
  Placement = pos=(11.3,29,58.74) rot=(0,1,0;1.5708rad)
  Solid = true
  Symmetric = false
FEATURE [Sketcher::SketchObject] Sketch043
  FullyConstrained = true
  sketch-geometry (7):
    g0: LineSegment StartX=0 StartY=0 StartZ=0 EndX=0 EndY=6 EndZ=0
    g1: Circle CenterX=0 CenterY=0 CenterZ=0 NormalX=0 NormalY=0 NormalZ=1 AngleXU=0 Radius=1
    g2: Circle CenterX=8 CenterY=6 CenterZ=0 NormalX=0 NormalY=0 NormalZ=1 AngleXU=0 Radius=1
    g3: BSplineCurve PolesCount=3 KnotsCount=2 Degree=2 IsPeriodic=0
    g4: GeomPoint X=0 Y=0 Z=0
    g5: GeomPoint X=8 Y=6 Z=0
    g6: LineSegment StartX=0 StartY=6 StartZ=0 EndX=8 EndY=6 EndZ=0
  constraints (14):
    c: Coincident(g0,g-1)
    c: Distance(g0) = 6
    c: Vertical(g0)
    c: Coincident(g3,g0)
    c: Weight(g1) = 1
    c: Equal(g1,g2)
    c: InternalAlignment(g1,g3)
    c: InternalAlignment(g2,g3)
    c: InternalAlignment(g4,g3)
    c: InternalAlignment(g5,g3)
    c: Block(g3)
    c: Coincident(g6,g0)
    c: Coincident(g6,g3)
    c: Horizontal(g6)
FEATURE [Part::Extrusion] Extrude034  label="caseScrewPillarBracket012"
  Base = -> Sketch043
  Dir = (0,0,1)
  DirMode = 2
  FaceMakerClass = Part::FaceMakerBullseye
  LengthFwd = 2.4
  LengthRev = 0
  Placement = pos=(88.3,29,65.23) rot=(0,1,0;1.5708rad)
  Solid = true
  Symmetric = false
FEATURE [Sketcher::SketchObject] Sketch044
  FullyConstrained = true
  sketch-geometry (7):
    g0: LineSegment StartX=0 StartY=0 StartZ=0 EndX=0 EndY=6 EndZ=0
    g1: Circle CenterX=0 CenterY=0 CenterZ=0 NormalX=0 NormalY=0 NormalZ=1 AngleXU=0 Radius=1
    g2: Circle CenterX=8 CenterY=6 CenterZ=0 NormalX=0 NormalY=0 NormalZ=1 AngleXU=0 Radius=1
    g3: BSplineCurve PolesCount=3 KnotsCount=2 Degree=2 IsPeriodic=0
    g4: GeomPoint X=0 Y=0 Z=0
    g5: GeomPoint X=8 Y=6 Z=0
    g6: LineSegment StartX=0 StartY=6 StartZ=0 EndX=8 EndY=6 EndZ=0
  constraints (14):
    c: Coincident(g0,g-1)
    c: Distance(g0) = 6
    c: Vertical(g0)
    c: Coincident(g3,g0)
    c: Weight(g1) = 1
    c: Equal(g1,g2)
    c: InternalAlignment(g1,g3)
    c: InternalAlignment(g2,g3)
    c: InternalAlignment(g4,g3)
    c: InternalAlignment(g5,g3)
    c: Block(g3)
    c: Coincident(g6,g0)
    c: Coincident(g6,g3)
    c: Horizontal(g6)
FEATURE [Part::Extrusion] Extrude035  label="caseScrewPillarBracket013"
  Base = -> Sketch044
  Dir = (0,0,1)
  DirMode = 2
  FaceMakerClass = Part::FaceMakerBullseye
  LengthFwd = 2.4
  LengthRev = 0
  Placement = pos=(90.7,29,6.77) rot=(0,-1,0;1.5708rad)
  Solid = true
  Symmetric = false
FEATURE [Sketcher::SketchObject] Sketch045
  FullyConstrained = true
  sketch-geometry (7):
    g0: LineSegment StartX=0 StartY=0 StartZ=0 EndX=0 EndY=6 EndZ=0
    g1: Circle CenterX=0 CenterY=0 CenterZ=0 NormalX=0 NormalY=0 NormalZ=1 AngleXU=0 Radius=1
    g2: Circle CenterX=8 CenterY=6 CenterZ=0 NormalX=0 NormalY=0 NormalZ=1 AngleXU=0 Radius=1
    g3: BSplineCurve PolesCount=3 KnotsCount=2 Degree=2 IsPeriodic=0
    g4: GeomPoint X=0 Y=0 Z=0
    g5: GeomPoint X=8 Y=6 Z=0
    g6: LineSegment StartX=0 StartY=6 StartZ=0 EndX=8 EndY=6 EndZ=0
  constraints (14):
    c: Coincident(g0,g-1)
    c: Distance(g0) = 6
    c: Vertical(g0)
    c: Coincident(g3,g0)
    c: Weight(g1) = 1
    c: Equal(g1,g2)
    c: InternalAlignment(g1,g3)
    c: InternalAlignment(g2,g3)
    c: InternalAlignment(g4,g3)
    c: InternalAlignment(g5,g3)
    c: Block(g3)
    c: Coincident(g6,g0)
    c: Coincident(g6,g3)
    c: Horizontal(g6)
FEATURE [Sketcher::SketchObject] Sketch046
  FullyConstrained = true
  sketch-geometry (7):
    g0: LineSegment StartX=0 StartY=0 StartZ=0 EndX=0 EndY=6 EndZ=0
    g1: Circle CenterX=0 CenterY=0 CenterZ=0 NormalX=0 NormalY=0 NormalZ=1 AngleXU=0 Radius=1
    g2: Circle CenterX=8 CenterY=6 CenterZ=0 NormalX=0 NormalY=0 NormalZ=1 AngleXU=0 Radius=1
    g3: BSplineCurve PolesCount=3 KnotsCount=2 Degree=2 IsPeriodic=0
    g4: GeomPoint X=0 Y=0 Z=0
    g5: GeomPoint X=8 Y=6 Z=0
    g6: LineSegment StartX=0 StartY=6 StartZ=0 EndX=8 EndY=6 EndZ=0
  constraints (14):
    c: Coincident(g0,g-1)
    c: Distance(g0) = 6
    c: Vertical(g0)
    c: Coincident(g3,g0)
    c: Weight(g1) = 1
    c: Equal(g1,g2)
    c: InternalAlignment(g1,g3)
    c: InternalAlignment(g2,g3)
    c: InternalAlignment(g4,g3)
    c: InternalAlignment(g5,g3)
    c: Block(g3)
    c: Coincident(g6,g0)
    c: Coincident(g6,g3)
    c: Horizontal(g6)
FEATURE [Part::Extrusion] Extrude036  label="caseScrewPillarBracket014"
  Base = -> Sketch045
  Dir = (0,0,1)
  DirMode = 2
  FaceMakerClass = Part::FaceMakerBullseye
  LengthFwd = 2.4
  LengthRev = 0
  Placement = pos=(110.7,29,6.77) rot=(0,-1,0;1.5708rad)
  Solid = true
  Symmetric = false
FEATURE [Part::Extrusion] Extrude037  label="caseScrewPillarBracket015"
  Base = -> Sketch046
  Dir = (0,0,1)
  DirMode = 2
  FaceMakerClass = Part::FaceMakerBullseye
  LengthFwd = 2.4
  LengthRev = 0
  Placement = pos=(108.3,29,65.23) rot=(0,1,0;1.5708rad)
  Solid = true
  Symmetric = false
FEATURE [Part::Box] Box013  label="frontCaseScrewPillarBracket002"
  AttacherType = Attacher::AttachEngine3D
  Height = 2.4
  Length = 22
  Placement = pos=(87,28,2.3) rot=(0,0,1;0rad)
  Width = 7
FEATURE [Part::Box] Box014  label="frontCaseScrewPillarBracket003"
  AttacherType = Attacher::AttachEngine3D
  Height = 2.4
  Length = 22
  Placement = pos=(87,28,67.3) rot=(0,0,1;0rad)
  Width = 7
FEATURE [Part::Feature] Face087
  shape: bbox 4.8 x 30.2 x 2e-07 mm, 1 faces, 0 solids (baked)
FEATURE [Part::Revolution] Revolve091  label="frontCaseScrewPost004"
  Angle = 360
  Axis = (0,1,0)
  Base = (0,0,0)
  FaceMakerClass = Part::FaceMakerBullseye
  Placement = pos=(89.5,4.5,3.5) rot=(0,0,1;0rad)
  Solid = false
  Source = -> Face087
  Symmetric = false
FEATURE [Part::Feature] Face088
  shape: bbox 4.8 x 30.2 x 2e-07 mm, 1 faces, 0 solids (baked)
FEATURE [Part::Revolution] Revolve092  label="frontCaseScrewPost005"
  Angle = 360
  Axis = (0,1,0)
  Base = (0,0,0)
  FaceMakerClass = Part::FaceMakerBullseye
  Placement = pos=(89.5,4.5,68.5) rot=(0,0,1;0rad)
  Solid = false
  Source = -> Face088
  Symmetric = false
FEATURE [Part::Feature] Face089
  shape: bbox 3.5 x 30.2 x 2e-07 mm, 1 faces, 0 solids (baked)
FEATURE [Part::Revolution] Revolve093  label="backCaseScrewPost002"
  Angle = 360
  Axis = (0,1,0)
  Base = (0,0,0)
  FaceMakerClass = Part::FaceMakerBullseye
  Placement = pos=(12.5,4.5,10) rot=(0,0,1;0rad)
  Solid = false
  Source = -> Face089
  Symmetric = false
FEATURE [Part::Feature] Face090
  shape: bbox 3.5 x 30.2 x 2e-07 mm, 1 faces, 0 solids (baked)
FEATURE [Part::Revolution] Revolve094  label="backCaseScrewPost003"
  Angle = 360
  Axis = (0,1,0)
  Base = (0,0,0)
  FaceMakerClass = Part::FaceMakerBullseye
  Placement = pos=(12.5,4.5,62) rot=(0,0,1;0rad)
  Solid = false
  Source = -> Face090
  Symmetric = false
FEATURE [Part::Box] Box015  label="Cube011"
  AttacherType = Attacher::AttachEngine3D
  Height = 28.8
  Length = 3
  Placement = pos=(107.3,28,21.6) rot=(0,0,1;0rad)
  Width = 7
FEATURE [Part::Box] Box016  label="Cube012"
  AttacherType = Attacher::AttachEngine3D
  Height = 3
  Length = 7.4
  Placement = pos=(107.3,28,18.6) rot=(0,0,1;0rad)
  Width = 7
FEATURE [Part::Box] Box017  label="Cube013"
  AttacherType = Attacher::AttachEngine3D
  Height = 3
  Length = 7.4
  Placement = pos=(107.3,28,50.4) rot=(0,0,1;0rad)
  Width = 7
FEATURE [Part::Cylinder] Cylinder024
  Angle = 360
  AttacherType = Attacher::AttachEngine3D
  Height = 20
  Placement = pos=(0,0,36.15) rot=(0,0,1;0rad)
  Radius = 14.3
FEATURE [Part::Cylinder] Cylinder025
  Angle = 360
  AttacherType = Attacher::AttachEngine3D
  Height = 10
  Placement = pos=(0,0,36.15) rot=(0,0,1;0rad)
  Radius = 4
FEATURE [Part::MultiFuse] Fusion066  label="removeToCreteHoleForPlugHousing009"
  Placement = pos=(70,19,36) rot=(0,1,0;1.5708rad)
  Shapes = -> [Cylinder024,Cylinder025]
FEATURE [Part::MultiFuse] Fusion065  label="plugHousingBracketHolder002"
  Shapes = -> [Box017,Box015,Box016]
FEATURE [Part::Cut] Cut025  label="plugHousingBracketHolder003"
  Base = -> Fusion065
  Placement = pos=(7,0,0) rot=(0,0,1;0rad)
  Tool = -> Fusion066
FEATURE [Sketcher::SketchObject] Sketch047
  FullyConstrained = false
  Placement = pos=(0,0,0) rot=(1,0,0;1.5708rad)
  sketch-geometry (24):
    g0: ArcOfCircle CenterX=-4 CenterY=-10.5 CenterZ=0 NormalX=0 NormalY=0 NormalZ=1 AngleXU=0 Radius=1.5 StartAngle=6e-16 EndAngle=3.14159
    g1: ArcOfCircle CenterX=-34.2 CenterY=-10.5 CenterZ=0 NormalX=0 NormalY=0 NormalZ=1 AngleXU=0 Radius=1.5 StartAngle=0 EndAngle=3.14159
    g2: ArcOfCircle CenterX=-34.2 CenterY=-27.7 CenterZ=0 NormalX=0 NormalY=0 NormalZ=1 AngleXU=0 Radius=1.5 StartAngle=3.14159 EndAngle=6.28319
    g3: ArcOfCircle CenterX=-4 CenterY=-27.7 CenterZ=0 NormalX=0 NormalY=0 NormalZ=1 AngleXU=0 Radius=1.5 StartAngle=3.1416 EndAngle=6.28319
    g4: ArcOfCircle CenterX=-10 CenterY=-4.3 CenterZ=0 NormalX=0 NormalY=0 NormalZ=1 AngleXU=0 Radius=1.5 StartAngle=2e-16 EndAngle=3.14159
    g5: ArcOfCircle CenterX=-16.1 CenterY=-1.8 CenterZ=0 NormalX=0 NormalY=0 NormalZ=1 AngleXU=0 Radius=1.5 StartAngle=5e-16 EndAngle=3.14159
    g6: ArcOfCircle CenterX=-22.1 CenterY=-1.8 CenterZ=0 NormalX=0 NormalY=0 NormalZ=1 AngleXU=0 Radius=1.5 StartAngle=5e-16 EndAngle=3.14159
    g7: ArcOfCircle CenterX=-28.2 CenterY=-4.3 CenterZ=0 NormalX=0 NormalY=0 NormalZ=1 AngleXU=0 Radius=1.5 StartAngle=2e-16 EndAngle=3.14159
    g8: ArcOfCircle CenterX=-10 CenterY=-33.9 CenterZ=0 NormalX=0 NormalY=0 NormalZ=1 AngleXU=0 Radius=1.5 StartAngle=3.14159 EndAngle=6.28319
    g9: ArcOfCircle CenterX=-16.1 CenterY=-36.4 CenterZ=0 NormalX=0 NormalY=0 NormalZ=1 AngleXU=0 Radius=1.5 StartAngle=3.14159 EndAngle=6.28319
    g10: ArcOfCircle CenterX=-22.1 CenterY=-36.4 CenterZ=0 NormalX=0 NormalY=0 NormalZ=1 AngleXU=0 Radius=1.5 StartAngle=3.14159 EndAngle=6.28319
    g11: ArcOfCircle CenterX=-28.2 CenterY=-33.9 CenterZ=0 NormalX=0 NormalY=0 NormalZ=1 AngleXU=0 Radius=1.5 StartAngle=3.14159 EndAngle=6.28319
    g12: LineSegment StartX=-35.7 StartY=-10.5 StartZ=0 EndX=-35.7 EndY=-27.7 EndZ=0
    g13: LineSegment StartX=-32.7 StartY=-10.5 StartZ=0 EndX=-32.7 EndY=-27.7 EndZ=0
    g14: LineSegment StartX=-29.7 StartY=-33.9 StartZ=0 EndX=-29.7 EndY=-4.3 EndZ=0
    g15: LineSegment StartX=-26.7 StartY=-33.9 StartZ=0 EndX=-26.7 EndY=-4.3 EndZ=0
    g16: LineSegment StartX=-2.5 StartY=-10.5 StartZ=0 EndX=-2.5 EndY=-27.7 EndZ=0
    g17: LineSegment StartX=-8.5 StartY=-4.3 StartZ=0 EndX=-8.5 EndY=-33.9 EndZ=0
    g18: LineSegment StartX=-5.5 StartY=-10.5 StartZ=0 EndX=-5.5 EndY=-27.7 EndZ=0
    g19: LineSegment StartX=-11.5 StartY=-4.3 StartZ=0 EndX=-11.5 EndY=-33.9 EndZ=0
    g20: LineSegment StartX=-14.6 StartY=-1.8 StartZ=0 EndX=-14.6 EndY=-36.4 EndZ=0
    g21: LineSegment StartX=-17.6 StartY=-1.8 StartZ=0 EndX=-17.6 EndY=-36.4 EndZ=0
    g22: LineSegment StartX=-20.6 StartY=-36.4 StartZ=0 EndX=-20.6 EndY=-1.8 EndZ=0
    g23: LineSegment StartX=-23.6 StartY=-1.8 StartZ=0 EndX=-23.6 EndY=-36.4 EndZ=0
  constraints (48):
    c: Block(g0)
    c: Block(g1)
    c: Block(g2)
    c: Block(g3)
    c: Block(g4)
    c: Block(g5)
    c: Block(g6)
    c: Block(g7)
    c: Block(g8)
    c: Block(g9)
    c: Block(g10)
    c: Block(g11)
    c: Coincident(g12,g1)
    c: Coincident(g12,g2)
    c: Vertical(g12)
    c: Coincident(g13,g1)
    c: Coincident(g13,g2)
    c: Vertical(g13)
    c: Coincident(g14,g11)
    c: Coincident(g14,g7)
    c: Vertical(g14)
    c: Coincident(g15,g11)
    c: Coincident(g15,g7)
    c: Vertical(g15)
    c: Coincident(g16,g0)
    c: Coincident(g16,g3)
    c: Vertical(g16)
    c: Coincident(g17,g4)
    c: Coincident(g17,g8)
    c: Vertical(g17)
    c: Coincident(g18,g0)
    c: Coincident(g18,g3)
    c: Vertical(g18)
    c: Coincident(g19,g4)
    c: Coincident(g19,g8)
    c: Vertical(g19)
    c: Coincident(g20,g5)
    c: Coincident(g20,g9)
    c: Vertical(g20)
    c: Coincident(g21,g5)
    c: Coincident(g21,g9)
    c: Vertical(g21)
    c: Coincident(g22,g10)
    c: Coincident(g22,g6)
    c: Vertical(g22)
    c: Coincident(g23,g6)
    c: Coincident(g23,g10)
    c: Vertical(g23)
FEATURE [Part::Extrusion] Extrude038  label="removeToCreateFanGrillHoles001"
  Base = -> Sketch047
  Dir = (0,-1,6e-16)
  DirMode = 2
  FaceMakerClass = Part::FaceMakerBullseye
  LengthFwd = 10
  LengthRev = 0
  Placement = pos=(65.4,44,54.82) rot=(0,0,1;0rad)
  Solid = true
  Symmetric = false
FEATURE [Part::Feature] Wire004
  shape: bbox 11 x 5.2 x 2e-07 mm, 0 faces, 0 solids (baked)
FEATURE [Part::Revolution] Revolve095
  Angle = 360
  Axis = (0,1,0)
  Base = (0,0,0)
  FaceMakerClass = Part::FaceMakerBullseye
  Placement = pos=(30.3,38,19.7) rot=(0,0,1;0rad)
  Solid = true
  Source = -> Wire004
  Symmetric = false
FEATURE [Part::Feature] Wire005
  shape: bbox 11 x 5.2 x 2e-07 mm, 0 faces, 0 solids (baked)
FEATURE [Part::Revolution] Revolve096
  Angle = 360
  Axis = (0,1,0)
  Base = (0,0,0)
  FaceMakerClass = Part::FaceMakerBullseye
  Placement = pos=(30.3,38,51.7) rot=(0,0,1;0rad)
  Solid = true
  Source = -> Wire005
  Symmetric = false
FEATURE [Part::Feature] Wire006
  shape: bbox 11 x 5.2 x 2e-07 mm, 0 faces, 0 solids (baked)
FEATURE [Part::Revolution] Revolve097
  Angle = 360
  Axis = (0,1,0)
  Base = (0,0,0)
  FaceMakerClass = Part::FaceMakerBullseye
  Placement = pos=(62.3,38,51.7) rot=(0,0,1;0rad)
  Solid = true
  Source = -> Wire006
  Symmetric = false
FEATURE [Part::Feature] Wire007
  shape: bbox 11 x 5.2 x 2e-07 mm, 0 faces, 0 solids (baked)
FEATURE [Part::Revolution] Revolve098
  Angle = 360
  Axis = (0,1,0)
  Base = (0,0,0)
  FaceMakerClass = Part::FaceMakerBullseye
  Placement = pos=(62.3,38,19.7) rot=(0,0,1;0rad)
  Solid = true
  Source = -> Wire007
  Symmetric = false
FEATURE [Part::MultiFuse] Fusion067  label="fanScrewHousing002"
  Shapes = -> [Revolve098,Revolve097,Revolve096,Revolve095]
FEATURE [Part::Feature] Face091 .. Face094  x4 (patterned run collapsed; names and placements below)
  shape: bbox 3.5 x 17.8 x 2e-07 mm, 1 faces, 0 solids (baked)
FEATURE [Part::Revolution] Revolve099  label="removeToCreateScrewAndThreadedInsertHole026"
  Angle = 360
  Axis = (0,1,0)
  Base = (0,0,0)
  FaceMakerClass = Part::FaceMakerBullseye
  Placement = pos=(62.3,30.3,19.7) rot=(0,0,1;0rad)
  Solid = false
  Source = -> Face091
  Symmetric = false
FEATURE [Part::Revolution] Revolve100  label="removeToCreateScrewAndThreadedInsertHole027"
  Angle = 360
  Axis = (0,1,0)
  Base = (0,0,0)
  FaceMakerClass = Part::FaceMakerBullseye
  Placement = pos=(62.3,30.3,51.7) rot=(0,0,1;0rad)
  Solid = false
  Source = -> Face092
  Symmetric = false
FEATURE [Part::Revolution] Revolve101  label="removeToCreateScrewAndThreadedInsertHole028"
  Angle = 360
  Axis = (0,1,0)
  Base = (0,0,0)
  FaceMakerClass = Part::FaceMakerBullseye
  Placement = pos=(30.3,30.3,19.7) rot=(0,0,1;0rad)
  Solid = false
  Source = -> Face093
  Symmetric = false
FEATURE [Part::Revolution] Revolve102  label="removeToCreateScrewAndThreadedInsertHole029"
  Angle = 360
  Axis = (0,1,0)
  Base = (0,0,0)
  FaceMakerClass = Part::FaceMakerBullseye
  Placement = pos=(30.3,30.3,51.7) rot=(0,0,1;0rad)
  Solid = false
  Source = -> Face094
  Symmetric = false
FEATURE [Part::MultiFuse] Fusion068  label="createThreadedInsertHolesForFan002"
  Shapes = -> [Revolve099,Revolve100,Revolve101,Revolve102]
FEATURE [Part::Cut] Cut026  label="fanScrewHousing003"
  Base = -> Fusion067
  Tool = -> Fusion068
FEATURE [Sketcher::SketchObject] Sketch048
  FullyConstrained = false
  Placement = pos=(0,0,0) rot=(1,0,0;1.5708rad)
  sketch-geometry (24):
    g0: ArcOfCircle CenterX=-4 CenterY=-10.5 CenterZ=0 NormalX=0 NormalY=0 NormalZ=1 AngleXU=0 Radius=1.5 StartAngle=6e-16 EndAngle=3.14159
    g1: ArcOfCircle CenterX=-34.2 CenterY=-10.5 CenterZ=0 NormalX=0 NormalY=0 NormalZ=1 AngleXU=0 Radius=1.5 StartAngle=0 EndAngle=3.14159
    g2: ArcOfCircle CenterX=-34.2 CenterY=-27.7 CenterZ=0 NormalX=0 NormalY=0 NormalZ=1 AngleXU=0 Radius=1.5 StartAngle=3.14159 EndAngle=6.28319
    g3: ArcOfCircle CenterX=-4 CenterY=-27.7 CenterZ=0 NormalX=0 NormalY=0 NormalZ=1 AngleXU=0 Radius=1.5 StartAngle=3.1416 EndAngle=6.28319
    g4: ArcOfCircle CenterX=-10 CenterY=-4.3 CenterZ=0 NormalX=0 NormalY=0 NormalZ=1 AngleXU=0 Radius=1.5 StartAngle=2e-16 EndAngle=3.14159
    g5: ArcOfCircle CenterX=-16.1 CenterY=-1.8 CenterZ=0 NormalX=0 NormalY=0 NormalZ=1 AngleXU=0 Radius=1.5 StartAngle=5e-16 EndAngle=3.14159
    g6: ArcOfCircle CenterX=-22.1 CenterY=-1.8 CenterZ=0 NormalX=0 NormalY=0 NormalZ=1 AngleXU=0 Radius=1.5 StartAngle=5e-16 EndAngle=3.14159
    g7: ArcOfCircle CenterX=-28.2 CenterY=-4.3 CenterZ=0 NormalX=0 NormalY=0 NormalZ=1 AngleXU=0 Radius=1.5 StartAngle=2e-16 EndAngle=3.14159
    g8: ArcOfCircle CenterX=-10 CenterY=-33.9 CenterZ=0 NormalX=0 NormalY=0 NormalZ=1 AngleXU=0 Radius=1.5 StartAngle=3.14159 EndAngle=6.28319
    g9: ArcOfCircle CenterX=-16.1 CenterY=-36.4 CenterZ=0 NormalX=0 NormalY=0 NormalZ=1 AngleXU=0 Radius=1.5 StartAngle=3.14159 EndAngle=6.28319
    g10: ArcOfCircle CenterX=-22.1 CenterY=-36.4 CenterZ=0 NormalX=0 NormalY=0 NormalZ=1 AngleXU=0 Radius=1.5 StartAngle=3.14159 EndAngle=6.28319
    g11: ArcOfCircle CenterX=-28.2 CenterY=-33.9 CenterZ=0 NormalX=0 NormalY=0 NormalZ=1 AngleXU=0 Radius=1.5 StartAngle=3.14159 EndAngle=6.28319
    g12: LineSegment StartX=-35.7 StartY=-10.5 StartZ=0 EndX=-35.7 EndY=-27.7 EndZ=0
    g13: LineSegment StartX=-32.7 StartY=-10.5 StartZ=0 EndX=-32.7 EndY=-27.7 EndZ=0
    g14: LineSegment StartX=-29.7 StartY=-33.9 StartZ=0 EndX=-29.7 EndY=-4.3 EndZ=0
    g15: LineSegment StartX=-26.7 StartY=-33.9 StartZ=0 EndX=-26.7 EndY=-4.3 EndZ=0
    g16: LineSegment StartX=-2.5 StartY=-10.5 StartZ=0 EndX=-2.5 EndY=-27.7 EndZ=0
    g17: LineSegment StartX=-8.5 StartY=-4.3 StartZ=0 EndX=-8.5 EndY=-33.9 EndZ=0
    g18: LineSegment StartX=-5.5 StartY=-10.5 StartZ=0 EndX=-5.5 EndY=-27.7 EndZ=0
    g19: LineSegment StartX=-11.5 StartY=-4.3 StartZ=0 EndX=-11.5 EndY=-33.9 EndZ=0
    g20: LineSegment StartX=-14.6 StartY=-1.8 StartZ=0 EndX=-14.6 EndY=-36.4 EndZ=0
    g21: LineSegment StartX=-17.6 StartY=-1.8 StartZ=0 EndX=-17.6 EndY=-36.4 EndZ=0
    g22: LineSegment StartX=-20.6 StartY=-36.4 StartZ=0 EndX=-20.6 EndY=-1.8 EndZ=0
    g23: LineSegment StartX=-23.6 StartY=-1.8 StartZ=0 EndX=-23.6 EndY=-36.4 EndZ=0
  constraints (48):
    c: Block(g0)
    c: Block(g1)
    c: Block(g2)
    c: Block(g3)
    c: Block(g4)
    c: Block(g5)
    c: Block(g6)
    c: Block(g7)
    c: Block(g8)
    c: Block(g9)
    c: Block(g10)
    c: Block(g11)
    c: Coincident(g12,g1)
    c: Coincident(g12,g2)
    c: Vertical(g12)
    c: Coincident(g13,g1)
    c: Coincident(g13,g2)
    c: Vertical(g13)
    c: Coincident(g14,g11)
    c: Coincident(g14,g7)
    c: Vertical(g14)
    c: Coincident(g15,g11)
    c: Coincident(g15,g7)
    c: Vertical(g15)
    c: Coincident(g16,g0)
    c: Coincident(g16,g3)
    c: Vertical(g16)
    c: Coincident(g17,g4)
    c: Coincident(g17,g8)
    c: Vertical(g17)
    c: Coincident(g18,g0)
    c: Coincident(g18,g3)
    c: Vertical(g18)
    c: Coincident(g19,g4)
    c: Coincident(g19,g8)
    c: Vertical(g19)
    c: Coincident(g20,g5)
    c: Coincident(g20,g9)
    c: Vertical(g20)
    c: Coincident(g21,g5)
    c: Coincident(g21,g9)
    c: Vertical(g21)
    c: Coincident(g22,g10)
    c: Coincident(g22,g6)
    c: Vertical(g22)
    c: Coincident(g23,g6)
    c: Coincident(g23,g10)
    c: Vertical(g23)
FEATURE [Part::Extrusion] Extrude039  label="removeToCreateFanGrillHoles002"
  Base = -> Sketch048
  Dir = (0,-1,6e-16)
  DirMode = 2
  FaceMakerClass = Part::FaceMakerBullseye
  LengthFwd = 10
  LengthRev = 0
  Placement = pos=(65.4,44,54.82) rot=(0,0,1;0rad)
  Solid = true
  Symmetric = false
FEATURE [Part::Cut] Cut027  label="fanScrewHousing004"
  Base = -> Cut026
  Tool = -> Extrude038
FEATURE [Part::Cut] Cut028  label="top014"
  Base = -> Fillet026
  Tool = -> Extrude039
FEATURE [Part::Feature] Face095 .. Face098  x4 (patterned run collapsed; names and placements below)
  shape: bbox 3.5 x 17.8 x 2e-07 mm, 1 faces, 0 solids (baked)
FEATURE [Part::Revolution] Revolve103  label="removeToCreateScrewAndThreadedInsertHole030"
  Angle = 360
  Axis = (0,1,0)
  Base = (0,0,0)
  FaceMakerClass = Part::FaceMakerBullseye
  Placement = pos=(62.3,30.3,19.7) rot=(0,0,1;0rad)
  Solid = false
  Source = -> Face095
  Symmetric = false
FEATURE [Part::Revolution] Revolve104  label="removeToCreateScrewAndThreadedInsertHole031"
  Angle = 360
  Axis = (0,1,0)
  Base = (0,0,0)
  FaceMakerClass = Part::FaceMakerBullseye
  Placement = pos=(62.3,30.3,51.7) rot=(0,0,1;0rad)
  Solid = false
  Source = -> Face096
  Symmetric = false
FEATURE [Part::Revolution] Revolve105  label="removeToCreateScrewAndThreadedInsertHole032"
  Angle = 360
  Axis = (0,1,0)
  Base = (0,0,0)
  FaceMakerClass = Part::FaceMakerBullseye
  Placement = pos=(30.3,30.3,19.7) rot=(0,0,1;0rad)
  Solid = false
  Source = -> Face097
  Symmetric = false
FEATURE [Part::Revolution] Revolve106  label="removeToCreateScrewAndThreadedInsertHole033"
  Angle = 360
  Axis = (0,1,0)
  Base = (0,0,0)
  FaceMakerClass = Part::FaceMakerBullseye
  Placement = pos=(30.3,30.3,51.7) rot=(0,0,1;0rad)
  Solid = false
  Source = -> Face098
  Symmetric = false
FEATURE [Part::MultiFuse] Fusion069  label="createThreadedInsertHolesForFan003"
  Shapes = -> [Revolve103,Revolve104,Revolve105,Revolve106]
FEATURE [Part::Cut] Cut029  label="top015"
  Base = -> Cut028
  Tool = -> Fusion054
FEATURE [Part::Cut] Cut030  label="fanScrewHousing005"
  Base = -> Cut027
  Tool = -> Fusion069
FEATURE [Part::Cylinder] Cylinder026  label="removeToCreteHoleForPlugHousing010"
  Angle = 360
  AttacherType = Attacher::AttachEngine3D
  Height = 20
  Placement = pos=(-2,19,36) rot=(0,1,0;1.5708rad)
  Radius = 14.3
FEATURE [Part::Box] Box018  label="removeToCreteHoleForPlugHousing011"
  AttacherType = Attacher::AttachEngine3D
  Height = 28.6
  Length = 10
  Placement = pos=(-2,0,21.7) rot=(0,0,1;0rad)
  Width = 19
FEATURE [Part::Box] Box019  label="wireHolderBottomCaseBit"
  AttacherType = Attacher::AttachEngine3D
  Height = 28
  Length = 3
  Placement = pos=(0,0,22) rot=(0,0,1;0rad)
  Width = 21
FEATURE [Part::Cylinder] Cylinder027  label="removeToCreteHoleForPlugHousing012"
  Angle = 360
  AttacherType = Attacher::AttachEngine3D
  Height = 20
  Placement = pos=(-2,19,36) rot=(0,1,0;1.5708rad)
  Radius = 14.3
FEATURE [Part::Cut] Cut031  label="wireHolderBottomCaseBit001"
  Base = -> Box019
  Tool = -> Cylinder027
FEATURE [Part::MultiFuse] Fusion070  label="removeToCreteHoleForPlugHousing013"
  Shapes = -> [Box018,Cylinder026]
FEATURE [Part::Cut] Cut032  label="top016"
  Base = -> Cut029
  Tool = -> Fusion070
FEATURE [Part::Cylinder] Cylinder028
  Angle = 360
  AttacherType = Attacher::AttachEngine3D
  Height = 20
  Placement = pos=(0,0,36.15) rot=(0,0,1;0rad)
  Radius = 14.3
FEATURE [Part::Cylinder] Cylinder029
  Angle = 360
  AttacherType = Attacher::AttachEngine3D
  Height = 10
  Placement = pos=(0,0,36.15) rot=(0,0,1;0rad)
  Radius = 4
FEATURE [Part::MultiFuse] Fusion071  label="removeToCreteHoleForPlugHousing014"
  Placement = pos=(70,19,36) rot=(0,1,0;1.5708rad)
  Shapes = -> [Cylinder028,Cylinder029]
FEATURE [Sketcher::SketchObject] Sketch049  label="topSketch011"
  FullyConstrained = true
  sketch-geometry (4):
    g0: ArcOfCircle CenterX=105 CenterY=19 CenterZ=0 NormalX=0 NormalY=0 NormalZ=1 AngleXU=0 Radius=20.6155 StartAngle=5.54125 EndAngle=6.28319
    g1: ArcOfCircle CenterX=105 CenterY=19 CenterZ=0 NormalX=0 NormalY=0 NormalZ=1 AngleXU=0 Radius=13 StartAngle=5.54125 EndAngle=6.28319
    g2: LineSegment StartX=118 StartY=19 StartZ=0 EndX=125.616 EndY=19 EndZ=0
    g3: LineSegment StartX=114.583 StartY=10.2157 StartZ=0 EndX=120.197 EndY=5.06982 EndZ=0
  constraints (7):
    c: Block(g0)
    c: Block(g1)
    c: Coincident(g2,g1)
    c: Coincident(g2,g0)
    c: Horizontal(g2)
    c: Coincident(g3,g1)
    c: Coincident(g3,g0)
FEATURE [Part::Box] Box020  label="removeToCreteHoleForPlugHousing015"
  AttacherType = Attacher::AttachEngine3D
  Height = 28.6
  Length = 20
  Placement = pos=(106.15,0,21.7) rot=(0,0,1;0rad)
  Width = 19
FEATURE [Part::MultiFuse] Fusion072  label="removeToCreteHoleForPlugHousing016"
  Shapes = -> [Box020,Fusion071]
FEATURE [Part::Cut] Cut033  label="removeToCreteHoleForPlugHousing017"
  Base = -> Cut032
  Tool = -> Fusion072
FEATURE [Part::Cylinder] Cylinder030
  Angle = 360
  AttacherType = Attacher::AttachEngine3D
  Height = 20
  Placement = pos=(0,0,36.15) rot=(0,0,1;0rad)
  Radius = 14.3
FEATURE [Part::Cylinder] Cylinder031
  Angle = 360
  AttacherType = Attacher::AttachEngine3D
  Height = 10
  Placement = pos=(0,0,36.15) rot=(0,0,1;0rad)
  Radius = 4
FEATURE [Part::Box] Box021  label="removeToCreteHoleForPlugHousing019"
  AttacherType = Attacher::AttachEngine3D
  Height = 28.6
  Length = 20
  Placement = pos=(106.15,0,21.7) rot=(0,0,1;0rad)
  Width = 19
FEATURE [Part::MultiFuse] Fusion074  label="removeToCreteHoleForPlugHousing020"
  Placement = pos=(70,19,36) rot=(0,1,0;1.5708rad)
  Shapes = -> [Cylinder030,Cylinder031]
FEATURE [Part::MultiFuse] Fusion073  label="removeToCreteHoleForPlugHousing018"
  Placement = pos=(0,0,28.3) rot=(0,0,1;0rad)
  Shapes = -> [Box021,Fusion074]
FEATURE [Part::Cylinder] Cylinder032
  Angle = 360
  AttacherType = Attacher::AttachEngine3D
  Height = 20
  Placement = pos=(0,0,36.15) rot=(0,0,1;0rad)
  Radius = 14.3
FEATURE [Part::Cylinder] Cylinder033
  Angle = 360
  AttacherType = Attacher::AttachEngine3D
  Height = 10
  Placement = pos=(0,0,36.15) rot=(0,0,1;0rad)
  Radius = 4
FEATURE [Part::Box] Box022  label="removeToCreteHoleForPlugHousing021"
  AttacherType = Attacher::AttachEngine3D
  Height = 28.6
  Length = 20
  Placement = pos=(106.15,0,21.7) rot=(0,0,1;0rad)
  Width = 19
FEATURE [Part::MultiFuse] Fusion076  label="removeToCreteHoleForPlugHousing023"
  Placement = pos=(70,19,36) rot=(0,1,0;1.5708rad)
  Shapes = -> [Cylinder032,Cylinder033]
FEATURE [Part::MultiFuse] Fusion075  label="removeToCreteHoleForPlugHousing022"
  Placement = pos=(0,0,-28.3) rot=(0,0,1;0rad)
  Shapes = -> [Box022,Fusion076]
FEATURE [Part::MultiFuse] Fusion077  label="removeToCreatePlugHousingBottomBit"
  Shapes = -> [Fusion075,Fusion073]
FEATURE [Part::Cylinder] Cylinder034
  Angle = 360
  AttacherType = Attacher::AttachEngine3D
  Height = 20
  Placement = pos=(0,0,36.15) rot=(0,0,1;0rad)
  Radius = 14.3
FEATURE [Part::Cylinder] Cylinder035
  Angle = 360
  AttacherType = Attacher::AttachEngine3D
  Height = 10
  Placement = pos=(0,0,36.15) rot=(0,0,1;0rad)
  Radius = 4
FEATURE [Part::MultiFuse] Fusion078  label="removeToCreteHoleForPlugHousing024"
  Placement = pos=(70,19,36) rot=(0,1,0;1.5708rad)
  Shapes = -> [Cylinder034,Cylinder035]
FEATURE [Part::MultiFuse] Fusion079  label="removeToCreatePlugHousingBottomBit001"
  Shapes = -> [Fusion078,Fusion077]
FEATURE [Part::Extrusion] Extrude040  label="bottomPlugHousingBit"
  Base = -> Sketch049
  Dir = (0,0,1)
  DirMode = 2
  FaceMakerClass = Part::FaceMakerBullseye
  LengthFwd = 72
  LengthRev = 0
  Solid = true
  Symmetric = false
FEATURE [Part::Cut] Cut034  label="bottomPlugHousingBit001"
  Base = -> Extrude040
  Tool = -> Fusion079
FEATURE [Part::Box] Box023  label="Cube014"
  AttacherType = Attacher::AttachEngine3D
  Height = 16
  Length = 8
  Placement = pos=(12.7,31.52,28) rot=(0,0,1;0rad)
  Width = 4
FEATURE [Part::Cylinder] Cylinder036
  Angle = 360
  AttacherType = Attacher::AttachEngine3D
  Height = 10
  Placement = pos=(0,0,36.15) rot=(0,0,1;0rad)
  Radius = 4
FEATURE [Part::Cylinder] Cylinder037
  Angle = 360
  AttacherType = Attacher::AttachEngine3D
  Height = 20
  Placement = pos=(0,0,36.15) rot=(0,0,1;0rad)
  Radius = 8.2
FEATURE [Part::MultiFuse] Fusion080  label="removeToCreteHoleForPlugHousing025"
  Placement = pos=(-42,19,36) rot=(0,1,0;1.5708rad)
  Shapes = -> [Cylinder037,Cylinder036]
FEATURE [Sketcher::SketchObject] Sketch050  label="topSketch012"
  FullyConstrained = true
  sketch-geometry (4):
    g0: LineSegment StartX=16.8446 StartY=31.512 StartZ=0 EndX=16.3251 EndY=34.4666 EndZ=0
    g1: ArcOfCircle CenterX=19 CenterY=19.2524 CenterZ=0 NormalX=0 NormalY=0 NormalZ=1 AngleXU=0 Radius=15.4476 StartAngle=1.74483 EndAngle=2.72717
    g2: ArcOfCircle CenterX=19 CenterY=19.2524 CenterZ=0 NormalX=0 NormalY=0 NormalZ=1 AngleXU=0 Radius=12.4476 StartAngle=1.74483 EndAngle=2.73189
    g3: LineSegment StartX=4.86004 StartY=25.4725 StartZ=0 EndX=7.58253 EndY=24.2107 EndZ=0
  constraints (7):
    c: Block(g0)
    c: Coincident(g1,g0)
    c: Coincident(g2,g0)
    c: Coincident(g3,g1)
    c: Coincident(g3,g2)
    c: Block(g1)
    c: Block(g2)
FEATURE [Part::Extrusion] Extrude041
  Base = -> Sketch050
  Dir = (0,0,1)
  DirMode = 2
  FaceMakerClass = Part::FaceMakerBullseye
  LengthFwd = 10.6
  LengthRev = 0
  Placement = pos=(0,0,31) rot=(0,0,1;0rad)
  Solid = true
  Symmetric = false
FEATURE [Part::Cut] Cut035
  Base = -> Extrude041
  Placement = pos=(0,0,-0.3) rot=(0,0,1;0rad)
  Tool = -> Fusion080
FEATURE [Part::Cut] Cut036
  Base = -> Box023
  Tool = -> Cut035
FEATURE [Part::Fillet] Fillet027
  Base = -> Cut036
  Edges = 1 edges r=0.7: [Edge13]
FEATURE [Part::Fillet] Fillet028
  Base = -> Fillet027
  Edges = 1 edges r=0.7: [Edge13]
FEATURE [Part::Fillet] Fillet029
  Base = -> Fillet028
  Edges = 1 edges r=0.7: [Edge16]
FEATURE [Part::Fillet] Fillet030
  Base = -> Fillet029
  Edges = 1 edges r=0.7: [Edge11]
FEATURE [Part::Fillet] Fillet031
  Base = -> Fillet030
  Edges = 1 edges r=0.7: [Edge10]
FEATURE [Part::Fillet] Fillet032
  Base = -> Fillet031
  Edges = 1 edges r=1.2: [Edge5]
FEATURE [Part::Fillet] Fillet033
  Base = -> Fillet032
  Edges = 1 edges r=1.2: [Edge12]
FEATURE [Part::Fillet] Fillet034  label="wireHousingRetainer"
  Base = -> Fillet033
  Edges = 1 edges r=2: [Edge1]
  Placement = pos=(0.3,0,0) rot=(0,0,1;0rad)
FEATURE [Part::Feature] Face099
  shape: bbox 3.5 x 17.8 x 2e-07 mm, 1 faces, 0 solids (baked)
FEATURE [Part::Revolution] Revolve107  label="removeToCreateScrewAndThreadedInsertHole034"
  Angle = 360
  Axis = (0,1,0)
  Base = (0,0,0)
  FaceMakerClass = Part::FaceMakerBullseye
  Placement = pos=(12.5,0,10) rot=(0,0,1;0rad)
  Solid = false
  Source = -> Face099
  Symmetric = false
FEATURE [Part::Feature] Face100
  shape: bbox 3.5 x 17.8 x 2e-07 mm, 1 faces, 0 solids (baked)
FEATURE [Part::Revolution] Revolve108  label="removeToCreateScrewAndThreadedInsertHole035"
  Angle = 360
  Axis = (0,1,0)
  Base = (0,0,0)
  FaceMakerClass = Part::FaceMakerBullseye
  Placement = pos=(12.5,0,62) rot=(0,0,1;0rad)
  Solid = false
  Source = -> Face100
  Symmetric = false
FEATURE [Part::Feature] Face101
  shape: bbox 3.5 x 17.8 x 2e-07 mm, 1 faces, 0 solids (baked)
FEATURE [Part::Revolution] Revolve109  label="removeToCreateScrewAndThreadedInsertHole036"
  Angle = 360
  Axis = (0,1,0)
  Base = (0,0,0)
  FaceMakerClass = Part::FaceMakerBullseye
  Placement = pos=(89.5,0,68.5) rot=(0,0,1;0rad)
  Solid = false
  Source = -> Face101
  Symmetric = false
FEATURE [Part::Feature] Face102
  shape: bbox 3.5 x 17.8 x 2e-07 mm, 1 faces, 0 solids (baked)
FEATURE [Part::Revolution] Revolve110  label="removeToCreateScrewAndThreadedInsertHole037"
  Angle = 360
  Axis = (0,1,0)
  Base = (0,0,0)
  FaceMakerClass = Part::FaceMakerBullseye
  Placement = pos=(89.5,0,3.5) rot=(0,0,1;0rad)
  Solid = false
  Source = -> Face102
  Symmetric = false
FEATURE [Part::Feature] Face103
  shape: bbox 3.5 x 17.8 x 2e-07 mm, 1 faces, 0 solids (baked)
FEATURE [Part::Revolution] Revolve111  label="removeToCreateScrewAndThreadedInsertHole038"
  Angle = 360
  Axis = (0,1,0)
  Base = (0,0,0)
  FaceMakerClass = Part::FaceMakerBullseye
  Placement = pos=(109.5,4.7,3.5) rot=(0,0,1;0rad)
  Solid = false
  Source = -> Face103
  Symmetric = false
FEATURE [Part::Feature] Face104
  shape: bbox 3.5 x 17.8 x 2e-07 mm, 1 faces, 0 solids (baked)
FEATURE [Part::Revolution] Revolve112  label="removeToCreateScrewAndThreadedInsertHole039"
  Angle = 360
  Axis = (0,1,0)
  Base = (0,0,0)
  FaceMakerClass = Part::FaceMakerBullseye
  Placement = pos=(109.5,4.7,68.5) rot=(0,0,1;0rad)
  Solid = false
  Source = -> Face104
  Symmetric = false
FEATURE [Part::MultiFuse] Fusion081  label="removeToCreateScrewAndThreadedInsertHole040"
  Shapes = -> [Revolve107,Revolve108,Revolve109,Revolve110,Revolve111,Revolve112]
FEATURE [Part::MultiFuse] Fusion082  label="casePillars002"
  Shapes = -> [Revolve094,Revolve092,Revolve090,Revolve089,Revolve091,Revolve093]
FEATURE [Part::Cut] Cut037  label="casePillars003"
  Base = -> Fusion082
  Tool = -> Fusion081
FEATURE [Sketcher::SketchObject] Sketch051
  FullyConstrained = true
  Placement = pos=(117,19,0) rot=(0.57735,0.57735,0.57735;2.0944rad)
  sketch-geometry (48):
    g0: LineSegment StartX=-49.19 StartY=69.25 StartZ=0 EndX=-49.19 EndY=66.25 EndZ=0
    g1: LineSegment StartX=-49.19 StartY=63.5 StartZ=0 EndX=-49.19 EndY=60.5 EndZ=0
    g2: LineSegment StartX=-49.19 StartY=57.75 StartZ=0 EndX=-49.19 EndY=54.75 EndZ=0
    g3: LineSegment StartX=-49.19 StartY=52 StartZ=0 EndX=-49.19 EndY=49 EndZ=0
    g4: LineSegment StartX=-49.19 StartY=46.25 StartZ=0 EndX=-49.19 EndY=43.25 EndZ=0
    g5: LineSegment StartX=-49.19 StartY=40.5 StartZ=0 EndX=-49.19 EndY=37.5 EndZ=0
    g6: LineSegment StartX=-49.19 StartY=34.5 StartZ=0 EndX=-49.19 EndY=31.5 EndZ=0
    g7: LineSegment StartX=-49.19 StartY=28.75 StartZ=0 EndX=-49.19 EndY=25.75 EndZ=0
    g8: LineSegment StartX=-49.19 StartY=23 StartZ=0 EndX=-49.19 EndY=20 EndZ=0
    g9: LineSegment StartX=-49.19 StartY=17.25 StartZ=0 EndX=-49.19 EndY=14.25 EndZ=0
    g10: LineSegment StartX=-49.19 StartY=11.5 StartZ=0 EndX=-49.19 EndY=8.5 EndZ=0
    g11: LineSegment StartX=-49.19 StartY=5.75 StartZ=0 EndX=-49.19 EndY=2.75 EndZ=0
    g12: ArcOfCircle CenterX=-1.5 CenterY=67.75 CenterZ=0 NormalX=0 NormalY=0 NormalZ=1 AngleXU=0 Radius=1.5 StartAngle=4.71239 EndAngle=7.85398
    g13: ArcOfCircle CenterX=-1.5 CenterY=62 CenterZ=0 NormalX=0 NormalY=0 NormalZ=1 AngleXU=0 Radius=1.5 StartAngle=4.71239 EndAngle=7.85398
    g14: ArcOfCircle CenterX=-1.5 CenterY=56.25 CenterZ=0 NormalX=0 NormalY=0 NormalZ=1 AngleXU=0 Radius=1.5 StartAngle=4.71239 EndAngle=7.85398
    g15: ArcOfCircle CenterX=-11.49 CenterY=50.5 CenterZ=0 NormalX=0 NormalY=0 NormalZ=1 AngleXU=0 Radius=1.5 StartAngle=4.71239 EndAngle=7.85398
    g16: ArcOfCircle CenterX=-16.28 CenterY=44.75 CenterZ=0 NormalX=0 NormalY=0 NormalZ=1 AngleXU=0 Radius=1.5 StartAngle=4.71239 EndAngle=7.85398
    g17: ArcOfCircle CenterX=-18.2337 CenterY=39 CenterZ=0 NormalX=0 NormalY=0 NormalZ=1 AngleXU=0 Radius=1.5 StartAngle=4.71485 EndAngle=7.85398
    g18: ArcOfCircle CenterX=-16.2837 CenterY=27.25 CenterZ=0 NormalX=0 NormalY=0 NormalZ=1 AngleXU=0 Radius=1.5 StartAngle=4.71485 EndAngle=7.85398
    g19: ArcOfCircle CenterX=-18.2337 CenterY=33 CenterZ=0 NormalX=0 NormalY=0 NormalZ=1 AngleXU=0 Radius=1.5 StartAngle=4.71485 EndAngle=7.85398
    g20: ArcOfCircle CenterX=-11.49 CenterY=21.5 CenterZ=0 NormalX=0 NormalY=0 NormalZ=1 AngleXU=0 Radius=1.5 StartAngle=4.71239 EndAngle=7.85398
    g21: ArcOfCircle CenterX=-1.5 CenterY=4.25 CenterZ=0 NormalX=0 NormalY=0 NormalZ=1 AngleXU=0 Radius=1.5 StartAngle=4.71239 EndAngle=7.85398
    g22: ArcOfCircle CenterX=-1.5 CenterY=10 CenterZ=0 NormalX=0 NormalY=0 NormalZ=1 AngleXU=0 Radius=1.5 StartAngle=4.71239 EndAngle=7.85398
    g23: ArcOfCircle CenterX=-1.5 CenterY=15.75 CenterZ=0 NormalX=0 NormalY=0 NormalZ=1 AngleXU=0 Radius=1.5 StartAngle=4.71239 EndAngle=7.85398
    g24: LineSegment StartX=-49.19 StartY=69.25 StartZ=0 EndX=-1.5 EndY=69.25 EndZ=0
    g25: LineSegment StartX=-49.19 StartY=66.25 StartZ=0 EndX=-1.5 EndY=66.25 EndZ=0
    g26: LineSegment StartX=-49.19 StartY=63.5 StartZ=0 EndX=-1.5 EndY=63.5 EndZ=0
    g27: LineSegment StartX=-49.19 StartY=60.5 StartZ=0 EndX=-1.5 EndY=60.5 EndZ=0
    g28: LineSegment StartX=-49.19 StartY=57.75 StartZ=0 EndX=-1.5 EndY=57.75 EndZ=0
    g29: LineSegment StartX=-49.19 StartY=54.75 StartZ=0 EndX=-1.5 EndY=54.75 EndZ=0
    g30: LineSegment StartX=-49.19 StartY=52 StartZ=0 EndX=-11.49 EndY=52 EndZ=0
    g31: LineSegment StartX=-49.19 StartY=49 StartZ=0 EndX=-11.49 EndY=49 EndZ=0
    g32: LineSegment StartX=-49.19 StartY=46.25 StartZ=0 EndX=-16.28 EndY=46.25 EndZ=0
    g33: LineSegment StartX=-49.19 StartY=43.25 StartZ=0 EndX=-16.28 EndY=43.25 EndZ=0
    g34: LineSegment StartX=-49.19 StartY=40.5 StartZ=0 EndX=-18.2337 EndY=40.5 EndZ=0
    g35: LineSegment StartX=-49.19 StartY=37.5 StartZ=0 EndX=-18.23 EndY=37.5 EndZ=0
    g36: LineSegment StartX=-49.19 StartY=34.5 StartZ=0 EndX=-18.2337 EndY=34.5 EndZ=0
    g37: LineSegment StartX=-49.19 StartY=31.5 StartZ=0 EndX=-18.23 EndY=31.5 EndZ=0
    g38: LineSegment StartX=-49.19 StartY=28.75 StartZ=0 EndX=-16.2837 EndY=28.75 EndZ=0
    g39: LineSegment StartX=-49.19 StartY=25.75 StartZ=0 EndX=-16.28 EndY=25.75 EndZ=0
    g40: LineSegment StartX=-49.19 StartY=23 StartZ=0 EndX=-11.49 EndY=23 EndZ=0
    g41: LineSegment StartX=-49.19 StartY=20 StartZ=0 EndX=-11.49 EndY=20 EndZ=0
    g42: LineSegment StartX=-49.19 StartY=17.25 StartZ=0 EndX=-1.5 EndY=17.25 EndZ=0
    g43: LineSegment StartX=-49.19 StartY=14.25 StartZ=0 EndX=-1.5 EndY=14.25 EndZ=0
    g44: LineSegment StartX=-49.19 StartY=11.5 StartZ=0 EndX=-1.5 EndY=11.5 EndZ=0
    g45: LineSegment StartX=-49.19 StartY=8.5 StartZ=0 EndX=-1.5 EndY=8.5 EndZ=0
    g46: LineSegment StartX=-49.19 StartY=5.75 StartZ=0 EndX=-1.5 EndY=5.75 EndZ=0
    g47: LineSegment StartX=-49.19 StartY=2.75 StartZ=0 EndX=-1.5 EndY=2.75 EndZ=0
  constraints (120):
    c: Vertical(g0)
    c: Distance(g0) = 3
    c: Block(g0)
    c: Vertical(g1)
    c: Distance(g1) = 3
    c: Vertical(g2)
    c: Equal(g0,g2) = 3
    c: Block(g2)
    c: Vertical(g3)
    c: Equal(g1,g3) = 3
    c: Vertical(g4)
    c: Equal(g0,g4) = 3
    c: Block(g4)
    c: Vertical(g5)
    c: Equal(g1,g5) = 3
    c: Vertical(g6)
    c: Equal(g0,g6) = 3
    c: Block(g6)
    c: Vertical(g7)
    c: Equal(g1,g7) = 3
    c: Vertical(g8)
    c: Equal(g0,g8) = 3
    c: Block(g8)
    c: Vertical(g9)
    c: Equal(g1,g9) = 3
    c: Vertical(g10)
    c: Equal(g0,g10) = 3
    c: Block(g10)
    c: Vertical(g11)
    c: Equal(g1,g11) = 3
    c: Block(g12)
    c: Block(g13)
    c: Block(g14)
    c: Block(g15)
    c: Block(g16)
    c: Block(g17)
    c: Block(g18)
    c: Block(g19)
    c: Block(g20)
    c: Block(g21)
    c: Block(g22)
    c: Block(g23)
    c: Block(g11)
    c: Block(g9)
    c: Block(g7)
    c: Block(g5)
    c: Block(g3)
    c: Block(g1)
    c: Coincident(g24,g0)
    c: Coincident(g24,g12)
    c: Horizontal(g24)
    c: Coincident(g25,g0)
    c: Coincident(g25,g12)
    c: Horizontal(g25)
    c: Coincident(g26,g1)
    c: Coincident(g26,g13)
    c: Horizontal(g26)
    c: Coincident(g27,g1)
    c: Coincident(g27,g13)
    c: Horizontal(g27)
    c: Coincident(g28,g2)
    c: Coincident(g28,g14)
    c: Horizontal(g28)
    c: Coincident(g29,g2)
    c: Coincident(g29,g14)
    c: Horizontal(g29)
    c: Coincident(g30,g3)
    c: Coincident(g30,g15)
    c: Horizontal(g30)
    c: Coincident(g31,g3)
    c: Coincident(g31,g15)
    c: Horizontal(g31)
    c: Coincident(g32,g4)
    c: Coincident(g32,g16)
    c: Horizontal(g32)
    c: Coincident(g33,g4)
    c: Coincident(g33,g16)
    c: Horizontal(g33)
    c: Coincident(g34,g5)
    c: Coincident(g34,g17)
    c: Horizontal(g34)
    c: Coincident(g35,g5)
    c: Coincident(g35,g17)
    c: Horizontal(g35)
    c: Coincident(g36,g6)
    c: Coincident(g36,g19)
    c: Horizontal(g36)
    c: Coincident(g37,g6)
    c: Coincident(g37,g19)
    c: Horizontal(g37)
    c: Coincident(g38,g7)
    c: Coincident(g38,g18)
    c: Horizontal(g38)
    c: Coincident(g39,g7)
    c: Coincident(g39,g18)
    c: Horizontal(g39)
    c: Coincident(g40,g8)
    c: Coincident(g40,g20)
    c: Horizontal(g40)
    c: Coincident(g41,g8)
    c: Coincident(g41,g20)
    c: Horizontal(g41)
    c: Coincident(g42,g9)
    c: Coincident(g42,g23)
    c: Horizontal(g42)
    c: Coincident(g43,g9)
    c: Coincident(g43,g23)
    c: Horizontal(g43)
    c: Coincident(g44,g10)
    c: Coincident(g44,g22)
    c: Horizontal(g44)
    c: Coincident(g45,g10)
    c: Coincident(g45,g22)
    c: Horizontal(g45)
    c: Coincident(g46,g11)
    c: Coincident(g46,g21)
    c: Horizontal(g46)
    c: Coincident(g47,g11)
    c: Coincident(g47,g21)
    c: Horizontal(g47)
FEATURE [Part::Extrusion] Extrude042
  Base = -> Sketch051
  Dir = (1,-2e-16,2e-16)
  DirMode = 2
  FaceMakerClass = Part::FaceMakerBullseye
  LengthFwd = 19
  LengthRev = 0
  Placement = pos=(-19,0,0) rot=(0,0,1;0rad)
  Solid = true
  Symmetric = false
FEATURE [Part::Fillet] Fillet035  label="removeToCreateVentalationHoles"
  Base = -> Extrude042
  Edges = <same value as first occurrence — deduplicated (x4 in doc)>
  Placement = pos=(7,0,0) rot=(0,0,1;0rad)
FEATURE [Part::Cut] Cut038  label="top017"
  Base = -> Cut033
  Tool = -> Fillet035
FEATURE [Sketcher::SketchObject] Sketch052  label="bottomSketch001"
  FullyConstrained = true
  sketch-geometry (26):
    g0: LineSegment StartX=6.29999 StartY=8 StartZ=0 EndX=3.29999 EndY=8 EndZ=0
    g1: LineSegment StartX=3.29999 StartY=8 StartZ=0 EndX=3.29999 EndY=-6.03275e-07 EndZ=0
    g2: ArcOfCircle CenterX=8.29999 CenterY=5 CenterZ=0 NormalX=0 NormalY=0 NormalZ=1 AngleXU=0 Radius=2 StartAngle=3.14159 EndAngle=4.71239
    g3: LineSegment StartX=6.29999 StartY=8 StartZ=0 EndX=6.29999 EndY=5 EndZ=0
    g4: ArcOfCircle CenterX=105 CenterY=19 CenterZ=0 NormalX=0 NormalY=0 NormalZ=1 AngleXU=0 Radius=12.7 StartAngle=4.71239 EndAngle=6.28319
    g5-g11: Circle x7 (B-spline internal-alignment scaffolding for g12; pole/knot coordinates omitted)
    g12: BSplineCurve PolesCount=7 KnotsCount=5 Degree=3 IsPeriodic=0
    g13-g17: GeomPoint x5 (B-spline internal-alignment scaffolding for g12; pole/knot coordinates omitted)
    g18: ArcOfCircle CenterX=105 CenterY=19 CenterZ=0 NormalX=0 NormalY=0 NormalZ=1 AngleXU=0 Radius=15.7 StartAngle=5.81226 EndAngle=6.28319
    g19: LineSegment StartX=117.7 StartY=19 StartZ=0 EndX=120.7 EndY=19 EndZ=0
    g20: BSplineCurve PolesCount=5 KnotsCount=3 Degree=3 IsPeriodic=0
    g21: LineSegment StartX=8.29999 StartY=3 StartZ=0 EndX=101.7 EndY=3 EndZ=0
    g22: LineSegment StartX=3.29999 StartY=-6.03275e-07 StartZ=0 EndX=105 EndY=-6.03275e-07 EndZ=0
    g23: LineSegment StartX=120.974 StartY=8.71251 StartZ=0 EndX=122.332 EndY=7.83778 EndZ=0
    g24: LineSegment StartX=105 StartY=-6.03274e-07 StartZ=0 EndX=113 EndY=-6.03274e-07 EndZ=0
    g25: ArcOfCircle CenterX=105 CenterY=19 CenterZ=0 NormalX=0 NormalY=0 NormalZ=1 AngleXU=0 Radius=20.6155 StartAngle=5.11091 EndAngle=5.71103
  constraints (38):
    c: Horizontal(g0)
    c: Distance(g0) = 3
    c: Coincident(g1,g0)
    c: Vertical(g1)
    c: Block(g2)
    c: Block(g0)
    c: Coincident(g3,g0)
    c: Coincident(g3,g2)
    c: Vertical(g3)
    c: Block(g1)
    c: Block(g4)
    c: Coincident(g20,g4)
    c: Block(g20)
    c: Equal(g5, g6-g11) x6
    c: InternalAlignment(g5-g11 -> g12) x7
    c: InternalAlignment(g13-g17 -> g12) x5
    c: Block(g12)
    c: Coincident(g18,g12)
    c: Coincident(g19,g4)
    c: Coincident(g19,g18)
    c: Horizontal(g19)
    c: Block(g19)
    c: Block(g18)
    c: Coincident(g21,g2)
    c: Coincident(g21,g20)
    c: Horizontal(g21)
    c: Distance(g21) = 93.4
    c: Coincident(g22,g1)
    c: Horizontal(g22)
    c: Distance(g22) = 101.7
    c: Horizontal(g24)
    c: Distance(g24) = 8
    c: Coincident(g25,g24)
    c: Block(g24)
    c: Coincident(g23,g25)
    c: Block(g25)
    c: Block(g23)
    c: Distance(g23) = 1.61553
FEATURE [Part::Extrusion] Extrude043  label="bottom010"
  Base = -> Sketch052
  Dir = (0,0,1)
  DirMode = 2
  FaceMakerClass = Part::FaceMakerBullseye
  LengthFwd = 71.4
  LengthRev = 0
  Placement = pos=(0,0,0.3) rot=(0,0,1;0rad)
  Solid = true
  Symmetric = false
FEATURE [Sketcher::SketchObject] Sketch053  label="topSketch013"
  FullyConstrained = true
  sketch-geometry (22):
    g0: LineSegment StartX=5.21097e-06 StartY=3 StartZ=0 EndX=5.21097e-06 EndY=19 EndZ=0
    g1: ArcOfCircle CenterX=19 CenterY=19 CenterZ=0 NormalX=0 NormalY=0 NormalZ=1 AngleXU=0 Radius=19 StartAngle=1.5708 EndAngle=3.14159
    g2: ArcOfCircle CenterX=19 CenterY=19 CenterZ=0 NormalX=0 NormalY=0 NormalZ=1 AngleXU=0 Radius=16 StartAngle=1.5708 EndAngle=3.14159
    g3: LineSegment StartX=114 StartY=35 StartZ=0 EndX=19 EndY=35 EndZ=0
    g4: LineSegment StartX=5.21097e-06 StartY=3 StartZ=0 EndX=5.21097e-06 EndY=0 EndZ=0
    g5: LineSegment StartX=3 StartY=0 StartZ=0 EndX=5.21097e-06 EndY=0 EndZ=0
    g6: LineSegment StartX=3 StartY=19 StartZ=0 EndX=3 EndY=0 EndZ=0
    g7: LineSegment StartX=19 StartY=38 StartZ=0 EndX=124 EndY=38 EndZ=0
    g8: Circle CenterX=119 CenterY=35 CenterZ=0 NormalX=0 NormalY=0 NormalZ=1 AngleXU=0 Radius=1
    g9: Circle CenterX=121 CenterY=35 CenterZ=0 NormalX=0 NormalY=0 NormalZ=1 AngleXU=0 Radius=1
    g10: Circle CenterX=121 CenterY=33 CenterZ=0 NormalX=0 NormalY=0 NormalZ=1 AngleXU=0 Radius=1
    g11: BSplineCurve PolesCount=3 KnotsCount=2 Degree=2 IsPeriodic=0
    g12: GeomPoint X=119 Y=35 Z=0
    g13: GeomPoint X=121 Y=33 Z=0
    g14: LineSegment StartX=119 StartY=35 StartZ=0 EndX=114 EndY=35 EndZ=0
    g15: ArcOfCircle CenterX=105 CenterY=19 CenterZ=0 NormalX=0 NormalY=0 NormalZ=1 AngleXU=0 Radius=16 StartAngle=5.60905 EndAngle=6.28319
    g16: LineSegment StartX=121 StartY=33 StartZ=0 EndX=121 EndY=19 EndZ=0
    g17: LineSegment StartX=117.5 StartY=9.01251 StartZ=0 EndX=121.163 EndY=9.0125 EndZ=0
    g18: ArcOfCircle CenterX=105 CenterY=19 CenterZ=0 NormalX=0 NormalY=0 NormalZ=1 AngleXU=0 Radius=20.6155 StartAngle=5.7297 EndAngle=6.28319
    g19: LineSegment StartX=121.163 StartY=9.0125 StartZ=0 EndX=122.538 EndY=8.16329 EndZ=0
    g20: LineSegment StartX=124 StartY=38 StartZ=0 EndX=125.616 EndY=38 EndZ=0
    g21: LineSegment StartX=125.616 StartY=19 StartZ=0 EndX=125.616 EndY=38 EndZ=0
  constraints (50):
    c: Vertical(g0)
    c: Block(g0)
    c: Coincident(g1,g0)
    c: Block(g1)
    c: Coincident(g2,g1)
    c: Block(g2)
    c: Coincident(g3,g2)
    c: Horizontal(g3)
    c: Tangent(g3,g2)
    c: Coincident(g4,g0)
    c: Distance(g4) = 3
    c: Vertical(g4)
    c: Coincident(g5,g4)
    c: Horizontal(g5)
    c: Coincident(g6,g2)
    c: Coincident(g6,g5)
    c: Vertical(g6)
    c: Horizontal(g7)
    c: Distance(g7) = 105
    c: Coincident(g7,g1)
    c: Block(g3)
    c: Weight(g8) = 1
    c: Equal(g8,g9)
    c: Equal(g8,g10)
    c: InternalAlignment(g8,g11)
    c: InternalAlignment(g9,g11)
    c: InternalAlignment(g10,g11)
    c: InternalAlignment(g12,g11)
    c: InternalAlignment(g13,g11)
    c: Block(g11)
    c: Coincident(g14,g11)
    c: Coincident(g14,g3)
    c: Horizontal(g14)
    c: Block(g15)
    c: Coincident(g16,g11)
    c: Coincident(g16,g15)
    c: Vertical(g16)
    c: Distance(g16) = 14
    c: Coincident(g17,g15)
    c: Block(g18)
    c: Coincident(g19,g18)
    c: Coincident(g20,g7)
    c: Horizontal(g20)
    c: Vertical(g21)
    c: Coincident(g20,g21)
    c: Block(g20)
    c: Block(g21)
    c: Block(g19)
    c: Block(g17)
    c: Distance(g20) = 1.61553
FEATURE [Part::Extrusion] Extrude044
  Base = -> Sketch053
  Dir = (0,0,1)
  DirMode = 2
  FaceMakerClass = Part::FaceMakerBullseye
  LengthFwd = 72
  LengthRev = 0
  Solid = true
  Symmetric = false
FEATURE [Part::Fillet] Fillet036  label="top018"
  Base = -> Extrude044
  Edges = 1 edges r=2: [Edge41]
FEATURE [Part::Fillet] Fillet037  label="bottom011"
  Base = -> Extrude043
  Edges = 1 edges r=2.4: [Edge26]
FEATURE [Sketcher::SketchObject] Sketch054
  FullyConstrained = false
  Placement = pos=(0,0,0) rot=(1,0,0;1.5708rad)
  sketch-geometry (24):
    g0: ArcOfCircle CenterX=-4 CenterY=-10.5 CenterZ=0 NormalX=0 NormalY=0 NormalZ=1 AngleXU=0 Radius=1.5 StartAngle=6e-16 EndAngle=3.14159
    g1: ArcOfCircle CenterX=-34.2 CenterY=-10.5 CenterZ=0 NormalX=0 NormalY=0 NormalZ=1 AngleXU=0 Radius=1.5 StartAngle=0 EndAngle=3.14159
    g2: ArcOfCircle CenterX=-34.2 CenterY=-27.7 CenterZ=0 NormalX=0 NormalY=0 NormalZ=1 AngleXU=0 Radius=1.5 StartAngle=3.14159 EndAngle=6.28319
    g3: ArcOfCircle CenterX=-4 CenterY=-27.7 CenterZ=0 NormalX=0 NormalY=0 NormalZ=1 AngleXU=0 Radius=1.5 StartAngle=3.1416 EndAngle=6.28319
    g4: ArcOfCircle CenterX=-10 CenterY=-4.3 CenterZ=0 NormalX=0 NormalY=0 NormalZ=1 AngleXU=0 Radius=1.5 StartAngle=2e-16 EndAngle=3.14159
    g5: ArcOfCircle CenterX=-16.1 CenterY=-1.8 CenterZ=0 NormalX=0 NormalY=0 NormalZ=1 AngleXU=0 Radius=1.5 StartAngle=5e-16 EndAngle=3.14159
    g6: ArcOfCircle CenterX=-22.1 CenterY=-1.8 CenterZ=0 NormalX=0 NormalY=0 NormalZ=1 AngleXU=0 Radius=1.5 StartAngle=5e-16 EndAngle=3.14159
    g7: ArcOfCircle CenterX=-28.2 CenterY=-4.3 CenterZ=0 NormalX=0 NormalY=0 NormalZ=1 AngleXU=0 Radius=1.5 StartAngle=2e-16 EndAngle=3.14159
    g8: ArcOfCircle CenterX=-10 CenterY=-33.9 CenterZ=0 NormalX=0 NormalY=0 NormalZ=1 AngleXU=0 Radius=1.5 StartAngle=3.14159 EndAngle=6.28319
    g9: ArcOfCircle CenterX=-16.1 CenterY=-36.4 CenterZ=0 NormalX=0 NormalY=0 NormalZ=1 AngleXU=0 Radius=1.5 StartAngle=3.14159 EndAngle=6.28319
    g10: ArcOfCircle CenterX=-22.1 CenterY=-36.4 CenterZ=0 NormalX=0 NormalY=0 NormalZ=1 AngleXU=0 Radius=1.5 StartAngle=3.14159 EndAngle=6.28319
    g11: ArcOfCircle CenterX=-28.2 CenterY=-33.9 CenterZ=0 NormalX=0 NormalY=0 NormalZ=1 AngleXU=0 Radius=1.5 StartAngle=3.14159 EndAngle=6.28319
    g12: LineSegment StartX=-35.7 StartY=-10.5 StartZ=0 EndX=-35.7 EndY=-27.7 EndZ=0
    g13: LineSegment StartX=-32.7 StartY=-10.5 StartZ=0 EndX=-32.7 EndY=-27.7 EndZ=0
    g14: LineSegment StartX=-29.7 StartY=-33.9 StartZ=0 EndX=-29.7 EndY=-4.3 EndZ=0
    g15: LineSegment StartX=-26.7 StartY=-33.9 StartZ=0 EndX=-26.7 EndY=-4.3 EndZ=0
    g16: LineSegment StartX=-2.5 StartY=-10.5 StartZ=0 EndX=-2.5 EndY=-27.7 EndZ=0
    g17: LineSegment StartX=-8.5 StartY=-4.3 StartZ=0 EndX=-8.5 EndY=-33.9 EndZ=0
    g18: LineSegment StartX=-5.5 StartY=-10.5 StartZ=0 EndX=-5.5 EndY=-27.7 EndZ=0
    g19: LineSegment StartX=-11.5 StartY=-4.3 StartZ=0 EndX=-11.5 EndY=-33.9 EndZ=0
    g20: LineSegment StartX=-14.6 StartY=-1.8 StartZ=0 EndX=-14.6 EndY=-36.4 EndZ=0
    g21: LineSegment StartX=-17.6 StartY=-1.8 StartZ=0 EndX=-17.6 EndY=-36.4 EndZ=0
    g22: LineSegment StartX=-20.6 StartY=-36.4 StartZ=0 EndX=-20.6 EndY=-1.8 EndZ=0
    g23: LineSegment StartX=-23.6 StartY=-1.8 StartZ=0 EndX=-23.6 EndY=-36.4 EndZ=0
  constraints (48):
    c: Block(g0)
    c: Block(g1)
    c: Block(g2)
    c: Block(g3)
    c: Block(g4)
    c: Block(g5)
    c: Block(g6)
    c: Block(g7)
    c: Block(g8)
    c: Block(g9)
    c: Block(g10)
    c: Block(g11)
    c: Coincident(g12,g1)
    c: Coincident(g12,g2)
    c: Vertical(g12)
    c: Coincident(g13,g1)
    c: Coincident(g13,g2)
    c: Vertical(g13)
    c: Coincident(g14,g11)
    c: Coincident(g14,g7)
    c: Vertical(g14)
    c: Coincident(g15,g11)
    c: Coincident(g15,g7)
    c: Vertical(g15)
    c: Coincident(g16,g0)
    c: Coincident(g16,g3)
    c: Vertical(g16)
    c: Coincident(g17,g4)
    c: Coincident(g17,g8)
    c: Vertical(g17)
    c: Coincident(g18,g0)
    c: Coincident(g18,g3)
    c: Vertical(g18)
    c: Coincident(g19,g4)
    c: Coincident(g19,g8)
    c: Vertical(g19)
    c: Coincident(g20,g5)
    c: Coincident(g20,g9)
    c: Vertical(g20)
    c: Coincident(g21,g5)
    c: Coincident(g21,g9)
    c: Vertical(g21)
    c: Coincident(g22,g10)
    c: Coincident(g22,g6)
    c: Vertical(g22)
    c: Coincident(g23,g6)
    c: Coincident(g23,g10)
    c: Vertical(g23)
FEATURE [Part::Extrusion] Extrude045  label="removeToCreateFanGrillHoles003"
  Base = -> Sketch054
  Dir = (0,-1,6e-16)
  DirMode = 2
  FaceMakerClass = Part::FaceMakerBullseye
  LengthFwd = 10
  LengthRev = 0
  Placement = pos=(65.4,44,54.82) rot=(0,0,1;0rad)
  Solid = true
  Symmetric = false
FEATURE [Part::Feature] Face105 .. Face108  x4 (patterned run collapsed; names and placements below)
  shape: bbox 3.5 x 17.8 x 2e-07 mm, 1 faces, 0 solids (baked)
FEATURE [Part::Revolution] Revolve113  label="removeToCreateScrewAndThreadedInsertHole041"
  Angle = 360
  Axis = (0,1,0)
  Base = (0,0,0)
  FaceMakerClass = Part::FaceMakerBullseye
  Placement = pos=(62.3,30.3,19.7) rot=(0,0,1;0rad)
  Solid = false
  Source = -> Face105
  Symmetric = false
FEATURE [Part::Revolution] Revolve114  label="removeToCreateScrewAndThreadedInsertHole042"
  Angle = 360
  Axis = (0,1,0)
  Base = (0,0,0)
  FaceMakerClass = Part::FaceMakerBullseye
  Placement = pos=(62.3,30.3,51.7) rot=(0,0,1;0rad)
  Solid = false
  Source = -> Face106
  Symmetric = false
FEATURE [Part::Revolution] Revolve115  label="removeToCreateScrewAndThreadedInsertHole043"
  Angle = 360
  Axis = (0,1,0)
  Base = (0,0,0)
  FaceMakerClass = Part::FaceMakerBullseye
  Placement = pos=(30.3,30.3,19.7) rot=(0,0,1;0rad)
  Solid = false
  Source = -> Face107
  Symmetric = false
FEATURE [Part::Revolution] Revolve116  label="removeToCreateScrewAndThreadedInsertHole044"
  Angle = 360
  Axis = (0,1,0)
  Base = (0,0,0)
  FaceMakerClass = Part::FaceMakerBullseye
  Placement = pos=(30.3,30.3,51.7) rot=(0,0,1;0rad)
  Solid = false
  Source = -> Face108
  Symmetric = false
FEATURE [Part::MultiFuse] Fusion083  label="createThreadedInsertHolesForFan004"
  Shapes = -> [Revolve113,Revolve114,Revolve115,Revolve116]
FEATURE [Part::Box] Box024  label="removeToCreteHoleForPlugHousing026"
  AttacherType = Attacher::AttachEngine3D
  Height = 28.6
  Length = 10
  Placement = pos=(-2,0,21.7) rot=(0,0,1;0rad)
  Width = 19
FEATURE [Part::Cylinder] Cylinder038  label="removeToCreteHoleForPlugHousing027"
  Angle = 360
  AttacherType = Attacher::AttachEngine3D
  Height = 20
  Placement = pos=(-2,19,36) rot=(0,1,0;1.5708rad)
  Radius = 14.3
FEATURE [Part::MultiFuse] Fusion084  label="removeToCreteHoleForPlugHousing028"
  Shapes = -> [Box024,Cylinder038]
FEATURE [Part::Cylinder] Cylinder039
  Angle = 360
  AttacherType = Attacher::AttachEngine3D
  Height = 20
  Placement = pos=(0,0,36.15) rot=(0,0,1;0rad)
  Radius = 14.3
FEATURE [Part::Cylinder] Cylinder040
  Angle = 360
  AttacherType = Attacher::AttachEngine3D
  Height = 10
  Placement = pos=(0,0,36.15) rot=(0,0,1;0rad)
  Radius = 4
FEATURE [Part::Box] Box025  label="removeToCreteHoleForPlugHousing030"
  AttacherType = Attacher::AttachEngine3D
  Height = 28.6
  Length = 20
  Placement = pos=(106.15,0,21.7) rot=(0,0,1;0rad)
  Width = 19
FEATURE [Part::MultiFuse] Fusion086  label="removeToCreteHoleForPlugHousing031"
  Placement = pos=(70,19,36) rot=(0,1,0;1.5708rad)
  Shapes = -> [Cylinder039,Cylinder040]
FEATURE [Part::MultiFuse] Fusion085  label="removeToCreteHoleForPlugHousing029"
  Shapes = -> [Box025,Fusion086]
FEATURE [Sketcher::SketchObject] Sketch055
  FullyConstrained = true
  Placement = pos=(117,19,0) rot=(0.57735,0.57735,0.57735;2.0944rad)
  sketch-geometry (48):
    g0: LineSegment StartX=-49.19 StartY=69.25 StartZ=0 EndX=-49.19 EndY=66.25 EndZ=0
    g1: LineSegment StartX=-49.19 StartY=63.5 StartZ=0 EndX=-49.19 EndY=60.5 EndZ=0
    g2: LineSegment StartX=-49.19 StartY=57.75 StartZ=0 EndX=-49.19 EndY=54.75 EndZ=0
    g3: LineSegment StartX=-49.19 StartY=52 StartZ=0 EndX=-49.19 EndY=49 EndZ=0
    g4: LineSegment StartX=-49.19 StartY=46.25 StartZ=0 EndX=-49.19 EndY=43.25 EndZ=0
    g5: LineSegment StartX=-49.19 StartY=40.5 StartZ=0 EndX=-49.19 EndY=37.5 EndZ=0
    g6: LineSegment StartX=-49.19 StartY=34.5 StartZ=0 EndX=-49.19 EndY=31.5 EndZ=0
    g7: LineSegment StartX=-49.19 StartY=28.75 StartZ=0 EndX=-49.19 EndY=25.75 EndZ=0
    g8: LineSegment StartX=-49.19 StartY=23 StartZ=0 EndX=-49.19 EndY=20 EndZ=0
    g9: LineSegment StartX=-49.19 StartY=17.25 StartZ=0 EndX=-49.19 EndY=14.25 EndZ=0
    g10: LineSegment StartX=-49.19 StartY=11.5 StartZ=0 EndX=-49.19 EndY=8.5 EndZ=0
    g11: LineSegment StartX=-49.19 StartY=5.75 StartZ=0 EndX=-49.19 EndY=2.75 EndZ=0
    g12: ArcOfCircle CenterX=-1.5 CenterY=67.75 CenterZ=0 NormalX=0 NormalY=0 NormalZ=1 AngleXU=0 Radius=1.5 StartAngle=4.71239 EndAngle=7.85398
    g13: ArcOfCircle CenterX=-1.5 CenterY=62 CenterZ=0 NormalX=0 NormalY=0 NormalZ=1 AngleXU=0 Radius=1.5 StartAngle=4.71239 EndAngle=7.85398
    g14: ArcOfCircle CenterX=-1.5 CenterY=56.25 CenterZ=0 NormalX=0 NormalY=0 NormalZ=1 AngleXU=0 Radius=1.5 StartAngle=4.71239 EndAngle=7.85398
    g15: ArcOfCircle CenterX=-11.49 CenterY=50.5 CenterZ=0 NormalX=0 NormalY=0 NormalZ=1 AngleXU=0 Radius=1.5 StartAngle=4.71239 EndAngle=7.85398
    g16: ArcOfCircle CenterX=-16.28 CenterY=44.75 CenterZ=0 NormalX=0 NormalY=0 NormalZ=1 AngleXU=0 Radius=1.5 StartAngle=4.71239 EndAngle=7.85398
    g17: ArcOfCircle CenterX=-18.2337 CenterY=39 CenterZ=0 NormalX=0 NormalY=0 NormalZ=1 AngleXU=0 Radius=1.5 StartAngle=4.71485 EndAngle=7.85398
    g18: ArcOfCircle CenterX=-16.2837 CenterY=27.25 CenterZ=0 NormalX=0 NormalY=0 NormalZ=1 AngleXU=0 Radius=1.5 StartAngle=4.71485 EndAngle=7.85398
    g19: ArcOfCircle CenterX=-18.2337 CenterY=33 CenterZ=0 NormalX=0 NormalY=0 NormalZ=1 AngleXU=0 Radius=1.5 StartAngle=4.71485 EndAngle=7.85398
    g20: ArcOfCircle CenterX=-11.49 CenterY=21.5 CenterZ=0 NormalX=0 NormalY=0 NormalZ=1 AngleXU=0 Radius=1.5 StartAngle=4.71239 EndAngle=7.85398
    g21: ArcOfCircle CenterX=-1.5 CenterY=4.25 CenterZ=0 NormalX=0 NormalY=0 NormalZ=1 AngleXU=0 Radius=1.5 StartAngle=4.71239 EndAngle=7.85398
    g22: ArcOfCircle CenterX=-1.5 CenterY=10 CenterZ=0 NormalX=0 NormalY=0 NormalZ=1 AngleXU=0 Radius=1.5 StartAngle=4.71239 EndAngle=7.85398
    g23: ArcOfCircle CenterX=-1.5 CenterY=15.75 CenterZ=0 NormalX=0 NormalY=0 NormalZ=1 AngleXU=0 Radius=1.5 StartAngle=4.71239 EndAngle=7.85398
    g24: LineSegment StartX=-49.19 StartY=69.25 StartZ=0 EndX=-1.5 EndY=69.25 EndZ=0
    g25: LineSegment StartX=-49.19 StartY=66.25 StartZ=0 EndX=-1.5 EndY=66.25 EndZ=0
    g26: LineSegment StartX=-49.19 StartY=63.5 StartZ=0 EndX=-1.5 EndY=63.5 EndZ=0
    g27: LineSegment StartX=-49.19 StartY=60.5 StartZ=0 EndX=-1.5 EndY=60.5 EndZ=0
    g28: LineSegment StartX=-49.19 StartY=57.75 StartZ=0 EndX=-1.5 EndY=57.75 EndZ=0
    g29: LineSegment StartX=-49.19 StartY=54.75 StartZ=0 EndX=-1.5 EndY=54.75 EndZ=0
    g30: LineSegment StartX=-49.19 StartY=52 StartZ=0 EndX=-11.49 EndY=52 EndZ=0
    g31: LineSegment StartX=-49.19 StartY=49 StartZ=0 EndX=-11.49 EndY=49 EndZ=0
    g32: LineSegment StartX=-49.19 StartY=46.25 StartZ=0 EndX=-16.28 EndY=46.25 EndZ=0
    g33: LineSegment StartX=-49.19 StartY=43.25 StartZ=0 EndX=-16.28 EndY=43.25 EndZ=0
    g34: LineSegment StartX=-49.19 StartY=40.5 StartZ=0 EndX=-18.2337 EndY=40.5 EndZ=0
    g35: LineSegment StartX=-49.19 StartY=37.5 StartZ=0 EndX=-18.23 EndY=37.5 EndZ=0
    g36: LineSegment StartX=-49.19 StartY=34.5 StartZ=0 EndX=-18.2337 EndY=34.5 EndZ=0
    g37: LineSegment StartX=-49.19 StartY=31.5 StartZ=0 EndX=-18.23 EndY=31.5 EndZ=0
    g38: LineSegment StartX=-49.19 StartY=28.75 StartZ=0 EndX=-16.2837 EndY=28.75 EndZ=0
    g39: LineSegment StartX=-49.19 StartY=25.75 StartZ=0 EndX=-16.28 EndY=25.75 EndZ=0
    g40: LineSegment StartX=-49.19 StartY=23 StartZ=0 EndX=-11.49 EndY=23 EndZ=0
    g41: LineSegment StartX=-49.19 StartY=20 StartZ=0 EndX=-11.49 EndY=20 EndZ=0
    g42: LineSegment StartX=-49.19 StartY=17.25 StartZ=0 EndX=-1.5 EndY=17.25 EndZ=0
    g43: LineSegment StartX=-49.19 StartY=14.25 StartZ=0 EndX=-1.5 EndY=14.25 EndZ=0
    g44: LineSegment StartX=-49.19 StartY=11.5 StartZ=0 EndX=-1.5 EndY=11.5 EndZ=0
    g45: LineSegment StartX=-49.19 StartY=8.5 StartZ=0 EndX=-1.5 EndY=8.5 EndZ=0
    g46: LineSegment StartX=-49.19 StartY=5.75 StartZ=0 EndX=-1.5 EndY=5.75 EndZ=0
    g47: LineSegment StartX=-49.19 StartY=2.75 StartZ=0 EndX=-1.5 EndY=2.75 EndZ=0
  constraints (120):
    c: Vertical(g0)
    c: Distance(g0) = 3
    c: Block(g0)
    c: Vertical(g1)
    c: Distance(g1) = 3
    c: Vertical(g2)
    c: Equal(g0,g2) = 3
    c: Block(g2)
    c: Vertical(g3)
    c: Equal(g1,g3) = 3
    c: Vertical(g4)
    c: Equal(g0,g4) = 3
    c: Block(g4)
    c: Vertical(g5)
    c: Equal(g1,g5) = 3
    c: Vertical(g6)
    c: Equal(g0,g6) = 3
    c: Block(g6)
    c: Vertical(g7)
    c: Equal(g1,g7) = 3
    c: Vertical(g8)
    c: Equal(g0,g8) = 3
    c: Block(g8)
    c: Vertical(g9)
    c: Equal(g1,g9) = 3
    c: Vertical(g10)
    c: Equal(g0,g10) = 3
    c: Block(g10)
    c: Vertical(g11)
    c: Equal(g1,g11) = 3
    c: Block(g12)
    c: Block(g13)
    c: Block(g14)
    c: Block(g15)
    c: Block(g16)
    c: Block(g17)
    c: Block(g18)
    c: Block(g19)
    c: Block(g20)
    c: Block(g21)
    c: Block(g22)
    c: Block(g23)
    c: Block(g11)
    c: Block(g9)
    c: Block(g7)
    c: Block(g5)
    c: Block(g3)
    c: Block(g1)
    c: Coincident(g24,g0)
    c: Coincident(g24,g12)
    c: Horizontal(g24)
    c: Coincident(g25,g0)
    c: Coincident(g25,g12)
    c: Horizontal(g25)
    c: Coincident(g26,g1)
    c: Coincident(g26,g13)
    c: Horizontal(g26)
    c: Coincident(g27,g1)
    c: Coincident(g27,g13)
    c: Horizontal(g27)
    c: Coincident(g28,g2)
    c: Coincident(g28,g14)
    c: Horizontal(g28)
    c: Coincident(g29,g2)
    c: Coincident(g29,g14)
    c: Horizontal(g29)
    c: Coincident(g30,g3)
    c: Coincident(g30,g15)
    c: Horizontal(g30)
    c: Coincident(g31,g3)
    c: Coincident(g31,g15)
    c: Horizontal(g31)
    c: Coincident(g32,g4)
    c: Coincident(g32,g16)
    c: Horizontal(g32)
    c: Coincident(g33,g4)
    c: Coincident(g33,g16)
    c: Horizontal(g33)
    c: Coincident(g34,g5)
    c: Coincident(g34,g17)
    c: Horizontal(g34)
    c: Coincident(g35,g5)
    c: Coincident(g35,g17)
    c: Horizontal(g35)
    c: Coincident(g36,g6)
    c: Coincident(g36,g19)
    c: Horizontal(g36)
    c: Coincident(g37,g6)
    c: Coincident(g37,g19)
    c: Horizontal(g37)
    c: Coincident(g38,g7)
    c: Coincident(g38,g18)
    c: Horizontal(g38)
    c: Coincident(g39,g7)
    c: Coincident(g39,g18)
    c: Horizontal(g39)
    c: Coincident(g40,g8)
    c: Coincident(g40,g20)
    c: Horizontal(g40)
    c: Coincident(g41,g8)
    c: Coincident(g41,g20)
    c: Horizontal(g41)
    c: Coincident(g42,g9)
    c: Coincident(g42,g23)
    c: Horizontal(g42)
    c: Coincident(g43,g9)
    c: Coincident(g43,g23)
    c: Horizontal(g43)
    c: Coincident(g44,g10)
    c: Coincident(g44,g22)
    c: Horizontal(g44)
    c: Coincident(g45,g10)
    c: Coincident(g45,g22)
    c: Horizontal(g45)
    c: Coincident(g46,g11)
    c: Coincident(g46,g21)
    c: Horizontal(g46)
    c: Coincident(g47,g11)
    c: Coincident(g47,g21)
    c: Horizontal(g47)
FEATURE [Part::Extrusion] Extrude046
  Base = -> Sketch055
  Dir = (1,0,0)
  DirMode = 2
  FaceMakerClass = Part::FaceMakerBullseye
  LengthFwd = 23
  LengthRev = 0
  Placement = pos=(-19,0,0) rot=(0,0,1;0rad)
  Solid = true
  Symmetric = false
FEATURE [Part::Fillet] Fillet038  label="removeToCreateVentalationHoles001"
  Base = -> Extrude046
  Edges = <same value as first occurrence — deduplicated (x4 in doc)>
  Placement = pos=(7,0,0) rot=(0,0,1;0rad)
FEATURE [Sketcher::SketchObject] Sketch056  label="topSketch014"
  FullyConstrained = true
  sketch-geometry (22):
    g0: LineSegment StartX=5.21097e-06 StartY=3 StartZ=0 EndX=5.21097e-06 EndY=19 EndZ=0
    g1: ArcOfCircle CenterX=19 CenterY=19 CenterZ=0 NormalX=0 NormalY=0 NormalZ=1 AngleXU=0 Radius=19 StartAngle=1.5708 EndAngle=3.14159
    g2: ArcOfCircle CenterX=19 CenterY=19 CenterZ=0 NormalX=0 NormalY=0 NormalZ=1 AngleXU=0 Radius=16 StartAngle=1.5708 EndAngle=3.14159
    g3: LineSegment StartX=114 StartY=35 StartZ=0 EndX=19 EndY=35 EndZ=0
    g4: LineSegment StartX=5.21097e-06 StartY=3 StartZ=0 EndX=5.21097e-06 EndY=0 EndZ=0
    g5: LineSegment StartX=3 StartY=0 StartZ=0 EndX=5.21097e-06 EndY=0 EndZ=0
    g6: LineSegment StartX=3 StartY=19 StartZ=0 EndX=3 EndY=0 EndZ=0
    g7: LineSegment StartX=19 StartY=38 StartZ=0 EndX=124 EndY=38 EndZ=0
    g8: Circle CenterX=119 CenterY=35 CenterZ=0 NormalX=0 NormalY=0 NormalZ=1 AngleXU=0 Radius=1
    g9: Circle CenterX=121 CenterY=35 CenterZ=0 NormalX=0 NormalY=0 NormalZ=1 AngleXU=0 Radius=1
    g10: Circle CenterX=121 CenterY=33 CenterZ=0 NormalX=0 NormalY=0 NormalZ=1 AngleXU=0 Radius=1
    g11: BSplineCurve PolesCount=3 KnotsCount=2 Degree=2 IsPeriodic=0
    g12: GeomPoint X=119 Y=35 Z=0
    g13: GeomPoint X=121 Y=33 Z=0
    g14: LineSegment StartX=119 StartY=35 StartZ=0 EndX=114 EndY=35 EndZ=0
    g15: ArcOfCircle CenterX=105 CenterY=19 CenterZ=0 NormalX=0 NormalY=0 NormalZ=1 AngleXU=0 Radius=16 StartAngle=5.60905 EndAngle=6.28319
    g16: LineSegment StartX=121 StartY=33 StartZ=0 EndX=121 EndY=19 EndZ=0
    g17: LineSegment StartX=117.5 StartY=9.01251 StartZ=0 EndX=121.163 EndY=9.0125 EndZ=0
    g18: ArcOfCircle CenterX=105 CenterY=19 CenterZ=0 NormalX=0 NormalY=0 NormalZ=1 AngleXU=0 Radius=20.6155 StartAngle=5.7297 EndAngle=6.28319
    g19: LineSegment StartX=121.163 StartY=9.0125 StartZ=0 EndX=122.538 EndY=8.16329 EndZ=0
    g20: LineSegment StartX=124 StartY=38 StartZ=0 EndX=125.616 EndY=38 EndZ=0
    g21: LineSegment StartX=125.616 StartY=19 StartZ=0 EndX=125.616 EndY=38 EndZ=0
  constraints (49):
    c: Vertical(g0)
    c: Block(g0)
    c: Coincident(g1,g0)
    c: Block(g1)
    c: Coincident(g2,g1)
    c: Block(g2)
    c: Coincident(g3,g2)
    c: Horizontal(g3)
    c: Tangent(g3,g2)
    c: Coincident(g4,g0)
    c: Distance(g4) = 3
    c: Vertical(g4)
    c: Coincident(g5,g4)
    c: Horizontal(g5)
    c: Coincident(g6,g2)
    c: Coincident(g6,g5)
    c: Vertical(g6)
    c: Horizontal(g7)
    c: Distance(g7) = 105
    c: Coincident(g7,g1)
    c: Block(g3)
    c: Weight(g8) = 1
    c: Equal(g8,g9)
    c: Equal(g8,g10)
    c: InternalAlignment(g8,g11)
    c: InternalAlignment(g9,g11)
    c: InternalAlignment(g10,g11)
    c: InternalAlignment(g12,g11)
    c: InternalAlignment(g13,g11)
    c: Block(g11)
    c: Coincident(g14,g11)
    c: Coincident(g14,g3)
    c: Horizontal(g14)
    c: Block(g15)
    c: Coincident(g16,g11)
    c: Coincident(g16,g15)
    c: Vertical(g16)
    c: Distance(g16) = 14
    c: Coincident(g17,g15)
    c: Block(g18)
    c: Coincident(g19,g18)
    c: Coincident(g20,g7)
    c: Horizontal(g20)
    c: Vertical(g21)
    c: Coincident(g20,g21)
    c: Block(g20)
    c: Block(g21)
    c: Block(g19)
    c: Block(g17)
FEATURE [Part::Box] Box026  label="removeToCreteHoleForPlugHousing032"
  AttacherType = Attacher::AttachEngine3D
  Height = 28.6
  Length = 10
  Placement = pos=(-2,0,21.7) rot=(0,0,1;0rad)
  Width = 19
FEATURE [Part::Feature] Face109 .. Face112  x4 (patterned run collapsed; names and placements below)
  shape: bbox 3.5 x 17.8 x 2e-07 mm, 1 faces, 0 solids (baked)
FEATURE [Part::Revolution] Revolve117  label="removeToCreateScrewAndThreadedInsertHole045"
  Angle = 360
  Axis = (0,1,0)
  Base = (0,0,0)
  FaceMakerClass = Part::FaceMakerBullseye
  Placement = pos=(62.3,30.3,19.7) rot=(0,0,1;0rad)
  Solid = false
  Source = -> Face109
  Symmetric = false
FEATURE [Part::Revolution] Revolve118  label="removeToCreateScrewAndThreadedInsertHole046"
  Angle = 360
  Axis = (0,1,0)
  Base = (0,0,0)
  FaceMakerClass = Part::FaceMakerBullseye
  Placement = pos=(62.3,30.3,51.7) rot=(0,0,1;0rad)
  Solid = false
  Source = -> Face110
  Symmetric = false
FEATURE [Part::Revolution] Revolve119  label="removeToCreateScrewAndThreadedInsertHole047"
  Angle = 360
  Axis = (0,1,0)
  Base = (0,0,0)
  FaceMakerClass = Part::FaceMakerBullseye
  Placement = pos=(30.3,30.3,19.7) rot=(0,0,1;0rad)
  Solid = false
  Source = -> Face111
  Symmetric = false
FEATURE [Part::Revolution] Revolve120  label="removeToCreateScrewAndThreadedInsertHole048"
  Angle = 360
  Axis = (0,1,0)
  Base = (0,0,0)
  FaceMakerClass = Part::FaceMakerBullseye
  Placement = pos=(30.3,30.3,51.7) rot=(0,0,1;0rad)
  Solid = false
  Source = -> Face112
  Symmetric = false
FEATURE [Part::MultiFuse] Fusion087  label="createThreadedInsertHolesForFan005"
  Shapes = -> [Revolve117,Revolve118,Revolve119,Revolve120]
FEATURE [Part::Extrusion] Extrude047
  Base = -> Sketch056
  Dir = (0,0,1)
  DirMode = 2
  FaceMakerClass = Part::FaceMakerBullseye
  LengthFwd = 72
  LengthRev = 0
  Solid = true
  Symmetric = false
FEATURE [Part::Fillet] Fillet039  label="top019"
  Base = -> Extrude047
  Edges = 1 edges r=2: [Edge35]
FEATURE [Sketcher::SketchObject] Sketch057
  FullyConstrained = false
  Placement = pos=(0,0,0) rot=(1,0,0;1.5708rad)
  sketch-geometry (24):
    g0: ArcOfCircle CenterX=-4 CenterY=-10.5 CenterZ=0 NormalX=0 NormalY=0 NormalZ=1 AngleXU=0 Radius=1.5 StartAngle=6e-16 EndAngle=3.14159
    g1: ArcOfCircle CenterX=-34.2 CenterY=-10.5 CenterZ=0 NormalX=0 NormalY=0 NormalZ=1 AngleXU=0 Radius=1.5 StartAngle=0 EndAngle=3.14159
    g2: ArcOfCircle CenterX=-34.2 CenterY=-27.7 CenterZ=0 NormalX=0 NormalY=0 NormalZ=1 AngleXU=0 Radius=1.5 StartAngle=3.14159 EndAngle=6.28319
    g3: ArcOfCircle CenterX=-4 CenterY=-27.7 CenterZ=0 NormalX=0 NormalY=0 NormalZ=1 AngleXU=0 Radius=1.5 StartAngle=3.1416 EndAngle=6.28319
    g4: ArcOfCircle CenterX=-10 CenterY=-4.3 CenterZ=0 NormalX=0 NormalY=0 NormalZ=1 AngleXU=0 Radius=1.5 StartAngle=2e-16 EndAngle=3.14159
    g5: ArcOfCircle CenterX=-16.1 CenterY=-1.8 CenterZ=0 NormalX=0 NormalY=0 NormalZ=1 AngleXU=0 Radius=1.5 StartAngle=5e-16 EndAngle=3.14159
    g6: ArcOfCircle CenterX=-22.1 CenterY=-1.8 CenterZ=0 NormalX=0 NormalY=0 NormalZ=1 AngleXU=0 Radius=1.5 StartAngle=5e-16 EndAngle=3.14159
    g7: ArcOfCircle CenterX=-28.2 CenterY=-4.3 CenterZ=0 NormalX=0 NormalY=0 NormalZ=1 AngleXU=0 Radius=1.5 StartAngle=2e-16 EndAngle=3.14159
    g8: ArcOfCircle CenterX=-10 CenterY=-33.9 CenterZ=0 NormalX=0 NormalY=0 NormalZ=1 AngleXU=0 Radius=1.5 StartAngle=3.14159 EndAngle=6.28319
    g9: ArcOfCircle CenterX=-16.1 CenterY=-36.4 CenterZ=0 NormalX=0 NormalY=0 NormalZ=1 AngleXU=0 Radius=1.5 StartAngle=3.14159 EndAngle=6.28319
    g10: ArcOfCircle CenterX=-22.1 CenterY=-36.4 CenterZ=0 NormalX=0 NormalY=0 NormalZ=1 AngleXU=0 Radius=1.5 StartAngle=3.14159 EndAngle=6.28319
    g11: ArcOfCircle CenterX=-28.2 CenterY=-33.9 CenterZ=0 NormalX=0 NormalY=0 NormalZ=1 AngleXU=0 Radius=1.5 StartAngle=3.14159 EndAngle=6.28319
    g12: LineSegment StartX=-35.7 StartY=-10.5 StartZ=0 EndX=-35.7 EndY=-27.7 EndZ=0
    g13: LineSegment StartX=-32.7 StartY=-10.5 StartZ=0 EndX=-32.7 EndY=-27.7 EndZ=0
    g14: LineSegment StartX=-29.7 StartY=-33.9 StartZ=0 EndX=-29.7 EndY=-4.3 EndZ=0
    g15: LineSegment StartX=-26.7 StartY=-33.9 StartZ=0 EndX=-26.7 EndY=-4.3 EndZ=0
    g16: LineSegment StartX=-2.5 StartY=-10.5 StartZ=0 EndX=-2.5 EndY=-27.7 EndZ=0
    g17: LineSegment StartX=-8.5 StartY=-4.3 StartZ=0 EndX=-8.5 EndY=-33.9 EndZ=0
    g18: LineSegment StartX=-5.5 StartY=-10.5 StartZ=0 EndX=-5.5 EndY=-27.7 EndZ=0
    g19: LineSegment StartX=-11.5 StartY=-4.3 StartZ=0 EndX=-11.5 EndY=-33.9 EndZ=0
    g20: LineSegment StartX=-14.6 StartY=-1.8 StartZ=0 EndX=-14.6 EndY=-36.4 EndZ=0
    g21: LineSegment StartX=-17.6 StartY=-1.8 StartZ=0 EndX=-17.6 EndY=-36.4 EndZ=0
    g22: LineSegment StartX=-20.6 StartY=-36.4 StartZ=0 EndX=-20.6 EndY=-1.8 EndZ=0
    g23: LineSegment StartX=-23.6 StartY=-1.8 StartZ=0 EndX=-23.6 EndY=-36.4 EndZ=0
  constraints (48):
    c: Block(g0)
    c: Block(g1)
    c: Block(g2)
    c: Block(g3)
    c: Block(g4)
    c: Block(g5)
    c: Block(g6)
    c: Block(g7)
    c: Block(g8)
    c: Block(g9)
    c: Block(g10)
    c: Block(g11)
    c: Coincident(g12,g1)
    c: Coincident(g12,g2)
    c: Vertical(g12)
    c: Coincident(g13,g1)
    c: Coincident(g13,g2)
    c: Vertical(g13)
    c: Coincident(g14,g11)
    c: Coincident(g14,g7)
    c: Vertical(g14)
    c: Coincident(g15,g11)
    c: Coincident(g15,g7)
    c: Vertical(g15)
    c: Coincident(g16,g0)
    c: Coincident(g16,g3)
    c: Vertical(g16)
    c: Coincident(g17,g4)
    c: Coincident(g17,g8)
    c: Vertical(g17)
    c: Coincident(g18,g0)
    c: Coincident(g18,g3)
    c: Vertical(g18)
    c: Coincident(g19,g4)
    c: Coincident(g19,g8)
    c: Vertical(g19)
    c: Coincident(g20,g5)
    c: Coincident(g20,g9)
    c: Vertical(g20)
    c: Coincident(g21,g5)
    c: Coincident(g21,g9)
    c: Vertical(g21)
    c: Coincident(g22,g10)
    c: Coincident(g22,g6)
    c: Vertical(g22)
    c: Coincident(g23,g6)
    c: Coincident(g23,g10)
    c: Vertical(g23)
FEATURE [Part::Extrusion] Extrude048  label="removeToCreateFanGrillHoles004"
  Base = -> Sketch057
  Dir = (0,-1,6e-16)
  DirMode = 2
  FaceMakerClass = Part::FaceMakerBullseye
  LengthFwd = 10
  LengthRev = 0
  Placement = pos=(65.4,44,54.82) rot=(0,0,1;0rad)
  Solid = true
  Symmetric = false
FEATURE [Part::Cut] Cut040  label="top021"
  Base = -> Fillet039
  Tool = -> Extrude048
FEATURE [Part::Cylinder] Cylinder041  label="removeToCreteHoleForPlugHousing034"
  Angle = 360
  AttacherType = Attacher::AttachEngine3D
  Height = 20
  Placement = pos=(-2,19,36) rot=(0,1,0;1.5708rad)
  Radius = 14.3
FEATURE [Part::MultiFuse] Fusion089  label="removeToCreteHoleForPlugHousing035"
  Shapes = -> [Box026,Cylinder041]
FEATURE [Part::Cylinder] Cylinder042
  Angle = 360
  AttacherType = Attacher::AttachEngine3D
  Height = 20
  Placement = pos=(0,0,36.15) rot=(0,0,1;0rad)
  Radius = 14.3
FEATURE [Part::Cylinder] Cylinder043
  Angle = 360
  AttacherType = Attacher::AttachEngine3D
  Height = 10
  Placement = pos=(0,0,36.15) rot=(0,0,1;0rad)
  Radius = 4
FEATURE [Part::Box] Box027  label="removeToCreteHoleForPlugHousing036"
  AttacherType = Attacher::AttachEngine3D
  Height = 28.6
  Length = 20
  Placement = pos=(106.15,0,21.7) rot=(0,0,1;0rad)
  Width = 19
FEATURE [Part::Cut] Cut041  label="top022"
  Base = -> Cut040
  Tool = -> Fusion087
FEATURE [Part::Cut] Cut039  label="top020"
  Base = -> Cut041
  Tool = -> Fusion089
FEATURE [Part::MultiFuse] Fusion090  label="removeToCreteHoleForPlugHousing037"
  Placement = pos=(70,19,36) rot=(0,1,0;1.5708rad)
  Shapes = -> [Cylinder042,Cylinder043]
FEATURE [Part::MultiFuse] Fusion088  label="removeToCreteHoleForPlugHousing033"
  Shapes = -> [Box027,Fusion090]
FEATURE [Part::Cut] Cut042  label="removeToCreteHoleForPlugHousing038"
  Base = -> Cut039
  Tool = -> Fusion088
FEATURE [Part::MultiFuse] Fusion091  label="removeFromTop"
  Shapes = -> [Fillet038,Fusion085,Fusion084,Fusion083,Extrude045]
FEATURE [Part::Cut] Cut043  label="removeToCreteHoleForPlugHousing039"
  Base = -> Fillet036
  Tool = -> Fusion091
FEATURE [Part::MultiFuse] Fusion092  label="caseScrewPillarBracket016"
  Shapes = -> [Extrude030,Extrude031,Extrude032,Extrude033,Extrude034,Extrude035,Extrude036,Extrude037,Box013,Box014]
FEATURE [Part::MultiFuse] Fusion093  label="bottom012"
  Shapes = -> [Cut034,Fillet037]
FEATURE [Sketcher::SketchObject] Sketch058  label="topSketch015"
  FullyConstrained = true
  sketch-geometry (20):
    g0: LineSegment StartX=5.21097e-06 StartY=3 StartZ=0 EndX=5.21097e-06 EndY=19 EndZ=0
    g1: ArcOfCircle CenterX=19 CenterY=19 CenterZ=0 NormalX=0 NormalY=0 NormalZ=1 AngleXU=0 Radius=19 StartAngle=1.5708 EndAngle=3.14159
    g2: ArcOfCircle CenterX=19 CenterY=19 CenterZ=0 NormalX=0 NormalY=0 NormalZ=1 AngleXU=0 Radius=16 StartAngle=1.5708 EndAngle=3.14159
    g3: LineSegment StartX=114 StartY=35 StartZ=0 EndX=19 EndY=35 EndZ=0
    g4: LineSegment StartX=5.21097e-06 StartY=3 StartZ=0 EndX=5.21097e-06 EndY=0 EndZ=0
    g5: LineSegment StartX=3 StartY=0 StartZ=0 EndX=5.21097e-06 EndY=0 EndZ=0
    g6: LineSegment StartX=3 StartY=19 StartZ=0 EndX=3 EndY=0 EndZ=0
    g7: LineSegment StartX=19 StartY=38 StartZ=0 EndX=124 EndY=38 EndZ=0
    g8: Circle CenterX=119 CenterY=35 CenterZ=0 NormalX=0 NormalY=0 NormalZ=1 AngleXU=0 Radius=1
    g9: Circle CenterX=121 CenterY=35 CenterZ=0 NormalX=0 NormalY=0 NormalZ=1 AngleXU=0 Radius=1
    g10: Circle CenterX=121 CenterY=33 CenterZ=0 NormalX=0 NormalY=0 NormalZ=1 AngleXU=0 Radius=1
    g11: BSplineCurve PolesCount=3 KnotsCount=2 Degree=2 IsPeriodic=0
    g12: GeomPoint X=119 Y=35 Z=0
    g13: GeomPoint X=121 Y=33 Z=0
    g14: LineSegment StartX=119 StartY=35 StartZ=0 EndX=114 EndY=35 EndZ=0
    g15: ArcOfCircle CenterX=105 CenterY=19 CenterZ=0 NormalX=0 NormalY=0 NormalZ=1 AngleXU=0 Radius=19 StartAngle=5.7297 EndAngle=6.28319
    g16: ArcOfCircle CenterX=105 CenterY=19 CenterZ=0 NormalX=0 NormalY=0 NormalZ=1 AngleXU=0 Radius=16 StartAngle=5.60905 EndAngle=6.28319
    g17: LineSegment StartX=121 StartY=33 StartZ=0 EndX=121 EndY=19 EndZ=0
    g18: LineSegment StartX=124 StartY=38 StartZ=0 EndX=124 EndY=19 EndZ=0
    g19: LineSegment StartX=117.5 StartY=9.01251 StartZ=0 EndX=121.163 EndY=9.0125 EndZ=0
  constraints (46):
    c: Vertical(g0)
    c: Block(g0)
    c: Coincident(g1,g0)
    c: Block(g1)
    c: Coincident(g2,g1)
    c: Block(g2)
    c: Coincident(g3,g2)
    c: Horizontal(g3)
    c: Tangent(g3,g2)
    c: Coincident(g4,g0)
    c: Distance(g4) = 3
    c: Vertical(g4)
    c: Coincident(g5,g4)
    c: Horizontal(g5)
    c: Coincident(g6,g2)
    c: Coincident(g6,g5)
    c: Vertical(g6)
    c: Horizontal(g7)
    c: Distance(g7) = 105
    c: Coincident(g7,g1)
    c: Block(g3)
    c: Weight(g8) = 1
    c: Equal(g8,g9)
    c: Equal(g8,g10)
    c: InternalAlignment(g8,g11)
    c: InternalAlignment(g9,g11)
    c: InternalAlignment(g10,g11)
    c: InternalAlignment(g12,g11)
    c: InternalAlignment(g13,g11)
    c: Block(g11)
    c: Coincident(g14,g11)
    c: Coincident(g14,g3)
    c: Horizontal(g14)
    c: Block(g15)
    c: Coincident(g16,g15)
    c: Block(g16)
    c: Coincident(g17,g11)
    c: Coincident(g17,g16)
    c: Vertical(g17)
    c: Distance(g17) = 14
    c: Coincident(g18,g7)
    c: Coincident(g18,g15)
    c: Vertical(g18)
    c: Distance(g18) = 19
    c: Coincident(g19,g16)
    c: Coincident(g19,g15)
FEATURE [Part::Extrusion] Extrude049  label="top023"
  Base = -> Sketch058
  Dir = (0,0,1)
  DirMode = 2
  FaceMakerClass = Part::FaceMakerBullseye
  LengthFwd = 72
  LengthRev = 0
  Solid = true
  Symmetric = false
FEATURE [Sketcher::SketchObject] Sketch059
  FullyConstrained = true
  MapMode = 3
  Placement = pos=(0,0,0) rot=(1,0,0;1.5708rad)
  Support = -> [Extrude049]
  sketch-geometry (8):
    g0: Circle CenterX=80.351 CenterY=-67.6202 CenterZ=0 NormalX=0 NormalY=0 NormalZ=1 AngleXU=0 Radius=2
    g1: Circle CenterX=80.351 CenterY=-67.6202 CenterZ=0 NormalX=0 NormalY=0 NormalZ=1 AngleXU=0 Radius=3
    g2: Circle CenterX=80.351 CenterY=-4.92017 CenterZ=0 NormalX=0 NormalY=0 NormalZ=1 AngleXU=0 Radius=2
    g3: Circle CenterX=80.351 CenterY=-4.92017 CenterZ=0 NormalX=0 NormalY=0 NormalZ=1 AngleXU=0 Radius=3
    g4: Circle CenterX=23.851 CenterY=-4.92017 CenterZ=0 NormalX=0 NormalY=0 NormalZ=1 AngleXU=0 Radius=2
    g5: Circle CenterX=23.851 CenterY=-4.92017 CenterZ=0 NormalX=0 NormalY=0 NormalZ=1 AngleXU=0 Radius=3
    g6: Circle CenterX=23.851 CenterY=-67.6202 CenterZ=0 NormalX=0 NormalY=0 NormalZ=1 AngleXU=0 Radius=2
    g7: Circle CenterX=23.851 CenterY=-67.6202 CenterZ=0 NormalX=0 NormalY=0 NormalZ=1 AngleXU=0 Radius=3
  constraints (8):
    c: Block(g3)
    c: Block(g2)
    c: Block(g1)
    c: Block(g0)
    c: Block(g6)
    c: Block(g7)
    c: Block(g4)
    c: Block(g5)
FEATURE [Sketcher::SketchObject] Sketch060
  FullyConstrained = true
  MapMode = 3
  Placement = pos=(0,0,0) rot=(1,0,0;1.5708rad)
  Support = -> [Extrude049]
  sketch-geometry (8):
    g0: Circle CenterX=80.351 CenterY=-67.6202 CenterZ=0 NormalX=0 NormalY=0 NormalZ=1 AngleXU=0 Radius=3
    g1: Circle CenterX=80.351 CenterY=-4.92017 CenterZ=0 NormalX=0 NormalY=0 NormalZ=1 AngleXU=0 Radius=3
    g2: Circle CenterX=23.851 CenterY=-4.92017 CenterZ=0 NormalX=0 NormalY=0 NormalZ=1 AngleXU=0 Radius=3
    g3: Circle CenterX=23.851 CenterY=-67.6202 CenterZ=0 NormalX=0 NormalY=0 NormalZ=1 AngleXU=0 Radius=3
    g4: Circle CenterX=23.851 CenterY=-67.6202 CenterZ=0 NormalX=0 NormalY=0 NormalZ=1 AngleXU=0 Radius=5
    g5: Circle CenterX=80.351 CenterY=-67.6202 CenterZ=0 NormalX=0 NormalY=0 NormalZ=1 AngleXU=0 Radius=5
    g6: Circle CenterX=23.851 CenterY=-4.92017 CenterZ=0 NormalX=0 NormalY=0 NormalZ=1 AngleXU=0 Radius=5
    g7: Circle CenterX=80.351 CenterY=-4.92017 CenterZ=0 NormalX=0 NormalY=0 NormalZ=1 AngleXU=0 Radius=5
  constraints (8):
    c: Block(g1)
    c: Block(g0)
    c: Block(g3)
    c: Block(g2)
    c: Block(g5)
    c: Block(g4)
    c: Block(g6)
    c: Block(g7)
FEATURE [Sketcher::SketchObject] Sketch061
  FullyConstrained = true
  MapMode = 3
  Placement = pos=(0,0,0) rot=(1,0,0;1.5708rad)
  sketch-geometry (8):
    g0: Circle CenterX=80.351 CenterY=-67.6202 CenterZ=0 NormalX=0 NormalY=0 NormalZ=1 AngleXU=0 Radius=3
    g1: Circle CenterX=80.351 CenterY=-4.92017 CenterZ=0 NormalX=0 NormalY=0 NormalZ=1 AngleXU=0 Radius=3
    g2: Circle CenterX=23.851 CenterY=-4.92017 CenterZ=0 NormalX=0 NormalY=0 NormalZ=1 AngleXU=0 Radius=3
    g3: Circle CenterX=23.851 CenterY=-67.6202 CenterZ=0 NormalX=0 NormalY=0 NormalZ=1 AngleXU=0 Radius=3
    g4: Circle CenterX=23.851 CenterY=-67.6202 CenterZ=0 NormalX=0 NormalY=0 NormalZ=1 AngleXU=0 Radius=5
    g5: Circle CenterX=80.351 CenterY=-67.6202 CenterZ=0 NormalX=0 NormalY=0 NormalZ=1 AngleXU=0 Radius=5
    g6: Circle CenterX=23.851 CenterY=-4.92017 CenterZ=0 NormalX=0 NormalY=0 NormalZ=1 AngleXU=0 Radius=5
    g7: Circle CenterX=80.351 CenterY=-4.92017 CenterZ=0 NormalX=0 NormalY=0 NormalZ=1 AngleXU=0 Radius=5
  constraints (8):
    c: Block(g1)
    c: Block(g0)
    c: Block(g3)
    c: Block(g2)
    c: Block(g5)
    c: Block(g4)
    c: Block(g6)
    c: Block(g7)
FEATURE [Sketcher::SketchObject] Sketch062  label="topSketch016"
  FullyConstrained = true
  sketch-geometry (20):
    g0: LineSegment StartX=5.21097e-06 StartY=3 StartZ=0 EndX=5.21097e-06 EndY=19 EndZ=0
    g1: ArcOfCircle CenterX=19 CenterY=19 CenterZ=0 NormalX=0 NormalY=0 NormalZ=1 AngleXU=0 Radius=19 StartAngle=1.5708 EndAngle=3.14159
    g2: ArcOfCircle CenterX=19 CenterY=19 CenterZ=0 NormalX=0 NormalY=0 NormalZ=1 AngleXU=0 Radius=16 StartAngle=1.5708 EndAngle=3.14159
    g3: LineSegment StartX=114 StartY=35 StartZ=0 EndX=19 EndY=35 EndZ=0
    g4: LineSegment StartX=5.21097e-06 StartY=3 StartZ=0 EndX=5.21097e-06 EndY=0 EndZ=0
    g5: LineSegment StartX=3 StartY=0 StartZ=0 EndX=5.21097e-06 EndY=0 EndZ=0
    g6: LineSegment StartX=3 StartY=19 StartZ=0 EndX=3 EndY=0 EndZ=0
    g7: LineSegment StartX=19 StartY=38 StartZ=0 EndX=124 EndY=38 EndZ=0
    g8: Circle CenterX=119 CenterY=35 CenterZ=0 NormalX=0 NormalY=0 NormalZ=1 AngleXU=0 Radius=1
    g9: Circle CenterX=121 CenterY=35 CenterZ=0 NormalX=0 NormalY=0 NormalZ=1 AngleXU=0 Radius=1
    g10: Circle CenterX=121 CenterY=33 CenterZ=0 NormalX=0 NormalY=0 NormalZ=1 AngleXU=0 Radius=1
    g11: BSplineCurve PolesCount=3 KnotsCount=2 Degree=2 IsPeriodic=0
    g12: GeomPoint X=119 Y=35 Z=0
    g13: GeomPoint X=121 Y=33 Z=0
    g14: LineSegment StartX=119 StartY=35 StartZ=0 EndX=114 EndY=35 EndZ=0
    g15: ArcOfCircle CenterX=105 CenterY=19 CenterZ=0 NormalX=0 NormalY=0 NormalZ=1 AngleXU=0 Radius=19 StartAngle=5.7297 EndAngle=6.28319
    g16: ArcOfCircle CenterX=105 CenterY=19 CenterZ=0 NormalX=0 NormalY=0 NormalZ=1 AngleXU=0 Radius=16 StartAngle=5.60905 EndAngle=6.28319
    g17: LineSegment StartX=121 StartY=33 StartZ=0 EndX=121 EndY=19 EndZ=0
    g18: LineSegment StartX=124 StartY=38 StartZ=0 EndX=124 EndY=19 EndZ=0
    g19: LineSegment StartX=117.5 StartY=9.01251 StartZ=0 EndX=121.163 EndY=9.0125 EndZ=0
  constraints (46):
    c: Vertical(g0)
    c: Block(g0)
    c: Coincident(g1,g0)
    c: Block(g1)
    c: Coincident(g2,g1)
    c: Block(g2)
    c: Coincident(g3,g2)
    c: Horizontal(g3)
    c: Tangent(g3,g2)
    c: Coincident(g4,g0)
    c: Distance(g4) = 3
    c: Vertical(g4)
    c: Coincident(g5,g4)
    c: Horizontal(g5)
    c: Coincident(g6,g2)
    c: Coincident(g6,g5)
    c: Vertical(g6)
    c: Horizontal(g7)
    c: Distance(g7) = 105
    c: Coincident(g7,g1)
    c: Block(g3)
    c: Weight(g8) = 1
    c: Equal(g8,g9)
    c: Equal(g8,g10)
    c: InternalAlignment(g8,g11)
    c: InternalAlignment(g9,g11)
    c: InternalAlignment(g10,g11)
    c: InternalAlignment(g12,g11)
    c: InternalAlignment(g13,g11)
    c: Block(g11)
    c: Coincident(g14,g11)
    c: Coincident(g14,g3)
    c: Horizontal(g14)
    c: Block(g15)
    c: Coincident(g16,g15)
    c: Block(g16)
    c: Coincident(g17,g11)
    c: Coincident(g17,g16)
    c: Vertical(g17)
    c: Distance(g17) = 14
    c: Coincident(g18,g7)
    c: Coincident(g18,g15)
    c: Vertical(g18)
    c: Distance(g18) = 19
    c: Coincident(g19,g16)
    c: Coincident(g19,g15)
FEATURE [Part::Extrusion] Extrude053  label="top024"
  Base = -> Sketch062
  Dir = (0,0,1)
  DirMode = 2
  FaceMakerClass = Part::FaceMakerBullseye
  LengthFwd = 72
  LengthRev = 0
  Solid = true
  Symmetric = false
FEATURE [Sketcher::SketchObject] Sketch063
  FullyConstrained = true
  MapMode = 3
  Placement = pos=(0,0,0) rot=(1,0,0;1.5708rad)
  Support = -> [Extrude053]
  sketch-geometry (8):
    g0: Circle CenterX=80.351 CenterY=-67.6202 CenterZ=0 NormalX=0 NormalY=0 NormalZ=1 AngleXU=0 Radius=2
    g1: Circle CenterX=80.351 CenterY=-67.6202 CenterZ=0 NormalX=0 NormalY=0 NormalZ=1 AngleXU=0 Radius=3
    g2: Circle CenterX=80.351 CenterY=-4.92017 CenterZ=0 NormalX=0 NormalY=0 NormalZ=1 AngleXU=0 Radius=2
    g3: Circle CenterX=80.351 CenterY=-4.92017 CenterZ=0 NormalX=0 NormalY=0 NormalZ=1 AngleXU=0 Radius=3
    g4: Circle CenterX=23.851 CenterY=-4.92017 CenterZ=0 NormalX=0 NormalY=0 NormalZ=1 AngleXU=0 Radius=2
    g5: Circle CenterX=23.851 CenterY=-4.92017 CenterZ=0 NormalX=0 NormalY=0 NormalZ=1 AngleXU=0 Radius=3
    g6: Circle CenterX=23.851 CenterY=-67.6202 CenterZ=0 NormalX=0 NormalY=0 NormalZ=1 AngleXU=0 Radius=2
    g7: Circle CenterX=23.851 CenterY=-67.6202 CenterZ=0 NormalX=0 NormalY=0 NormalZ=1 AngleXU=0 Radius=3
  constraints (8):
    c: Block(g3)
    c: Block(g2)
    c: Block(g1)
    c: Block(g0)
    c: Block(g6)
    c: Block(g7)
    c: Block(g4)
    c: Block(g5)
FEATURE [Part::Extrusion] Extrude054
  Base = -> Sketch063
  Dir = (0,-1,2e-16)
  DirMode = 2
  FaceMakerClass = Part::FaceMakerBullseye
  LengthFwd = 6
  LengthRev = 0
  Placement = pos=(0,9,0) rot=(0,0,1;0rad)
  Solid = true
  Symmetric = false
FEATURE [Sketcher::SketchObject] Sketch064  label="topSketch017"
  FullyConstrained = true
  sketch-geometry (20):
    g0: LineSegment StartX=5.21097e-06 StartY=3 StartZ=0 EndX=5.21097e-06 EndY=19 EndZ=0
    g1: ArcOfCircle CenterX=19 CenterY=19 CenterZ=0 NormalX=0 NormalY=0 NormalZ=1 AngleXU=0 Radius=19 StartAngle=1.5708 EndAngle=3.14159
    g2: ArcOfCircle CenterX=19 CenterY=19 CenterZ=0 NormalX=0 NormalY=0 NormalZ=1 AngleXU=0 Radius=16 StartAngle=1.5708 EndAngle=3.14159
    g3: LineSegment StartX=114 StartY=35 StartZ=0 EndX=19 EndY=35 EndZ=0
    g4: LineSegment StartX=5.21097e-06 StartY=3 StartZ=0 EndX=5.21097e-06 EndY=0 EndZ=0
    g5: LineSegment StartX=3 StartY=0 StartZ=0 EndX=5.21097e-06 EndY=0 EndZ=0
    g6: LineSegment StartX=3 StartY=19 StartZ=0 EndX=3 EndY=0 EndZ=0
    g7: LineSegment StartX=19 StartY=38 StartZ=0 EndX=124 EndY=38 EndZ=0
    g8: Circle CenterX=119 CenterY=35 CenterZ=0 NormalX=0 NormalY=0 NormalZ=1 AngleXU=0 Radius=1
    g9: Circle CenterX=121 CenterY=35 CenterZ=0 NormalX=0 NormalY=0 NormalZ=1 AngleXU=0 Radius=1
    g10: Circle CenterX=121 CenterY=33 CenterZ=0 NormalX=0 NormalY=0 NormalZ=1 AngleXU=0 Radius=1
    g11: BSplineCurve PolesCount=3 KnotsCount=2 Degree=2 IsPeriodic=0
    g12: GeomPoint X=119 Y=35 Z=0
    g13: GeomPoint X=121 Y=33 Z=0
    g14: LineSegment StartX=119 StartY=35 StartZ=0 EndX=114 EndY=35 EndZ=0
    g15: ArcOfCircle CenterX=105 CenterY=19 CenterZ=0 NormalX=0 NormalY=0 NormalZ=1 AngleXU=0 Radius=19 StartAngle=5.7297 EndAngle=6.28319
    g16: ArcOfCircle CenterX=105 CenterY=19 CenterZ=0 NormalX=0 NormalY=0 NormalZ=1 AngleXU=0 Radius=16 StartAngle=5.60905 EndAngle=6.28319
    g17: LineSegment StartX=121 StartY=33 StartZ=0 EndX=121 EndY=19 EndZ=0
    g18: LineSegment StartX=124 StartY=38 StartZ=0 EndX=124 EndY=19 EndZ=0
    g19: LineSegment StartX=117.5 StartY=9.01251 StartZ=0 EndX=121.163 EndY=9.0125 EndZ=0
  constraints (46):
    c: Vertical(g0)
    c: Block(g0)
    c: Coincident(g1,g0)
    c: Block(g1)
    c: Coincident(g2,g1)
    c: Block(g2)
    c: Coincident(g3,g2)
    c: Horizontal(g3)
    c: Tangent(g3,g2)
    c: Coincident(g4,g0)
    c: Distance(g4) = 3
    c: Vertical(g4)
    c: Coincident(g5,g4)
    c: Horizontal(g5)
    c: Coincident(g6,g2)
    c: Coincident(g6,g5)
    c: Vertical(g6)
    c: Horizontal(g7)
    c: Distance(g7) = 105
    c: Coincident(g7,g1)
    c: Block(g3)
    c: Weight(g8) = 1
    c: Equal(g8,g9)
    c: Equal(g8,g10)
    c: InternalAlignment(g8,g11)
    c: InternalAlignment(g9,g11)
    c: InternalAlignment(g10,g11)
    c: InternalAlignment(g12,g11)
    c: InternalAlignment(g13,g11)
    c: Block(g11)
    c: Coincident(g14,g11)
    c: Coincident(g14,g3)
    c: Horizontal(g14)
    c: Block(g15)
    c: Coincident(g16,g15)
    c: Block(g16)
    c: Coincident(g17,g11)
    c: Coincident(g17,g16)
    c: Vertical(g17)
    c: Distance(g17) = 14
    c: Coincident(g18,g7)
    c: Coincident(g18,g15)
    c: Vertical(g18)
    c: Distance(g18) = 19
    c: Coincident(g19,g16)
    c: Coincident(g19,g15)
FEATURE [Sketcher::SketchObject] Sketch065
  FullyConstrained = true
  MapMode = 3
  Placement = pos=(0,0,0) rot=(1,0,0;1.5708rad)
  sketch-geometry (8):
    g0: Circle CenterX=80.351 CenterY=-67.6202 CenterZ=0 NormalX=0 NormalY=0 NormalZ=1 AngleXU=0 Radius=3
    g1: Circle CenterX=80.351 CenterY=-4.92017 CenterZ=0 NormalX=0 NormalY=0 NormalZ=1 AngleXU=0 Radius=3
    g2: Circle CenterX=23.851 CenterY=-4.92017 CenterZ=0 NormalX=0 NormalY=0 NormalZ=1 AngleXU=0 Radius=3
    g3: Circle CenterX=23.851 CenterY=-67.6202 CenterZ=0 NormalX=0 NormalY=0 NormalZ=1 AngleXU=0 Radius=3
    g4: Circle CenterX=23.851 CenterY=-67.6202 CenterZ=0 NormalX=0 NormalY=0 NormalZ=1 AngleXU=0 Radius=5
    g5: Circle CenterX=80.351 CenterY=-67.6202 CenterZ=0 NormalX=0 NormalY=0 NormalZ=1 AngleXU=0 Radius=5
    g6: Circle CenterX=23.851 CenterY=-4.92017 CenterZ=0 NormalX=0 NormalY=0 NormalZ=1 AngleXU=0 Radius=5
    g7: Circle CenterX=80.351 CenterY=-4.92017 CenterZ=0 NormalX=0 NormalY=0 NormalZ=1 AngleXU=0 Radius=5
  constraints (8):
    c: Block(g1)
    c: Block(g0)
    c: Block(g3)
    c: Block(g2)
    c: Block(g5)
    c: Block(g4)
    c: Block(g6)
    c: Block(g7)
FEATURE [Part::Extrusion] Extrude056
  Base = -> Sketch065
  Dir = (0,-1,2e-16)
  DirMode = 2
  FaceMakerClass = Part::FaceMakerBullseye
  LengthFwd = 2
  LengthRev = 0
  Solid = true
  Symmetric = false
FEATURE [Part::Extrusion] Extrude057  label="top025"
  Base = -> Sketch064
  Dir = (0,0,1)
  DirMode = 2
  FaceMakerClass = Part::FaceMakerBullseye
  LengthFwd = 72
  LengthRev = 0
  Solid = true
  Symmetric = false
FEATURE [Sketcher::SketchObject] Sketch066
  FullyConstrained = true
  MapMode = 3
  Placement = pos=(0,0,0) rot=(1,0,0;1.5708rad)
  Support = -> [Extrude057]
  sketch-geometry (8):
    g0: Circle CenterX=80.351 CenterY=-67.6202 CenterZ=0 NormalX=0 NormalY=0 NormalZ=1 AngleXU=0 Radius=3
    g1: Circle CenterX=80.351 CenterY=-4.92017 CenterZ=0 NormalX=0 NormalY=0 NormalZ=1 AngleXU=0 Radius=3
    g2: Circle CenterX=23.851 CenterY=-4.92017 CenterZ=0 NormalX=0 NormalY=0 NormalZ=1 AngleXU=0 Radius=3
    g3: Circle CenterX=23.851 CenterY=-67.6202 CenterZ=0 NormalX=0 NormalY=0 NormalZ=1 AngleXU=0 Radius=3
    g4: Circle CenterX=23.851 CenterY=-67.6202 CenterZ=0 NormalX=0 NormalY=0 NormalZ=1 AngleXU=0 Radius=5
    g5: Circle CenterX=80.351 CenterY=-67.6202 CenterZ=0 NormalX=0 NormalY=0 NormalZ=1 AngleXU=0 Radius=5
    g6: Circle CenterX=23.851 CenterY=-4.92017 CenterZ=0 NormalX=0 NormalY=0 NormalZ=1 AngleXU=0 Radius=5
    g7: Circle CenterX=80.351 CenterY=-4.92017 CenterZ=0 NormalX=0 NormalY=0 NormalZ=1 AngleXU=0 Radius=5
  constraints (8):
    c: Block(g1)
    c: Block(g0)
    c: Block(g3)
    c: Block(g2)
    c: Block(g5)
    c: Block(g4)
    c: Block(g6)
    c: Block(g7)
FEATURE [Part::Extrusion] Extrude055
  Base = -> Sketch066
  Dir = (0,-1,2e-16)
  DirMode = 2
  FaceMakerClass = Part::FaceMakerBullseye
  LengthFwd = 2
  LengthRev = 0
  Solid = true
  Symmetric = false
FEATURE [Part::Fillet] Fillet041
  Base = -> Extrude056
  Edges = 4 edges r=1.99: [Edge6,Edge12,Edge18,Edge24]
FEATURE [Part::Cut] Cut045
  Base = -> Extrude055
  Placement = pos=(0,6,0) rot=(0,0,1;0rad)
  Tool = -> Fillet041
FEATURE [Part::MultiFuse] Fusion095  label="pcbScrewPillars"
  Placement = pos=(-3.2,-1,72.3) rot=(0,0,1;0rad)
  Shapes = -> [Cut045,Extrude054]
FEATURE [Part::Feature] Face113
  shape: bbox 3.2 x 1.5 x 2e-07 mm, 1 faces, 0 solids (baked)
FEATURE [Part::Revolution] Revolve121  label="backCaseScrewRetainer002"
  Angle = 360
  Axis = (0,1,0)
  Base = (0,0,0)
  FaceMakerClass = Part::FaceMakerBullseye
  Placement = pos=(12.5,3,62) rot=(0,0,1;0rad)
  Solid = false
  Source = -> Face113
  Symmetric = false
FEATURE [Part::Feature] Face114
  shape: bbox 3.2 x 1.5 x 2e-07 mm, 1 faces, 0 solids (baked)
FEATURE [Part::Feature] Face115
  shape: bbox 3.2 x 1.5 x 2e-07 mm, 1 faces, 0 solids (baked)
FEATURE [Part::Feature] Face116
  shape: bbox 3.2 x 1.5 x 2e-07 mm, 1 faces, 0 solids (baked)
FEATURE [Part::Revolution] Revolve122  label="frontCaseScrewRetainer004"
  Angle = 360
  Axis = (0,1,0)
  Base = (0,0,0)
  FaceMakerClass = Part::FaceMakerBullseye
  Placement = pos=(89.5,3,68.5) rot=(0,0,1;0rad)
  Solid = false
  Source = -> Face115
  Symmetric = false
FEATURE [Part::Revolution] Revolve123  label="frontCaseScrewRetainer005"
  Angle = 360
  Axis = (0,1,0)
  Base = (0,0,0)
  FaceMakerClass = Part::FaceMakerBullseye
  Placement = pos=(89.5,3,3.5) rot=(0,0,1;0rad)
  Solid = false
  Source = -> Face116
  Symmetric = false
FEATURE [Part::Revolution] Revolve124  label="backCaseScrewRetainer003"
  Angle = 360
  Axis = (0,1,0)
  Base = (0,0,0)
  FaceMakerClass = Part::FaceMakerBullseye
  Placement = pos=(12.5,3,10) rot=(0,0,1;0rad)
  Solid = false
  Source = -> Face114
  Symmetric = false
FEATURE [Part::Feature] Face117
  shape: bbox 3.6 x 3.2 x 2e-07 mm, 1 faces, 0 solids (baked)
FEATURE [Part::Revolution] Revolve125  label="moreFrontCaseScrewRetainer004"
  Angle = 360
  Axis = (0,1,0)
  Base = (0,0,0)
  FaceMakerClass = Part::FaceMakerBullseye
  Placement = pos=(109.5,4.5,68.5) rot=(0,0,1;0rad)
  Solid = false
  Source = -> Face117
  Symmetric = false
FEATURE [Part::Feature] Face118
  shape: bbox 3.6 x 3.2 x 2e-07 mm, 1 faces, 0 solids (baked)
FEATURE [Part::Revolution] Revolve126  label="moreFrontCaseScrewRetainer005"
  Angle = 360
  Axis = (0,1,0)
  Base = (0,0,0)
  FaceMakerClass = Part::FaceMakerBullseye
  Placement = pos=(109.5,4.5,3.5) rot=(0,0,1;0rad)
  Solid = false
  Source = -> Face118
  Symmetric = false
FEATURE [Part::MultiFuse] Fusion096  label="screwRetainers001"
  Shapes = -> [Revolve126,Revolve125,Revolve124,Revolve123,Revolve122,Revolve121]
FEATURE [Part::Feature] Face119
  shape: bbox 10 x 16.5 x 2e-07 mm, 1 faces, 0 solids (baked)
FEATURE [Part::Revolution] Revolve130  label="plugHousing050"
  Angle = 360
  Axis = (0,1,0)
  Base = (0,0,0)
  FaceMakerClass = Part::FaceMakerBullseye
  Placement = pos=(0,0,36.15) rot=(0,0,1;0rad)
  Solid = false
  Source = -> Face119
  Symmetric = false
FEATURE [Part::Feature] Face120
  shape: bbox 10 x 16.5 x 2e-07 mm, 1 faces, 0 solids (baked)
FEATURE [Part::Feature] Face121
  shape: bbox 10 x 16.5 x 2e-07 mm, 1 faces, 0 solids (baked)
FEATURE [Part::Revolution] Revolve127  label="plugHousing047"
  Angle = 360
  Axis = (0,1,0)
  Base = (0,0,0)
  FaceMakerClass = Part::FaceMakerBullseye
  Placement = pos=(0,0,36.15) rot=(0,0,1;0rad)
  Solid = false
  Source = -> Face121
  Symmetric = false
FEATURE [Part::Feature] Face122
  shape: bbox 10 x 16.5 x 2e-07 mm, 1 faces, 0 solids (baked)
FEATURE [Part::Feature] Face123
  shape: bbox 10 x 16.5 x 2e-07 mm, 1 faces, 0 solids (baked)
FEATURE [Part::Revolution] Revolve128  label="plugHousing048"
  Angle = 360
  Axis = (0,1,0)
  Base = (0,0,0)
  FaceMakerClass = Part::FaceMakerBullseye
  Placement = pos=(0,0,36.15) rot=(0,0,1;0rad)
  Solid = false
  Source = -> Face123
  Symmetric = false
FEATURE [Part::MultiFuse] Fusion100  label="plugHousing054"
  Placement = pos=(0,0,0) rot=(0,0,1;1.5708rad)
  Shapes = -> [Revolve130,Revolve128]
FEATURE [Part::Feature] Face124
  shape: bbox 10 x 16.5 x 2e-07 mm, 1 faces, 0 solids (baked)
FEATURE [Part::Feature] Face125
  shape: bbox 10 x 16.5 x 2e-07 mm, 1 faces, 0 solids (baked)
FEATURE [Part::Revolution] Revolve129  label="plugHousing049"
  Angle = 360
  Axis = (0,1,0)
  Base = (0,0,0)
  FaceMakerClass = Part::FaceMakerBullseye
  Placement = pos=(0,0,36.15) rot=(0,0,1;0rad)
  Solid = false
  Source = -> Face125
  Symmetric = false
FEATURE [Part::Feature] Face126
  shape: bbox 10 x 16.5 x 2e-07 mm, 1 faces, 0 solids (baked)
FEATURE [Part::Revolution] Revolve131  label="plugHousing058"
  Angle = 360
  Axis = (0,1,0)
  Base = (0,0,0)
  FaceMakerClass = Part::FaceMakerBullseye
  Placement = pos=(0,0,36.15) rot=(0,0,1;0rad)
  Solid = false
  Source = -> Face120
  Symmetric = false
FEATURE [Part::MultiFuse] Fusion099  label="plugHousing053"
  Placement = pos=(0,0,0) rot=(0,0,1;1.5708rad)
  Shapes = -> [Revolve127,Revolve131]
FEATURE [Part::MultiFuse] Fusion102  label="plugHousing056"
  Placement = pos=(0,19,0) rot=(0,0,1;3.14159rad)
  Shapes = -> [Fusion100,Fusion099]
FEATURE [Part::Revolution] Revolve132  label="plugHousing059"
  Angle = 360
  Axis = (0,1,0)
  Base = (0,0,0)
  FaceMakerClass = Part::FaceMakerBullseye
  Placement = pos=(0,0,36.15) rot=(0,0,1;0rad)
  Solid = false
  Source = -> Face126
  Symmetric = false
FEATURE [Part::Revolution] Revolve133  label="plugHousing060"
  Angle = 360
  Axis = (0,1,0)
  Base = (0,0,0)
  FaceMakerClass = Part::FaceMakerBullseye
  Placement = pos=(0,0,36.15) rot=(0,0,1;0rad)
  Solid = false
  Source = -> Face122
  Symmetric = false
FEATURE [Part::MultiFuse] Fusion097  label="plugHousing051"
  Placement = pos=(0,0,0) rot=(0,0,1;1.5708rad)
  Shapes = -> [Revolve133,Revolve132]
FEATURE [Part::Revolution] Revolve134  label="plugHousing061"
  Angle = 360
  Axis = (0,1,0)
  Base = (0,0,0)
  FaceMakerClass = Part::FaceMakerBullseye
  Placement = pos=(0,0,36.15) rot=(0,0,1;0rad)
  Solid = false
  Source = -> Face124
  Symmetric = false
FEATURE [Part::MultiFuse] Fusion101  label="plugHousing055"
  Placement = pos=(0,0,0) rot=(0,0,1;1.5708rad)
  Shapes = -> [Revolve129,Revolve134]
FEATURE [Part::MultiFuse] Fusion098  label="plugHousing052"
  Placement = pos=(0,19,0) rot=(0,0,1;3.14159rad)
  Shapes = -> [Fusion097,Fusion101]
FEATURE [Part::MultiFuse] Fusion103  label="plugHousing057"
  Placement = pos=(122.621,0,-0.15) rot=(0,0,1;0rad)
  Shapes = -> [Fusion102,Fusion098]
FEATURE [Part::Box] Box028  label="Cube015"
  AttacherType = Attacher::AttachEngine3D
  Height = 28
  Length = 3
  Placement = pos=(110.7,19,22) rot=(0,0,1;0rad)
  Width = 15.7
FEATURE [Part::Cylinder] Cylinder044
  Angle = 360
  AttacherType = Attacher::AttachEngine3D
  Height = 20
  Placement = pos=(0,0,36.15) rot=(0,0,1;0rad)
  Radius = 10.3
FEATURE [Part::Cylinder] Cylinder045
  Angle = 360
  AttacherType = Attacher::AttachEngine3D
  Height = 10
  Placement = pos=(0,0,36.15) rot=(0,0,1;0rad)
  Radius = 4
FEATURE [Part::MultiFuse] Fusion104  label="removeToCreteHoleForPlugHousing040"
  Placement = pos=(70,19,36) rot=(0,1,0;1.5708rad)
  Shapes = -> [Cylinder044,Cylinder045]
FEATURE [Part::Cut] Cut046  label="plugHousingTab003"
  Base = -> Box028
  Tool = -> Fusion104
FEATURE [Part::MultiFuse] Fusion105  label="plugHousing062"
  Shapes = -> [Fusion103,Cut046]
FEATURE [Part::Fillet] Fillet042
  Base = -> Fusion105
  Edges = 1 edges r=2: [Edge25]
FEATURE [Part::Fillet] Fillet043  label="plugHousing063"
  Base = -> Fillet042
  Edges = 1 edges r=2: [Edge8]
  Placement = pos=(7,0,0) rot=(0,0,1;0rad)
FEATURE [Part::Feature] Face127
  shape: bbox 10 x 16.5 x 2e-07 mm, 1 faces, 0 solids (baked)
FEATURE [Part::Feature] Face128
  shape: bbox 10 x 16.5 x 2e-07 mm, 1 faces, 0 solids (baked)
FEATURE [Part::Revolution] Revolve137  label="plugHousing070"
  Angle = 360
  Axis = (0,1,0)
  Base = (0,0,0)
  FaceMakerClass = Part::FaceMakerBullseye
  Placement = pos=(0,0,36.15) rot=(0,0,1;0rad)
  Solid = false
  Source = -> Face127
  Symmetric = false
FEATURE [Part::Revolution] Revolve140  label="plugHousing073"
  Angle = 360
  Axis = (0,1,0)
  Base = (0,0,0)
  FaceMakerClass = Part::FaceMakerBullseye
  Placement = pos=(0,0,36.15) rot=(0,0,1;0rad)
  Solid = false
  Source = -> Face128
  Symmetric = false
FEATURE [Part::Feature] Face129
  shape: bbox 10 x 16.5 x 2e-07 mm, 1 faces, 0 solids (baked)
FEATURE [Part::Revolution] Revolve138  label="plugHousing071"
  Angle = 360
  Axis = (0,1,0)
  Base = (0,0,0)
  FaceMakerClass = Part::FaceMakerBullseye
  Placement = pos=(0,0,36.15) rot=(0,0,1;0rad)
  Solid = false
  Source = -> Face129
  Symmetric = false
FEATURE [Part::Feature] Face130
  shape: bbox 10 x 16.5 x 2e-07 mm, 1 faces, 0 solids (baked)
FEATURE [Part::Revolution] Revolve139  label="plugHousing072"
  Angle = 360
  Axis = (0,1,0)
  Base = (0,0,0)
  FaceMakerClass = Part::FaceMakerBullseye
  Placement = pos=(0,0,36.15) rot=(0,0,1;0rad)
  Solid = false
  Source = -> Face130
  Symmetric = false
FEATURE [Part::Feature] Face131
  shape: bbox 10 x 16.5 x 2e-07 mm, 1 faces, 0 solids (baked)
FEATURE [Part::Revolution] Revolve135  label="plugHousing068"
  Angle = 360
  Axis = (0,1,0)
  Base = (0,0,0)
  FaceMakerClass = Part::FaceMakerBullseye
  Placement = pos=(0,0,36.15) rot=(0,0,1;0rad)
  Solid = false
  Source = -> Face131
  Symmetric = false
FEATURE [Part::MultiFuse] Fusion112  label="plugHousing078"
  Placement = pos=(0,0,0) rot=(0,0,1;1.5708rad)
  Shapes = -> [Revolve135,Revolve139]
FEATURE [Part::Feature] Face132
  shape: bbox 10 x 16.5 x 2e-07 mm, 1 faces, 0 solids (baked)
FEATURE [Part::Revolution] Revolve141  label="plugHousing074"
  Angle = 360
  Axis = (0,1,0)
  Base = (0,0,0)
  FaceMakerClass = Part::FaceMakerBullseye
  Placement = pos=(0,0,36.15) rot=(0,0,1;0rad)
  Solid = false
  Source = -> Face132
  Symmetric = false
FEATURE [Part::MultiFuse] Fusion110  label="plugHousing076"
  Placement = pos=(0,0,0) rot=(0,0,1;1.5708rad)
  Shapes = -> [Revolve141,Revolve140]
FEATURE [Part::Feature] Face133
  shape: bbox 10 x 16.5 x 2e-07 mm, 1 faces, 0 solids (baked)
FEATURE [Part::Revolution] Revolve136  label="plugHousing069"
  Angle = 360
  Axis = (0,1,0)
  Base = (0,0,0)
  FaceMakerClass = Part::FaceMakerBullseye
  Placement = pos=(0,0,36.15) rot=(0,0,1;0rad)
  Solid = false
  Source = -> Face133
  Symmetric = false
FEATURE [Part::MultiFuse] Fusion106  label="plugHousing064"
  Placement = pos=(0,0,0) rot=(0,0,1;1.5708rad)
  Shapes = -> [Revolve138,Revolve136]
FEATURE [Part::MultiFuse] Fusion108  label="plugHousing066"
  Placement = pos=(0,19,0) rot=(0,0,1;3.14159rad)
  Shapes = -> [Fusion106,Fusion112]
FEATURE [Part::Feature] Face134
  shape: bbox 10 x 16.5 x 2e-07 mm, 1 faces, 0 solids (baked)
FEATURE [Part::Revolution] Revolve142  label="plugHousing075"
  Angle = 360
  Axis = (0,1,0)
  Base = (0,0,0)
  FaceMakerClass = Part::FaceMakerBullseye
  Placement = pos=(0,0,36.15) rot=(0,0,1;0rad)
  Solid = false
  Source = -> Face134
  Symmetric = false
FEATURE [Part::MultiFuse] Fusion107  label="plugHousing065"
  Placement = pos=(0,0,0) rot=(0,0,1;1.5708rad)
  Shapes = -> [Revolve137,Revolve142]
FEATURE [Part::MultiFuse] Fusion111  label="plugHousing077"
  Placement = pos=(0,19,0) rot=(0,0,1;3.14159rad)
  Shapes = -> [Fusion110,Fusion107]
FEATURE [Part::MultiFuse] Fusion109  label="plugHousing067"
  Placement = pos=(131.236,0,-0.15) rot=(0,0,1;0rad)
  Shapes = -> [Fusion108,Fusion111]
FEATURE [Part::MultiFuse] Fusion113  label="plugHousing079"
  Shapes = -> [Fillet043,Fusion109]
FEATURE [Part::Feature] Face135
  shape: bbox 3.5 x 17.8 x 2e-07 mm, 1 faces, 0 solids (baked)
FEATURE [Part::Revolution] Revolve143  label="removeToCreateScrewAndThreadedInsertHole049"
  Angle = 360
  Axis = (0,1,0)
  Base = (0,0,0)
  FaceMakerClass = Part::FaceMakerBullseye
  Placement = pos=(12.5,0,10) rot=(0,0,1;0rad)
  Solid = false
  Source = -> Face135
  Symmetric = false
FEATURE [Part::Feature] Face136
  shape: bbox 3.5 x 17.8 x 2e-07 mm, 1 faces, 0 solids (baked)
FEATURE [Part::Revolution] Revolve144  label="removeToCreateScrewAndThreadedInsertHole050"
  Angle = 360
  Axis = (0,1,0)
  Base = (0,0,0)
  FaceMakerClass = Part::FaceMakerBullseye
  Placement = pos=(12.5,0,62) rot=(0,0,1;0rad)
  Solid = false
  Source = -> Face136
  Symmetric = false
FEATURE [Part::Feature] Face137
  shape: bbox 3.5 x 17.8 x 2e-07 mm, 1 faces, 0 solids (baked)
FEATURE [Part::Revolution] Revolve145  label="removeToCreateScrewAndThreadedInsertHole051"
  Angle = 360
  Axis = (0,1,0)
  Base = (0,0,0)
  FaceMakerClass = Part::FaceMakerBullseye
  Placement = pos=(89.5,0,68.5) rot=(0,0,1;0rad)
  Solid = false
  Source = -> Face137
  Symmetric = false
FEATURE [Part::Feature] Face138
  shape: bbox 3.5 x 17.8 x 2e-07 mm, 1 faces, 0 solids (baked)
FEATURE [Part::Revolution] Revolve146  label="removeToCreateScrewAndThreadedInsertHole052"
  Angle = 360
  Axis = (0,1,0)
  Base = (0,0,0)
  FaceMakerClass = Part::FaceMakerBullseye
  Placement = pos=(89.5,0,3.5) rot=(0,0,1;0rad)
  Solid = false
  Source = -> Face138
  Symmetric = false
FEATURE [Part::Feature] Face139
  shape: bbox 3.5 x 17.8 x 2e-07 mm, 1 faces, 0 solids (baked)
FEATURE [Part::Revolution] Revolve147  label="removeToCreateScrewAndThreadedInsertHole053"
  Angle = 360
  Axis = (0,1,0)
  Base = (0,0,0)
  FaceMakerClass = Part::FaceMakerBullseye
  Placement = pos=(109.5,4.7,3.5) rot=(0,0,1;0rad)
  Solid = false
  Source = -> Face139
  Symmetric = false
FEATURE [Part::Feature] Face140
  shape: bbox 3.5 x 17.8 x 2e-07 mm, 1 faces, 0 solids (baked)
FEATURE [Part::Revolution] Revolve148  label="removeToCreateScrewAndThreadedInsertHole054"
  Angle = 360
  Axis = (0,1,0)
  Base = (0,0,0)
  FaceMakerClass = Part::FaceMakerBullseye
  Placement = pos=(109.5,4.7,68.5) rot=(0,0,1;0rad)
  Solid = false
  Source = -> Face140
  Symmetric = false
FEATURE [Part::MultiFuse] Fusion114  label="removeToCreateScrewAndThreadedInsertHole055"
  Shapes = -> [Revolve148,Revolve147,Revolve146,Revolve145,Revolve144,Revolve143]
FEATURE [Part::Cut] Cut047  label="casePillars004"
  Base = -> Cut037
  Tool = -> Fusion114
FEATURE [Part::Feature] Face141
  shape: bbox 3.5 x 17.8 x 2e-07 mm, 1 faces, 0 solids (baked)
FEATURE [Part::Feature] Face142
  shape: bbox 3.5 x 17.8 x 2e-07 mm, 1 faces, 0 solids (baked)
FEATURE [Part::Feature] Face143
  shape: bbox 3.5 x 17.8 x 2e-07 mm, 1 faces, 0 solids (baked)
FEATURE [Part::Revolution] Revolve149  label="removeToCreateScrewAndThreadedInsertHole057"
  Angle = 360
  Axis = (0,1,0)
  Base = (0,0,0)
  FaceMakerClass = Part::FaceMakerBullseye
  Placement = pos=(12.5,0,10) rot=(0,0,1;0rad)
  Solid = false
  Source = -> Face141
  Symmetric = false
FEATURE [Part::Feature] Face144
  shape: bbox 3.5 x 17.8 x 2e-07 mm, 1 faces, 0 solids (baked)
FEATURE [Part::Feature] Face145
  shape: bbox 3.5 x 17.8 x 2e-07 mm, 1 faces, 0 solids (baked)
FEATURE [Part::Feature] Face146
  shape: bbox 3.5 x 17.8 x 2e-07 mm, 1 faces, 0 solids (baked)
FEATURE [Part::Revolution] Revolve150  label="removeToCreateScrewAndThreadedInsertHole058"
  Angle = 360
  Axis = (0,1,0)
  Base = (0,0,0)
  FaceMakerClass = Part::FaceMakerBullseye
  Placement = pos=(12.5,0,62) rot=(0,0,1;0rad)
  Solid = false
  Source = -> Face146
  Symmetric = false
FEATURE [Part::Revolution] Revolve151  label="removeToCreateScrewAndThreadedInsertHole059"
  Angle = 360
  Axis = (0,1,0)
  Base = (0,0,0)
  FaceMakerClass = Part::FaceMakerBullseye
  Placement = pos=(89.5,0,68.5) rot=(0,0,1;0rad)
  Solid = false
  Source = -> Face143
  Symmetric = false
FEATURE [Part::Revolution] Revolve152  label="removeToCreateScrewAndThreadedInsertHole060"
  Angle = 360
  Axis = (0,1,0)
  Base = (0,0,0)
  FaceMakerClass = Part::FaceMakerBullseye
  Placement = pos=(89.5,0,3.5) rot=(0,0,1;0rad)
  Solid = false
  Source = -> Face142
  Symmetric = false
FEATURE [Part::Revolution] Revolve153  label="removeToCreateScrewAndThreadedInsertHole061"
  Angle = 360
  Axis = (0,1,0)
  Base = (0,0,0)
  FaceMakerClass = Part::FaceMakerBullseye
  Placement = pos=(109.5,4.7,3.5) rot=(0,0,1;0rad)
  Solid = false
  Source = -> Face145
  Symmetric = false
FEATURE [Part::Revolution] Revolve154  label="removeToCreateScrewAndThreadedInsertHole062"
  Angle = 360
  Axis = (0,1,0)
  Base = (0,0,0)
  FaceMakerClass = Part::FaceMakerBullseye
  Placement = pos=(109.5,4.7,68.5) rot=(0,0,1;0rad)
  Solid = false
  Source = -> Face144
  Symmetric = false
FEATURE [Part::MultiFuse] Fusion115  label="removeToCreateScrewAndThreadedInsertHole056"
  Shapes = -> [Revolve154,Revolve153,Revolve152,Revolve151,Revolve150,Revolve149]
FEATURE [Part::Cut] Cut048  label="bottom013"
  Base = -> Fusion093
  Tool = -> Fusion115
FEATURE [Part::Feature] Face147
  shape: bbox 9.8 x 26.5 x 2e-07 mm, 1 faces, 0 solids (baked)
FEATURE [Part::Revolution] Revolve155
  Angle = 360
  Axis = (0,1,0)
  Base = (0,0,0)
  FaceMakerClass = Part::FaceMakerBullseye
  Placement = pos=(0,0,0) rot=(0,0,1;1.5708rad)
  Solid = false
  Source = -> Face147
  Symmetric = false
FEATURE [Part::Feature] Face148
  shape: bbox 9.8 x 26.5 x 2e-07 mm, 1 faces, 0 solids (baked)
FEATURE [Part::Revolution] Revolve156
  Angle = 360
  Axis = (0,1,0)
  Base = (0,0,0)
  FaceMakerClass = Part::FaceMakerBullseye
  Placement = pos=(0,0,0) rot=(0,0,1;1.5708rad)
  Solid = false
  Source = -> Face148
  Symmetric = false
FEATURE [Part::MultiFuse] Fusion116
  Placement = pos=(-18,19,36) rot=(0,0,1;0rad)
  Shapes = -> [Revolve156,Revolve155]
FEATURE [Part::Box] Box029  label="Cube016"
  AttacherType = Attacher::AttachEngine3D
  Height = 28
  Length = 3
  Placement = pos=(110.7,19,22) rot=(0,0,1;0rad)
  Width = 15.7
FEATURE [Part::Cylinder] Cylinder046
  Angle = 360
  AttacherType = Attacher::AttachEngine3D
  Height = 10
  Placement = pos=(0,0,36.15) rot=(0,0,1;0rad)
  Radius = 4
FEATURE [Part::Cylinder] Cylinder047
  Angle = 360
  AttacherType = Attacher::AttachEngine3D
  Height = 20
  Placement = pos=(0,0,36.15) rot=(0,0,1;0rad)
  Radius = 10.3
FEATURE [Part::MultiFuse] Fusion117  label="removeToCreteHoleForPlugHousing041"
  Placement = pos=(70,19,36) rot=(0,1,0;1.5708rad)
  Shapes = -> [Cylinder047,Cylinder046]
FEATURE [Part::Cut] Cut049  label="plugHousingTab004"
  Base = -> Box029
  Placement = pos=(-107.4,-14,0) rot=(0,0,1;0rad)
  Tool = -> Fusion117
FEATURE [Part::Box] Box030  label="Cube017"
  AttacherType = Attacher::AttachEngine3D
  Height = 28
  Length = 3
  Placement = pos=(110.7,19,22) rot=(0,0,1;0rad)
  Width = 15.7
FEATURE [Part::Cylinder] Cylinder048
  Angle = 360
  AttacherType = Attacher::AttachEngine3D
  Height = 10
  Placement = pos=(0,0,36.15) rot=(0,0,1;0rad)
  Radius = 4
FEATURE [Part::Cylinder] Cylinder049
  Angle = 360
  AttacherType = Attacher::AttachEngine3D
  Height = 20
  Placement = pos=(0,0,36.15) rot=(0,0,1;0rad)
  Radius = 10.3
FEATURE [Part::MultiFuse] Fusion118  label="removeToCreteHoleForPlugHousing042"
  Placement = pos=(70,19,36) rot=(0,1,0;1.5708rad)
  Shapes = -> [Cylinder049,Cylinder048]
FEATURE [Part::Cut] Cut050  label="plugHousingTab005"
  Base = -> Box030
  Placement = pos=(-107.4,-14,0) rot=(0,0,1;0rad)
  Tool = -> Fusion118
FEATURE [Part::MultiFuse] Fusion119
  Placement = pos=(9.6,23,0) rot=(0,0,1;3.14159rad)
  Shapes = -> [Cut049,Cut050]
FEATURE [Part::Box] Box031  label="Cube018"
  AttacherType = Attacher::AttachEngine3D
  Height = 10
  Length = 3
  Placement = pos=(3.3,4,12) rot=(0,0,1;0rad)
  Width = 10
FEATURE [Part::Fillet] Fillet044
  Base = -> Box031
  Edges = 1 edges r=2: [Edge11]
FEATURE [Part::Box] Box032  label="Cube019"
  AttacherType = Attacher::AttachEngine3D
  Height = 10
  Length = 3
  Placement = pos=(3.3,4,50) rot=(0,0,1;0rad)
  Width = 10
FEATURE [Part::Fillet] Fillet045
  Base = -> Box032
  Edges = 1 edges r=2: [Edge12]
FEATURE [Part::Box] Box033  label="Cube020"
  AttacherType = Attacher::AttachEngine3D
  Height = 28
  Length = 4
  Placement = pos=(5,0,22) rot=(0,0,1;0rad)
  Width = 10
FEATURE [Part::Fillet] Fillet046
  Base = -> Box033
  Edges = 1 edges r=1: [Edge7]
FEATURE [Part::Fillet] Fillet047
  Base = -> Fillet046
  Edges = 1 edges r=2: [Edge5]
FEATURE [Part::Fillet] Fillet048
  Base = -> Fillet047
  Edges = 1 edges r=2: [Edge2]
FEATURE [Part::Cylinder] Cylinder050
  Angle = 360
  AttacherType = Attacher::AttachEngine3D
  Height = 20
  Placement = pos=(0,0,36.15) rot=(0,0,1;0rad)
  Radius = 8.2
FEATURE [Part::Cylinder] Cylinder051
  Angle = 360
  AttacherType = Attacher::AttachEngine3D
  Height = 10
  Placement = pos=(0,0,36.15) rot=(0,0,1;0rad)
  Radius = 4
FEATURE [Part::MultiFuse] Fusion120  label="removeToCreteHoleForPlugHousing043"
  Placement = pos=(-42,19,36) rot=(0,1,0;1.5708rad)
  Shapes = -> [Cylinder050,Cylinder051]
FEATURE [Sketcher::SketchObject] Sketch067  label="topSketch018"
  FullyConstrained = true
  sketch-geometry (4):
    g0: LineSegment StartX=16.8446 StartY=31.512 StartZ=0 EndX=16.3251 EndY=34.4666 EndZ=0
    g1: ArcOfCircle CenterX=19 CenterY=19.2524 CenterZ=0 NormalX=0 NormalY=0 NormalZ=1 AngleXU=0 Radius=15.4476 StartAngle=1.74483 EndAngle=2.72717
    g2: ArcOfCircle CenterX=19 CenterY=19.2524 CenterZ=0 NormalX=0 NormalY=0 NormalZ=1 AngleXU=0 Radius=12.4476 StartAngle=1.74483 EndAngle=2.73189
    g3: LineSegment StartX=4.86004 StartY=25.4725 StartZ=0 EndX=7.58253 EndY=24.2107 EndZ=0
  constraints (7):
    c: Block(g0)
    c: Coincident(g1,g0)
    c: Coincident(g2,g0)
    c: Coincident(g3,g1)
    c: Coincident(g3,g2)
    c: Block(g1)
    c: Block(g2)
FEATURE [Part::Extrusion] Extrude058
  Base = -> Sketch067
  Dir = (0,0,1)
  DirMode = 2
  FaceMakerClass = Part::FaceMakerBullseye
  LengthFwd = 10
  LengthRev = 0
  Placement = pos=(0,0,31) rot=(0,0,1;0rad)
  Solid = true
  Symmetric = false
FEATURE [Part::Cut] Cut051
  Base = -> Extrude058
  Tool = -> Fusion120
FEATURE [Part::Fillet] Fillet049
  Base = -> Cut051
  Edges = 1 edges r=2: [Edge1]
FEATURE [Part::Fillet] Fillet050
  Base = -> Fillet049
  Edges = 1 edges r=2.5: [Edge1]
FEATURE [Part::Fillet] Fillet051
  Base = -> Fillet050
  Edges = 1 edges r=2.5: [Edge2]
FEATURE [Part::MultiFuse] Fusion121  label="wireHolder003"
  Shapes = -> [Fusion116,Fillet051]
FEATURE [Part::MultiFuse] Fusion122
  Shapes = -> [Fillet045,Fusion121]
FEATURE [Part::MultiFuse] Fusion123  label="wireHolder004"
  Shapes = -> [Fusion122,Fillet048]
FEATURE [Part::MultiFuse] Fusion124  label="wireHolder005"
  Shapes = -> [Fillet044,Fusion119,Fusion123]
